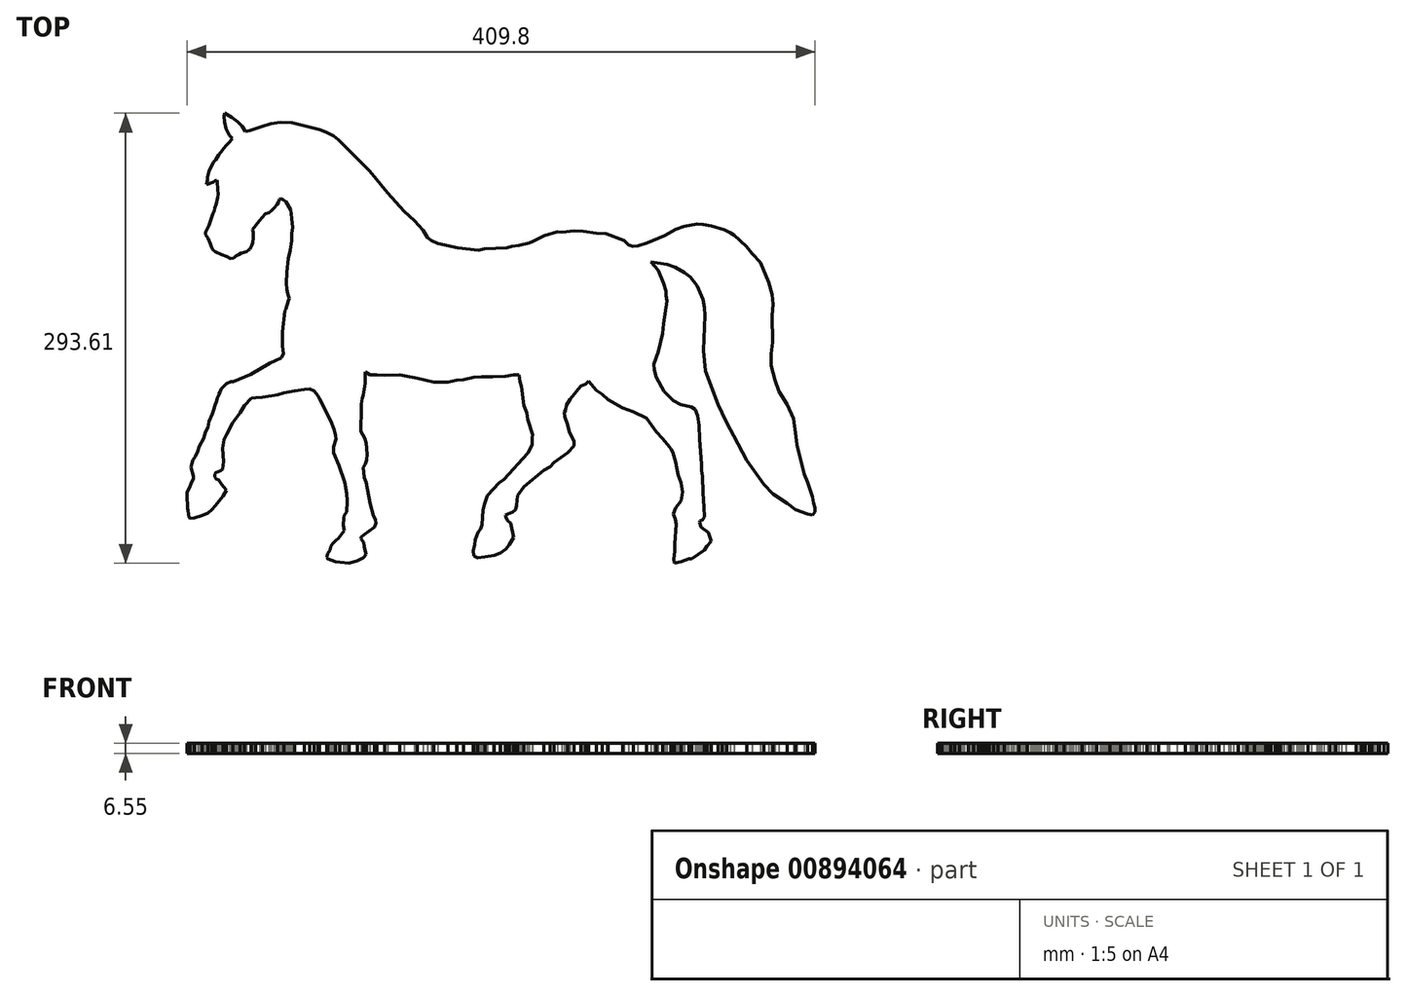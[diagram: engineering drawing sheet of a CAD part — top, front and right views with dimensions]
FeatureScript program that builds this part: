
annotation { "Feature Type Name" : "Feature", "Feature Type Description" : "" }
export const myFeature = defineFeature(function(context is Context, id is Id, definition is map)
    precondition{}
    {
        {
            var Q0;
            Q0=qCreatedBy(makeId("Top.planeOp"),FACE);
            var sketch = newSketch(context, id + "F0", { "sketchPlane" : qUnion([Q0])});
            skLineSegment(sketch, "E0", {"start": v(-21915.78, 16280.24) * mm, "end": v(-22000.3, 16149.3) * mm});
            skLineSegment(sketch, "E1", {"start": v(-22000.3, 16149.3) * mm, "end": v(-22091.45, 16008.1) * mm});
            skLineSegment(sketch, "E2", {"start": v(-22091.45, 16008.1) * mm, "end": v(-22247.54, 15864.17) * mm});
            skLineSegment(sketch, "E3", {"start": v(-22247.54, 15864.17) * mm, "end": v(-22423.74, 15701.7) * mm});
            skLineSegment(sketch, "E4", {"start": v(-22423.74, 15701.7) * mm, "end": v(-22570.85, 15517.79) * mm});
            skLineSegment(sketch, "E5", {"start": v(-22570.85, 15517.79) * mm, "end": v(-22722.85, 15327.75) * mm});
            skLineSegment(sketch, "E6", {"start": v(-22722.85, 15327.75) * mm, "end": v(-22881.74, 15129.12) * mm});
            skLineSegment(sketch, "E7", {"start": v(-22881.74, 15129.12) * mm, "end": v(-23029.7, 14944.14) * mm});
            skLineSegment(sketch, "E8", {"start": v(-23029.7, 14944.14) * mm, "end": v(-23266.76, 14559.18) * mm});
            skLineSegment(sketch, "E9", {"start": v(-23266.76, 14559.18) * mm, "end": v(-23478.07, 14331.08) * mm});
            skLineSegment(sketch, "E10", {"start": v(-23478.07, 14331.08) * mm, "end": v(-23552.03, 14153.67) * mm});
            skLineSegment(sketch, "E11", {"start": v(-23552.03, 14153.67) * mm, "end": v(-23710.77, 13873.46) * mm});
            skLineSegment(sketch, "E12", {"start": v(-23710.77, 13873.46) * mm, "end": v(-23812.2, 13596.78) * mm});
            skLineSegment(sketch, "E13", {"start": v(-23812.2, 13596.78) * mm, "end": v(-23838.03, 13426.67) * mm});
            skLineSegment(sketch, "E14", {"start": v(-23838.03, 13426.67) * mm, "end": v(-23918.33, 13133.1) * mm});
            skLineSegment(sketch, "E15", {"start": v(-23918.33, 13133.1) * mm, "end": v(-23935.24, 12928.22) * mm});
            skLineSegment(sketch, "E16", {"start": v(-23935.24, 12928.22) * mm, "end": v(-23983.84, 12738.14) * mm});
            skLineSegment(sketch, "E17", {"start": v(-23983.84, 12738.14) * mm, "end": v(-23996.52, 12539.6) * mm});
            skLineSegment(sketch, "E18", {"start": v(-23996.52, 12539.6) * mm, "end": v(-23707.02, 12632.53) * mm});
            skLineSegment(sketch, "E19", {"start": v(-23707.02, 12632.53) * mm, "end": v(-23478, 12706.05) * mm});
            skLineSegment(sketch, "E20", {"start": v(-23478, 12706.05) * mm, "end": v(-23297.08, 12833.18) * mm});
            skLineSegment(sketch, "E21", {"start": v(-23297.08, 12833.18) * mm, "end": v(-23193.54, 12877.53) * mm});
            skLineSegment(sketch, "E22", {"start": v(-23193.54, 12877.53) * mm, "end": v(-23157.61, 12742.36) * mm});
            skLineSegment(sketch, "E23", {"start": v(-23157.61, 12742.36) * mm, "end": v(-23121.56, 12443.79) * mm});
            skLineSegment(sketch, "E24", {"start": v(-23121.56, 12443.79) * mm, "end": v(-23082.96, 12124.17) * mm});
            skLineSegment(sketch, "E25", {"start": v(-23082.96, 12124.17) * mm, "end": v(-23079.3, 11739.43) * mm});
            skLineSegment(sketch, "E26", {"start": v(-23079.3, 11739.43) * mm, "end": v(-23100.44, 11473.3) * mm});
            skLineSegment(sketch, "E27", {"start": v(-23100.44, 11473.3) * mm, "end": v(-23163.98, 11187.46) * mm});
            skLineSegment(sketch, "E28", {"start": v(-23163.98, 11187.46) * mm, "end": v(-23215.72, 10954.66) * mm});
            skLineSegment(sketch, "E29", {"start": v(-23215.72, 10954.66) * mm, "end": v(-23326.6, 10630.9) * mm});
            skLineSegment(sketch, "E30", {"start": v(-23326.6, 10630.9) * mm, "end": v(-23392.11, 10362.67) * mm});
            skLineSegment(sketch, "E31", {"start": v(-23392.11, 10362.67) * mm, "end": v(-23489.31, 10140.9) * mm});
            skLineSegment(sketch, "E32", {"start": v(-23489.31, 10140.9) * mm, "end": v(-23561.34, 9888.44) * mm});
            skLineSegment(sketch, "E33", {"start": v(-23561.34, 9888.44) * mm, "end": v(-23677.56, 9675.12) * mm});
            skLineSegment(sketch, "E34", {"start": v(-23677.56, 9675.12) * mm, "end": v(-23740.95, 9470.25) * mm});
            skLineSegment(sketch, "E35", {"start": v(-23740.95, 9470.25) * mm, "end": v(-23823.7, 9202.85) * mm});
            skLineSegment(sketch, "E36", {"start": v(-23823.7, 9202.85) * mm, "end": v(-23910.14, 9025.74) * mm});
            skLineSegment(sketch, "E37", {"start": v(-23910.14, 9025.74) * mm, "end": v(-23980.17, 8882.26) * mm});
            skLineSegment(sketch, "E38", {"start": v(-23980.17, 8882.26) * mm, "end": v(-24052.25, 8734.58) * mm});
            skLineSegment(sketch, "E39", {"start": v(-24052.25, 8734.58) * mm, "end": v(-24102.07, 8632.52) * mm});
            skLineSegment(sketch, "E40", {"start": v(-24102.07, 8632.52) * mm, "end": v(-24096.15, 8435.6) * mm});
            skLineSegment(sketch, "E41", {"start": v(-24096.15, 8435.6) * mm, "end": v(-23893.3, 8139.91) * mm});
            skLineSegment(sketch, "E42", {"start": v(-23893.3, 8139.91) * mm, "end": v(-23700.9, 7699.92) * mm});
            skLineSegment(sketch, "E43", {"start": v(-23700.9, 7699.92) * mm, "end": v(-23616.23, 7435.42) * mm});
            skLineSegment(sketch, "E44", {"start": v(-23616.23, 7435.42) * mm, "end": v(-23493.55, 7196.45) * mm});
            skLineSegment(sketch, "E45", {"start": v(-23493.55, 7196.45) * mm, "end": v(-23297.04, 7052.83) * mm});
            skLineSegment(sketch, "E46", {"start": v(-23297.04, 7052.83) * mm, "end": v(-22781.4, 6798.75) * mm});
            skLineSegment(sketch, "E47", {"start": v(-22781.4, 6798.75) * mm, "end": v(-22344, 6646.68) * mm});
            skLineSegment(sketch, "E48", {"start": v(-22344, 6646.68) * mm, "end": v(-22051.24, 6487.55) * mm});
            skLineSegment(sketch, "E49", {"start": v(-22051.24, 6487.55) * mm, "end": v(-21795.56, 6525.57) * mm});
            skLineSegment(sketch, "E50", {"start": v(-21795.56, 6525.57) * mm, "end": v(-21624.4, 6692.42) * mm});
            skLineSegment(sketch, "E51", {"start": v(-21624.4, 6692.42) * mm, "end": v(-21394.07, 6808.59) * mm});
            skLineSegment(sketch, "E52", {"start": v(-21394.07, 6808.59) * mm, "end": v(-21210.23, 6941.65) * mm});
            skLineSegment(sketch, "E53", {"start": v(-21210.23, 6941.65) * mm, "end": v(-21009.48, 6996.56) * mm});
            skLineSegment(sketch, "E54", {"start": v(-21009.48, 6996.56) * mm, "end": v(-20760.56, 7064.65) * mm});
            skLineSegment(sketch, "E55", {"start": v(-20760.56, 7064.65) * mm, "end": v(-20556.49, 7193.23) * mm});
            skLineSegment(sketch, "E56", {"start": v(-20556.49, 7193.23) * mm, "end": v(-20473.06, 7245.8) * mm});
            skLineSegment(sketch, "E57", {"start": v(-20473.06, 7245.8) * mm, "end": v(-20310.55, 7574.46) * mm});
            skLineSegment(sketch, "E58", {"start": v(-20310.55, 7574.46) * mm, "end": v(-20236.6, 7804.68) * mm});
            skLineSegment(sketch, "E59", {"start": v(-20236.6, 7804.68) * mm, "end": v(-20213.35, 8161.62) * mm});
            skLineSegment(sketch, "E60", {"start": v(-20213.35, 8161.62) * mm, "end": v(-20217.6, 8443.51) * mm});
            skLineSegment(sketch, "E61", {"start": v(-20217.6, 8443.51) * mm, "end": v(-20221, 8669.65) * mm});
            skLineSegment(sketch, "E62", {"start": v(-20221, 8669.65) * mm, "end": v(-20270.42, 8836.36) * mm});
            skLineSegment(sketch, "E63", {"start": v(-20270.42, 8836.36) * mm, "end": v(-20135.04, 9014.46) * mm});
            skLineSegment(sketch, "E64", {"start": v(-20135.04, 9014.46) * mm, "end": v(-19942.51, 9267.73) * mm});
            skLineSegment(sketch, "E65", {"start": v(-19942.51, 9267.73) * mm, "end": v(-19700.94, 9585.52) * mm});
            skLineSegment(sketch, "E66", {"start": v(-19700.94, 9585.52) * mm, "end": v(-19473.4, 9807.2) * mm});
            skLineSegment(sketch, "E67", {"start": v(-19473.4, 9807.2) * mm, "end": v(-19225.81, 10150.22) * mm});
            skLineSegment(sketch, "E68", {"start": v(-19225.81, 10150.22) * mm, "end": v(-18953.22, 10238.92) * mm});
            skLineSegment(sketch, "E69", {"start": v(-18953.22, 10238.92) * mm, "end": v(-18743.24, 10361.65) * mm});
            skLineSegment(sketch, "E70", {"start": v(-18743.24, 10361.65) * mm, "end": v(-18519.25, 10566.52) * mm});
            skLineSegment(sketch, "E71", {"start": v(-18519.25, 10566.52) * mm, "end": v(-18250.48, 10913.46) * mm});
            skLineSegment(sketch, "E72", {"start": v(-18250.48, 10913.46) * mm, "end": v(-18142.47, 11098.26) * mm});
            skLineSegment(sketch, "E73", {"start": v(-18142.47, 11098.26) * mm, "end": v(-18100.21, 11237.66) * mm});
            skLineSegment(sketch, "E74", {"start": v(-18100.21, 11237.66) * mm, "end": v(-18049.5, 11326.37) * mm});
            skLineSegment(sketch, "E75", {"start": v(-18049.5, 11326.37) * mm, "end": v(-17929.05, 11368.6) * mm});
            skLineSegment(sketch, "E76", {"start": v(-17929.05, 11368.6) * mm, "end": v(-17768.45, 11301.02) * mm});
            skLineSegment(sketch, "E77", {"start": v(-17768.45, 11301.02) * mm, "end": v(-17565.6, 11132.06) * mm});
            skLineSegment(sketch, "E78", {"start": v(-17565.6, 11132.06) * mm, "end": v(-17424.02, 10893.4) * mm});
            skLineSegment(sketch, "E79", {"start": v(-17424.02, 10893.4) * mm, "end": v(-17297.06, 10679.38) * mm});
            skLineSegment(sketch, "E80", {"start": v(-17297.06, 10679.38) * mm, "end": v(-17164.28, 10455.56) * mm});
            skLineSegment(sketch, "E81", {"start": v(-17164.28, 10455.56) * mm, "end": v(-17096.15, 10159.32) * mm});
            skLineSegment(sketch, "E82", {"start": v(-17096.15, 10159.32) * mm, "end": v(-17070.8, 9916.43) * mm});
            skLineSegment(sketch, "E83", {"start": v(-17070.8, 9916.43) * mm, "end": v(-17052.77, 9743.8) * mm});
            skLineSegment(sketch, "E84", {"start": v(-17052.77, 9743.8) * mm, "end": v(-17032.08, 9422.22) * mm});
            skLineSegment(sketch, "E85", {"start": v(-17032.08, 9422.22) * mm, "end": v(-17007.66, 9042.48) * mm});
            skLineSegment(sketch, "E86", {"start": v(-17007.66, 9042.48) * mm, "end": v(-17035.08, 8751.12) * mm});
            skLineSegment(sketch, "E87", {"start": v(-17035.08, 8751.12) * mm, "end": v(-17057.97, 8507.85) * mm});
            skLineSegment(sketch, "E88", {"start": v(-17057.97, 8507.85) * mm, "end": v(-17074.62, 7945.34) * mm});
            skLineSegment(sketch, "E89", {"start": v(-17074.62, 7945.34) * mm, "end": v(-17126.43, 7579.78) * mm});
            skLineSegment(sketch, "E90", {"start": v(-17126.43, 7579.78) * mm, "end": v(-17185.47, 7163.26) * mm});
            skLineSegment(sketch, "E91", {"start": v(-17185.47, 7163.26) * mm, "end": v(-17272.81, 6780.14) * mm});
            skLineSegment(sketch, "E92", {"start": v(-17272.81, 6780.14) * mm, "end": v(-17340.94, 6481.3) * mm});
            skLineSegment(sketch, "E93", {"start": v(-17340.94, 6481.3) * mm, "end": v(-17425.28, 5834.24) * mm});
            skLineSegment(sketch, "E94", {"start": v(-17425.28, 5834.24) * mm, "end": v(-17483.88, 5384.66) * mm});
            skLineSegment(sketch, "E95", {"start": v(-17483.88, 5384.66) * mm, "end": v(-17495.33, 4863.98) * mm});
            skLineSegment(sketch, "E96", {"start": v(-17495.33, 4863.98) * mm, "end": v(-17504.17, 4462) * mm});
            skLineSegment(sketch, "E97", {"start": v(-17504.17, 4462) * mm, "end": v(-17470.8, 3976.05) * mm});
            skLineSegment(sketch, "E98", {"start": v(-17470.8, 3976.05) * mm, "end": v(-17388.5, 3583.07) * mm});
            skLineSegment(sketch, "E99", {"start": v(-17388.5, 3583.07) * mm, "end": v(-17257.23, 3246.2) * mm});
            skLineSegment(sketch, "E100", {"start": v(-17257.23, 3246.2) * mm, "end": v(-17363.9, 3048.18) * mm});
            skLineSegment(sketch, "E101", {"start": v(-17363.9, 3048.18) * mm, "end": v(-17421.81, 2844.08) * mm});
            skLineSegment(sketch, "E102", {"start": v(-17421.81, 2844.08) * mm, "end": v(-17486.24, 2617) * mm});
            skLineSegment(sketch, "E103", {"start": v(-17486.24, 2617) * mm, "end": v(-17559.1, 2360.2) * mm});
            skLineSegment(sketch, "E104", {"start": v(-17559.1, 2360.2) * mm, "end": v(-17632.11, 2240.9) * mm});
            skLineSegment(sketch, "E105", {"start": v(-17632.11, 2240.9) * mm, "end": v(-17693, 1693.79) * mm});
            skLineSegment(sketch, "E106", {"start": v(-17693, 1693.79) * mm, "end": v(-17746.7, 1211.32) * mm});
            skLineSegment(sketch, "E107", {"start": v(-17746.7, 1211.32) * mm, "end": v(-17782.24, 892.05) * mm});
            skLineSegment(sketch, "E108", {"start": v(-17782.24, 892.05) * mm, "end": v(-17825.3, 505.21) * mm});
            skLineSegment(sketch, "E109", {"start": v(-17825.3, 505.21) * mm, "end": v(-17824.2, 62.7) * mm});
            skLineSegment(sketch, "E110", {"start": v(-17824.2, 62.7) * mm, "end": v(-17822.4, -667.43) * mm});
            skLineSegment(sketch, "E111", {"start": v(-17822.4, -667.43) * mm, "end": v(-17726.52, -1255.3) * mm});
            skLineSegment(sketch, "E112", {"start": v(-17726.52, -1255.3) * mm, "end": v(-17912.72, -1607.53) * mm});
            skLineSegment(sketch, "E113", {"start": v(-17912.72, -1607.53) * mm, "end": v(-18400.37, -1851.24) * mm});
            skLineSegment(sketch, "E114", {"start": v(-18400.37, -1851.24) * mm, "end": v(-18872.79, -2030.97) * mm});
            skLineSegment(sketch, "E115", {"start": v(-18872.79, -2030.97) * mm, "end": v(-19333.99, -2305.95) * mm});
            skLineSegment(sketch, "E116", {"start": v(-19333.99, -2305.95) * mm, "end": v(-19749.18, -2553.5) * mm});
            skLineSegment(sketch, "E117", {"start": v(-19749.18, -2553.5) * mm, "end": v(-20392.98, -2937.34) * mm});
            skLineSegment(sketch, "E118", {"start": v(-20392.98, -2937.34) * mm, "end": v(-20969.35, -3175.43) * mm});
            skLineSegment(sketch, "E119", {"start": v(-20969.35, -3175.43) * mm, "end": v(-21492.25, -3391.42) * mm});
            skLineSegment(sketch, "E120", {"start": v(-21492.25, -3391.42) * mm, "end": v(-21848.77, -3538.7) * mm});
            skLineSegment(sketch, "E121", {"start": v(-21848.77, -3538.7) * mm, "end": v(-22040.13, -3541.57) * mm});
            skLineSegment(sketch, "E122", {"start": v(-22040.13, -3541.57) * mm, "end": v(-22378.44, -3712.16) * mm});
            skLineSegment(sketch, "E123", {"start": v(-22378.44, -3712.16) * mm, "end": v(-22619.22, -3928.45) * mm});
            skLineSegment(sketch, "E124", {"start": v(-22619.22, -3928.45) * mm, "end": v(-22814.99, -4161.1) * mm});
            skLineSegment(sketch, "E125", {"start": v(-22814.99, -4161.1) * mm, "end": v(-22903.37, -4374.34) * mm});
            skLineSegment(sketch, "E126", {"start": v(-22903.37, -4374.34) * mm, "end": v(-23025.29, -4581.5) * mm});
            skLineSegment(sketch, "E127", {"start": v(-23025.29, -4581.5) * mm, "end": v(-23034.43, -4678.97) * mm});
            skLineSegment(sketch, "E128", {"start": v(-23034.43, -4678.97) * mm, "end": v(-23156.34, -4910.5) * mm});
            skLineSegment(sketch, "E129", {"start": v(-23156.34, -4910.5) * mm, "end": v(-23195.97, -5096.32) * mm});
            skLineSegment(sketch, "E130", {"start": v(-23195.97, -5096.32) * mm, "end": v(-23336.51, -5518.13) * mm});
            skLineSegment(sketch, "E131", {"start": v(-23336.51, -5518.13) * mm, "end": v(-23403.57, -5822.76) * mm});
            skLineSegment(sketch, "E132", {"start": v(-23403.57, -5822.76) * mm, "end": v(-23547.15, -6183.25) * mm});
            skLineSegment(sketch, "E133", {"start": v(-23547.15, -6183.25) * mm, "end": v(-23680.71, -6518.58) * mm});
            skLineSegment(sketch, "E134", {"start": v(-23680.71, -6518.58) * mm, "end": v(-23800.04, -6818.17) * mm});
            skLineSegment(sketch, "E135", {"start": v(-23800.04, -6818.17) * mm, "end": v(-23907.1, -7279.6) * mm});
            skLineSegment(sketch, "E136", {"start": v(-23907.1, -7279.6) * mm, "end": v(-24099.12, -7632.98) * mm});
            skLineSegment(sketch, "E137", {"start": v(-24099.12, -7632.98) * mm, "end": v(-24153.98, -7840.13) * mm});
            skLineSegment(sketch, "E138", {"start": v(-24153.98, -7840.13) * mm, "end": v(-24180.17, -7939.01) * mm});
            skLineSegment(sketch, "E139", {"start": v(-24180.17, -7939.01) * mm, "end": v(-24244.61, -8182.34) * mm});
            skLineSegment(sketch, "E140", {"start": v(-24244.61, -8182.34) * mm, "end": v(-24391.71, -8443.3) * mm});
            skLineSegment(sketch, "E141", {"start": v(-24391.71, -8443.3) * mm, "end": v(-24612.18, -8834.42) * mm});
            skLineSegment(sketch, "E142", {"start": v(-24612.18, -8834.42) * mm, "end": v(-24718.2, -9224.56) * mm});
            skLineSegment(sketch, "E143", {"start": v(-24718.2, -9224.56) * mm, "end": v(-24944.2, -9670.84) * mm});
            skLineSegment(sketch, "E144", {"start": v(-24944.2, -9670.84) * mm, "end": v(-25111.84, -9929.78) * mm});
            skLineSegment(sketch, "E145", {"start": v(-25111.84, -9929.78) * mm, "end": v(-25224.6, -10197.86) * mm});
            skLineSegment(sketch, "E146", {"start": v(-25224.6, -10197.86) * mm, "end": v(-25300.8, -10523.81) * mm});
            skLineSegment(sketch, "E147", {"start": v(-25300.8, -10523.81) * mm, "end": v(-25090.87, -11238.22) * mm});
            skLineSegment(sketch, "E148", {"start": v(-25090.87, -11238.22) * mm, "end": v(-25096.97, -11439.28) * mm});
            skLineSegment(sketch, "E149", {"start": v(-25096.97, -11439.28) * mm, "end": v(-25289.28, -11864.54) * mm});
            skLineSegment(sketch, "E150", {"start": v(-25289.28, -11864.54) * mm, "end": v(-25411.2, -12211.82) * mm});
            skLineSegment(sketch, "E151", {"start": v(-25411.2, -12211.82) * mm, "end": v(-25591.01, -12553.01) * mm});
            skLineSegment(sketch, "E152", {"start": v(-25591.01, -12553.01) * mm, "end": v(-25612.35, -12757.11) * mm});
            skLineSegment(sketch, "E153", {"start": v(-25612.35, -12757.11) * mm, "end": v(-25603.22, -13163.9) * mm});
            skLineSegment(sketch, "E154", {"start": v(-25603.22, -13163.9) * mm, "end": v(-25548.36, -13495.96) * mm});
            skLineSegment(sketch, "E155", {"start": v(-25548.36, -13495.96) * mm, "end": v(-25557.5, -13858.47) * mm});
            skLineSegment(sketch, "E156", {"start": v(-25557.5, -13858.47) * mm, "end": v(-25517.91, -14073.04) * mm});
            skLineSegment(sketch, "E157", {"start": v(-25517.91, -14073.04) * mm, "end": v(-25460, -14609.2) * mm});
            skLineSegment(sketch, "E158", {"start": v(-25460, -14609.2) * mm, "end": v(-25347.23, -14688.4) * mm});
            skLineSegment(sketch, "E159", {"start": v(-25347.23, -14688.4) * mm, "end": v(-24993.69, -14657.93) * mm});
            skLineSegment(sketch, "E160", {"start": v(-24993.69, -14657.93) * mm, "end": v(-24359.74, -14456.88) * mm});
            skLineSegment(sketch, "E161", {"start": v(-24359.74, -14456.88) * mm, "end": v(-23905.61, -14246.68) * mm});
            skLineSegment(sketch, "E162", {"start": v(-23905.61, -14246.68) * mm, "end": v(-23591.68, -13987.74) * mm});
            skLineSegment(sketch, "E163", {"start": v(-23591.68, -13987.74) * mm, "end": v(-23299.1, -13673.97) * mm});
            skLineSegment(sketch, "E164", {"start": v(-23299.1, -13673.97) * mm, "end": v(-22956.74, -13228.65) * mm});
            skLineSegment(sketch, "E165", {"start": v(-22956.74, -13228.65) * mm, "end": v(-22680.7, -12869.58) * mm});
            skLineSegment(sketch, "E166", {"start": v(-22680.7, -12869.58) * mm, "end": v(-22477.78, -12533.12) * mm});
            skLineSegment(sketch, "E167", {"start": v(-22477.78, -12533.12) * mm, "end": v(-22386.03, -12381) * mm});
            skLineSegment(sketch, "E168", {"start": v(-22386.03, -12381) * mm, "end": v(-22630.64, -12139.87) * mm});
            skLineSegment(sketch, "E169", {"start": v(-22630.64, -12139.87) * mm, "end": v(-22770.84, -11908.35) * mm});
            skLineSegment(sketch, "E170", {"start": v(-22770.84, -11908.35) * mm, "end": v(-23039.4, -11563.13) * mm});
            skLineSegment(sketch, "E171", {"start": v(-23039.4, -11563.13) * mm, "end": v(-23234.47, -11502.2) * mm});
            skLineSegment(sketch, "E172", {"start": v(-23234.47, -11502.2) * mm, "end": v(-23332, -11319.42) * mm});
            skLineSegment(sketch, "E173", {"start": v(-23332, -11319.42) * mm, "end": v(-23347.12, -11107.4) * mm});
            skLineSegment(sketch, "E174", {"start": v(-23347.12, -11107.4) * mm, "end": v(-23261.78, -10973.37) * mm});
            skLineSegment(sketch, "E175", {"start": v(-23261.78, -10973.37) * mm, "end": v(-23094.15, -10897.21) * mm});
            skLineSegment(sketch, "E176", {"start": v(-23094.15, -10897.21) * mm, "end": v(-22865.9, -10793.5) * mm});
            skLineSegment(sketch, "E177", {"start": v(-22865.9, -10793.5) * mm, "end": v(-22694.89, -10680.92) * mm});
            skLineSegment(sketch, "E178", {"start": v(-22694.89, -10680.92) * mm, "end": v(-22673.55, -10495.1) * mm});
            skLineSegment(sketch, "E179", {"start": v(-22673.55, -10495.1) * mm, "end": v(-22621.66, -10043.12) * mm});
            skLineSegment(sketch, "E180", {"start": v(-22621.66, -10043.12) * mm, "end": v(-22663.85, -9567.5) * mm});
            skLineSegment(sketch, "E181", {"start": v(-22663.85, -9567.5) * mm, "end": v(-22695.89, -9206.28) * mm});
            skLineSegment(sketch, "E182", {"start": v(-22695.89, -9206.28) * mm, "end": v(-22715.67, -8983.22) * mm});
            skLineSegment(sketch, "E183", {"start": v(-22715.67, -8983.22) * mm, "end": v(-22572.07, -8289.2) * mm});
            skLineSegment(sketch, "E184", {"start": v(-22572.07, -8289.2) * mm, "end": v(-22380.06, -7859.67) * mm});
            skLineSegment(sketch, "E185", {"start": v(-22380.06, -7859.67) * mm, "end": v(-22090.2, -7307.05) * mm});
            skLineSegment(sketch, "E186", {"start": v(-22090.2, -7307.05) * mm, "end": v(-21860.43, -6869) * mm});
            skLineSegment(sketch, "E187", {"start": v(-21860.43, -6869) * mm, "end": v(-21474, -6343.3) * mm});
            skLineSegment(sketch, "E188", {"start": v(-21474, -6343.3) * mm, "end": v(-21275.88, -6073.79) * mm});
            skLineSegment(sketch, "E189", {"start": v(-21275.88, -6073.79) * mm, "end": v(-20909.62, -5501.3) * mm});
            skLineSegment(sketch, "E190", {"start": v(-20909.62, -5501.3) * mm, "end": v(-20687.13, -5257.6) * mm});
            skLineSegment(sketch, "E191", {"start": v(-20687.13, -5257.6) * mm, "end": v(-20351.58, -4890.05) * mm});
            skLineSegment(sketch, "E192", {"start": v(-20351.58, -4890.05) * mm, "end": v(-20022.18, -4857.29) * mm});
            skLineSegment(sketch, "E193", {"start": v(-20022.18, -4857.29) * mm, "end": v(-19469.09, -4838.97) * mm});
            skLineSegment(sketch, "E194", {"start": v(-19469.09, -4838.97) * mm, "end": v(-18758.94, -4704.93) * mm});
            skLineSegment(sketch, "E195", {"start": v(-18758.94, -4704.93) * mm, "end": v(-18215.77, -4602.4) * mm});
            skLineSegment(sketch, "E196", {"start": v(-18215.77, -4602.4) * mm, "end": v(-17718.5, -4466.97) * mm});
            skLineSegment(sketch, "E197", {"start": v(-17718.5, -4466.97) * mm, "end": v(-16833.92, -4288.88) * mm});
            skLineSegment(sketch, "E198", {"start": v(-16833.92, -4288.88) * mm, "end": v(-16050.63, -4170.07) * mm});
            skLineSegment(sketch, "E199", {"start": v(-16050.63, -4170.07) * mm, "end": v(-15597.52, -4139.48) * mm});
            skLineSegment(sketch, "E200", {"start": v(-15597.52, -4139.48) * mm, "end": v(-15231.78, -4300.93) * mm});
            skLineSegment(sketch, "E201", {"start": v(-15231.78, -4300.93) * mm, "end": v(-14923.95, -4696.95) * mm});
            skLineSegment(sketch, "E202", {"start": v(-14923.95, -4696.95) * mm, "end": v(-14814.23, -4949.8) * mm});
            skLineSegment(sketch, "E203", {"start": v(-14814.23, -4949.8) * mm, "end": v(-14420.75, -5723.13) * mm});
            skLineSegment(sketch, "E204", {"start": v(-14420.75, -5723.13) * mm, "end": v(-14148.3, -6258.62) * mm});
            skLineSegment(sketch, "E205", {"start": v(-14148.3, -6258.62) * mm, "end": v(-13902.4, -6741.93) * mm});
            skLineSegment(sketch, "E206", {"start": v(-13902.4, -6741.93) * mm, "end": v(-13631.1, -7436.77) * mm});
            skLineSegment(sketch, "E207", {"start": v(-13631.1, -7436.77) * mm, "end": v(-13481.75, -7908.95) * mm});
            skLineSegment(sketch, "E208", {"start": v(-13481.75, -7908.95) * mm, "end": v(-13454.13, -8224.44) * mm});
            skLineSegment(sketch, "E209", {"start": v(-13454.13, -8224.44) * mm, "end": v(-13554.7, -8556.48) * mm});
            skLineSegment(sketch, "E210", {"start": v(-13554.7, -8556.48) * mm, "end": v(-13653.82, -8883.71) * mm});
            skLineSegment(sketch, "E211", {"start": v(-13653.82, -8883.71) * mm, "end": v(-13649.1, -9362.04) * mm});
            skLineSegment(sketch, "E212", {"start": v(-13649.1, -9362.04) * mm, "end": v(-13435.75, -9858.59) * mm});
            skLineSegment(sketch, "E213", {"start": v(-13435.75, -9858.59) * mm, "end": v(-13207.45, -10389.93) * mm});
            skLineSegment(sketch, "E214", {"start": v(-13207.45, -10389.93) * mm, "end": v(-13005.85, -10999.46) * mm});
            skLineSegment(sketch, "E215", {"start": v(-13005.85, -10999.46) * mm, "end": v(-12758.24, -11748.1) * mm});
            skLineSegment(sketch, "E216", {"start": v(-12758.24, -11748.1) * mm, "end": v(-12587.1, -12687.54) * mm});
            skLineSegment(sketch, "E217", {"start": v(-12587.1, -12687.54) * mm, "end": v(-12556.61, -13275.48) * mm});
            skLineSegment(sketch, "E218", {"start": v(-12556.61, -13275.48) * mm, "end": v(-12589.9, -14185.58) * mm});
            skLineSegment(sketch, "E219", {"start": v(-12589.9, -14185.58) * mm, "end": v(-12772.77, -14407.96) * mm});
            skLineSegment(sketch, "E220", {"start": v(-12772.77, -14407.96) * mm, "end": v(-12839.82, -14663.85) * mm});
            skLineSegment(sketch, "E221", {"start": v(-12839.82, -14663.85) * mm, "end": v(-12876.2, -15241.64) * mm});
            skLineSegment(sketch, "E222", {"start": v(-12876.2, -15241.64) * mm, "end": v(-12784.77, -15701.63) * mm});
            skLineSegment(sketch, "E223", {"start": v(-12784.77, -15701.63) * mm, "end": v(-12973.73, -15945.34) * mm});
            skLineSegment(sketch, "E224", {"start": v(-12973.73, -15945.34) * mm, "end": v(-13272.19, -16330.25) * mm});
            skLineSegment(sketch, "E225", {"start": v(-13272.19, -16330.25) * mm, "end": v(-13467.85, -16477) * mm});
            skLineSegment(sketch, "E226", {"start": v(-13467.85, -16477) * mm, "end": v(-13729.97, -16757.26) * mm});
            skLineSegment(sketch, "E227", {"start": v(-13729.97, -16757.26) * mm, "end": v(-13885.4, -17007.06) * mm});
            skLineSegment(sketch, "E228", {"start": v(-13885.4, -17007.06) * mm, "end": v(-13949.41, -17266) * mm});
            skLineSegment(sketch, "E229", {"start": v(-13949.41, -17266) * mm, "end": v(-14114.6, -17575.44) * mm});
            skLineSegment(sketch, "E230", {"start": v(-14114.6, -17575.44) * mm, "end": v(-14196.88, -17886.16) * mm});
            skLineSegment(sketch, "E231", {"start": v(-14196.88, -17886.16) * mm, "end": v(-14142.02, -18014.1) * mm});
            skLineSegment(sketch, "E232", {"start": v(-14142.02, -18014.1) * mm, "end": v(-13867.72, -18105.5) * mm});
            skLineSegment(sketch, "E233", {"start": v(-13867.72, -18105.5) * mm, "end": v(-13512.03, -18224) * mm});
            skLineSegment(sketch, "E234", {"start": v(-13512.03, -18224) * mm, "end": v(-13124.05, -18288.28) * mm});
            skLineSegment(sketch, "E235", {"start": v(-13124.05, -18288.28) * mm, "end": v(-12694.3, -18315.7) * mm});
            skLineSegment(sketch, "E236", {"start": v(-12694.3, -18315.7) * mm, "end": v(-12397.24, -18334.65) * mm});
            skLineSegment(sketch, "E237", {"start": v(-12397.24, -18334.65) * mm, "end": v(-11702.7, -18136.37) * mm});
            skLineSegment(sketch, "E238", {"start": v(-11702.7, -18136.37) * mm, "end": v(-11233.34, -17917.03) * mm});
            skLineSegment(sketch, "E239", {"start": v(-11233.34, -17917.03) * mm, "end": v(-11009.84, -17651.84) * mm});
            skLineSegment(sketch, "E240", {"start": v(-11009.84, -17651.84) * mm, "end": v(-11067.75, -17365.49) * mm});
            skLineSegment(sketch, "E241", {"start": v(-11067.75, -17365.49) * mm, "end": v(-11174.42, -17012.11) * mm});
            skLineSegment(sketch, "E242", {"start": v(-11174.42, -17012.11) * mm, "end": v(-11198.74, -16645.2) * mm});
            skLineSegment(sketch, "E243", {"start": v(-11198.74, -16645.2) * mm, "end": v(-11338.94, -16480.69) * mm});
            skLineSegment(sketch, "E244", {"start": v(-11338.94, -16480.69) * mm, "end": v(-11429.2, -16374.77) * mm});
            skLineSegment(sketch, "E245", {"start": v(-11429.2, -16374.77) * mm, "end": v(-11399.9, -16194.34) * mm});
            skLineSegment(sketch, "E246", {"start": v(-11399.9, -16194.34) * mm, "end": v(-11207.88, -16054.2) * mm});
            skLineSegment(sketch, "E247", {"start": v(-11207.88, -16054.2) * mm, "end": v(-10947.08, -15863.87) * mm});
            skLineSegment(sketch, "E248", {"start": v(-10947.08, -15863.87) * mm, "end": v(-10526.32, -15556.8) * mm});
            skLineSegment(sketch, "E249", {"start": v(-10526.32, -15556.8) * mm, "end": v(-10310.28, -15399.14) * mm});
            skLineSegment(sketch, "E250", {"start": v(-10310.28, -15399.14) * mm, "end": v(-10222.44, -15104.77) * mm});
            skLineSegment(sketch, "E251", {"start": v(-10222.44, -15104.77) * mm, "end": v(-10262.06, -14775.77) * mm});
            skLineSegment(sketch, "E252", {"start": v(-10262.06, -14775.77) * mm, "end": v(-10387.02, -14507.7) * mm});
            skLineSegment(sketch, "E253", {"start": v(-10387.02, -14507.7) * mm, "end": v(-10542.55, -13985.32) * mm});
            skLineSegment(sketch, "E254", {"start": v(-10542.55, -13985.32) * mm, "end": v(-10690.41, -13488.65) * mm});
            skLineSegment(sketch, "E255", {"start": v(-10690.41, -13488.65) * mm, "end": v(-10786.47, -12938.88) * mm});
            skLineSegment(sketch, "E256", {"start": v(-10786.47, -12938.88) * mm, "end": v(-10863.46, -12498.22) * mm});
            skLineSegment(sketch, "E257", {"start": v(-10863.46, -12498.22) * mm, "end": v(-10988.61, -11781.88) * mm});
            skLineSegment(sketch, "E258", {"start": v(-10988.61, -11781.88) * mm, "end": v(-11140.02, -11374.57) * mm});
            skLineSegment(sketch, "E259", {"start": v(-11140.02, -11374.57) * mm, "end": v(-11249.7, -10525.38) * mm});
            skLineSegment(sketch, "E260", {"start": v(-11249.7, -10525.38) * mm, "end": v(-11082.07, -10281.67) * mm});
            skLineSegment(sketch, "E261", {"start": v(-11082.07, -10281.67) * mm, "end": v(-10957.1, -9955.71) * mm});
            skLineSegment(sketch, "E262", {"start": v(-10957.1, -9955.71) * mm, "end": v(-10914.26, -9445.55) * mm});
            skLineSegment(sketch, "E263", {"start": v(-10914.26, -9445.55) * mm, "end": v(-10950.83, -9019.07) * mm});
            skLineSegment(sketch, "E264", {"start": v(-10950.83, -9019.07) * mm, "end": v(-10992.68, -8531.1) * mm});
            skLineSegment(sketch, "E265", {"start": v(-10992.68, -8531.1) * mm, "end": v(-11136.78, -8167.7) * mm});
            skLineSegment(sketch, "E266", {"start": v(-11136.78, -8167.7) * mm, "end": v(-11295.27, -7872.2) * mm});
            skLineSegment(sketch, "E267", {"start": v(-11295.27, -7872.2) * mm, "end": v(-11448.65, -7586.24) * mm});
            skLineSegment(sketch, "E268", {"start": v(-11448.65, -7586.24) * mm, "end": v(-11448.06, -7352.77) * mm});
            skLineSegment(sketch, "E269", {"start": v(-11448.06, -7352.77) * mm, "end": v(-11446.86, -6877.5) * mm});
            skLineSegment(sketch, "E270", {"start": v(-11446.86, -6877.5) * mm, "end": v(-11393.02, -6391.84) * mm});
            skLineSegment(sketch, "E271", {"start": v(-11393.02, -6391.84) * mm, "end": v(-11396.07, -5913.57) * mm});
            skLineSegment(sketch, "E272", {"start": v(-11396.07, -5913.57) * mm, "end": v(-11399.6, -5360.23) * mm});
            skLineSegment(sketch, "E273", {"start": v(-11399.6, -5360.23) * mm, "end": v(-11335.1, -4891.23) * mm});
            skLineSegment(sketch, "E274", {"start": v(-11335.1, -4891.23) * mm, "end": v(-11252.81, -4662.76) * mm});
            skLineSegment(sketch, "E275", {"start": v(-11252.81, -4662.76) * mm, "end": v(-11066.7, -3679.84) * mm});
            skLineSegment(sketch, "E276", {"start": v(-11066.7, -3679.84) * mm, "end": v(-11075.85, -3338.65) * mm});
            skLineSegment(sketch, "E277", {"start": v(-11075.85, -3338.65) * mm, "end": v(-11091.92, -2739.1) * mm});
            skLineSegment(sketch, "E278", {"start": v(-11091.92, -2739.1) * mm, "end": v(-10673.44, -2974.46) * mm});
            skLineSegment(sketch, "E279", {"start": v(-10673.44, -2974.46) * mm, "end": v(-10140.07, -2980.55) * mm});
            skLineSegment(sketch, "E280", {"start": v(-10140.07, -2980.55) * mm, "end": v(-9469.55, -3023.2) * mm});
            skLineSegment(sketch, "E281", {"start": v(-9469.55, -3023.2) * mm, "end": v(-8960.56, -3017.1) * mm});
            skLineSegment(sketch, "E282", {"start": v(-8960.56, -3017.1) * mm, "end": v(-8258.4, -3008.7) * mm});
            skLineSegment(sketch, "E283", {"start": v(-8258.4, -3008.7) * mm, "end": v(-7871.16, -3075.13) * mm});
            skLineSegment(sketch, "E284", {"start": v(-7871.16, -3075.13) * mm, "end": v(-7593.02, -3122.84) * mm});
            skLineSegment(sketch, "E285", {"start": v(-7593.02, -3122.84) * mm, "end": v(-6823.33, -3254.87) * mm});
            skLineSegment(sketch, "E286", {"start": v(-6823.33, -3254.87) * mm, "end": v(-6074.28, -3441.38) * mm});
            skLineSegment(sketch, "E287", {"start": v(-6074.28, -3441.38) * mm, "end": v(-5820.38, -3504.6) * mm});
            skLineSegment(sketch, "E288", {"start": v(-5820.38, -3504.6) * mm, "end": v(-5498.95, -3584.63) * mm});
            skLineSegment(sketch, "E289", {"start": v(-5498.95, -3584.63) * mm, "end": v(-4920.02, -3591.33) * mm});
            skLineSegment(sketch, "E290", {"start": v(-4920.02, -3591.33) * mm, "end": v(-4313.73, -3598.34) * mm});
            skLineSegment(sketch, "E291", {"start": v(-4313.73, -3598.34) * mm, "end": v(-3611.27, -3447.91) * mm});
            skLineSegment(sketch, "E292", {"start": v(-3611.27, -3447.91) * mm, "end": v(-3065.71, -3374.8) * mm});
            skLineSegment(sketch, "E293", {"start": v(-3065.71, -3374.8) * mm, "end": v(-2229.32, -3188.76) * mm});
            skLineSegment(sketch, "E294", {"start": v(-2229.32, -3188.76) * mm, "end": v(-1580.13, -3161.34) * mm});
            skLineSegment(sketch, "E295", {"start": v(-1580.13, -3161.34) * mm, "end": v(-676.78, -3170.31) * mm});
            skLineSegment(sketch, "E296", {"start": v(-676.78, -3170.31) * mm, "end": v(336.43, -3127.68) * mm});
            skLineSegment(sketch, "E297", {"start": v(336.43, -3127.68) * mm, "end": v(1025.24, -3011.92) * mm});
            skLineSegment(sketch, "E298", {"start": v(1025.24, -3011.92) * mm, "end": v(1459.03, -2984.32) * mm});
            skLineSegment(sketch, "E299", {"start": v(1459.03, -2984.32) * mm, "end": v(1544.37, -3532.66) * mm});
            skLineSegment(sketch, "E300", {"start": v(1544.37, -3532.66) * mm, "end": v(1663.23, -3950) * mm});
            skLineSegment(sketch, "E301", {"start": v(1663.23, -3950) * mm, "end": v(1779.18, -4758.58) * mm});
            skLineSegment(sketch, "E302", {"start": v(1779.18, -4758.58) * mm, "end": v(1882.35, -5477.99) * mm});
            skLineSegment(sketch, "E303", {"start": v(1882.35, -5477.99) * mm, "end": v(2079.67, -6081.01) * mm});
            skLineSegment(sketch, "E304", {"start": v(2079.67, -6081.01) * mm, "end": v(2190.7, -6625.77) * mm});
            skLineSegment(sketch, "E305", {"start": v(2190.7, -6625.77) * mm, "end": v(2493.82, -7626.46) * mm});
            skLineSegment(sketch, "E306", {"start": v(2493.82, -7626.46) * mm, "end": v(2568.71, -7873.71) * mm});
            skLineSegment(sketch, "E307", {"start": v(2568.71, -7873.71) * mm, "end": v(2529.14, -8120.78) * mm});
            skLineSegment(sketch, "E308", {"start": v(2529.14, -8120.78) * mm, "end": v(2529.45, -8703.2) * mm});
            skLineSegment(sketch, "E309", {"start": v(2529.45, -8703.2) * mm, "end": v(2367.96, -9026.03) * mm});
            skLineSegment(sketch, "E310", {"start": v(2367.96, -9026.03) * mm, "end": v(2190.31, -9381.15) * mm});
            skLineSegment(sketch, "E311", {"start": v(2190.31, -9381.15) * mm, "end": v(1903.68, -9696.89) * mm});
            skLineSegment(sketch, "E312", {"start": v(1903.68, -9696.89) * mm, "end": v(1444.6, -10202.58) * mm});
            skLineSegment(sketch, "E313", {"start": v(1444.6, -10202.58) * mm, "end": v(1088.96, -10594.33) * mm});
            skLineSegment(sketch, "E314", {"start": v(1088.96, -10594.33) * mm, "end": v(797.45, -10915.45) * mm});
            skLineSegment(sketch, "E315", {"start": v(797.45, -10915.45) * mm, "end": v(541.28, -11197.62) * mm});
            skLineSegment(sketch, "E316", {"start": v(541.28, -11197.62) * mm, "end": v(226.02, -11544.9) * mm});
            skLineSegment(sketch, "E317", {"start": v(226.02, -11544.9) * mm, "end": v(-155.69, -11823.98) * mm});
            skLineSegment(sketch, "E318", {"start": v(-155.69, -11823.98) * mm, "end": v(-651.37, -12356.55) * mm});
            skLineSegment(sketch, "E319", {"start": v(-651.37, -12356.55) * mm, "end": v(-1097.17, -12835.54) * mm});
            skLineSegment(sketch, "E320", {"start": v(-1097.17, -12835.54) * mm, "end": v(-1206.49, -13133.34) * mm});
            skLineSegment(sketch, "E321", {"start": v(-1206.49, -13133.34) * mm, "end": v(-1353.47, -13533.75) * mm});
            skLineSegment(sketch, "E322", {"start": v(-1353.47, -13533.75) * mm, "end": v(-1479.48, -14043.89) * mm});
            skLineSegment(sketch, "E323", {"start": v(-1479.48, -14043.89) * mm, "end": v(-1499.67, -14427.24) * mm});
            skLineSegment(sketch, "E324", {"start": v(-1499.67, -14427.24) * mm, "end": v(-1524.8, -14904.57) * mm});
            skLineSegment(sketch, "E325", {"start": v(-1524.8, -14904.57) * mm, "end": v(-1541.5, -15221.73) * mm});
            skLineSegment(sketch, "E326", {"start": v(-1541.5, -15221.73) * mm, "end": v(-1681.35, -15567.2) * mm});
            skLineSegment(sketch, "E327", {"start": v(-1681.35, -15567.2) * mm, "end": v(-1857.97, -15809.3) * mm});
            skLineSegment(sketch, "E328", {"start": v(-1857.97, -15809.3) * mm, "end": v(-1955.23, -16058.11) * mm});
            skLineSegment(sketch, "E329", {"start": v(-1955.23, -16058.11) * mm, "end": v(-2101.94, -16433.43) * mm});
            skLineSegment(sketch, "E330", {"start": v(-2101.94, -16433.43) * mm, "end": v(-2147.04, -16826.62) * mm});
            skLineSegment(sketch, "E331", {"start": v(-2147.04, -16826.62) * mm, "end": v(-2258.06, -17310.85) * mm});
            skLineSegment(sketch, "E332", {"start": v(-2258.06, -17310.85) * mm, "end": v(-2242.92, -17759.77) * mm});
            skLineSegment(sketch, "E333", {"start": v(-2242.92, -17759.77) * mm, "end": v(-1914.9, -17901) * mm});
            skLineSegment(sketch, "E334", {"start": v(-1914.9, -17901) * mm, "end": v(-1314.35, -17840.48) * mm});
            skLineSegment(sketch, "E335", {"start": v(-1314.35, -17840.48) * mm, "end": v(-547.28, -17704.29) * mm});
            skLineSegment(sketch, "E336", {"start": v(-547.28, -17704.29) * mm, "end": v(-37.58, -17512.62) * mm});
            skLineSegment(sketch, "E337", {"start": v(-37.58, -17512.62) * mm, "end": v(381.29, -17215.02) * mm});
            skLineSegment(sketch, "E338", {"start": v(381.29, -17215.02) * mm, "end": v(689.13, -16841.76) * mm});
            skLineSegment(sketch, "E339", {"start": v(689.13, -16841.76) * mm, "end": v(916.22, -16443.28) * mm});
            skLineSegment(sketch, "E340", {"start": v(916.22, -16443.28) * mm, "end": v(1028.7, -16245.92) * mm});
            skLineSegment(sketch, "E341", {"start": v(1028.7, -16245.92) * mm, "end": v(951.55, -15878.34) * mm});
            skLineSegment(sketch, "E342", {"start": v(951.55, -15878.34) * mm, "end": v(872.1, -15499.77) * mm});
            skLineSegment(sketch, "E343", {"start": v(872.1, -15499.77) * mm, "end": v(791.15, -15114.1) * mm});
            skLineSegment(sketch, "E344", {"start": v(791.15, -15114.1) * mm, "end": v(528.09, -14841.64) * mm});
            skLineSegment(sketch, "E345", {"start": v(528.09, -14841.64) * mm, "end": v(376.7, -14599.53) * mm});
            skLineSegment(sketch, "E346", {"start": v(376.7, -14599.53) * mm, "end": v(371.65, -14412.9) * mm});
            skLineSegment(sketch, "E347", {"start": v(371.65, -14412.9) * mm, "end": v(669.4, -14301.93) * mm});
            skLineSegment(sketch, "E348", {"start": v(669.4, -14301.93) * mm, "end": v(932.9, -14203.72) * mm});
            skLineSegment(sketch, "E349", {"start": v(932.9, -14203.72) * mm, "end": v(1184.14, -13979.1) * mm});
            skLineSegment(sketch, "E350", {"start": v(1184.14, -13979.1) * mm, "end": v(1269.93, -13646.2) * mm});
            skLineSegment(sketch, "E351", {"start": v(1269.93, -13646.2) * mm, "end": v(1316.4, -13043.75) * mm});
            skLineSegment(sketch, "E352", {"start": v(1316.4, -13043.75) * mm, "end": v(1333.77, -12818.48) * mm});
            skLineSegment(sketch, "E353", {"start": v(1333.77, -12818.48) * mm, "end": v(1624.23, -12433.42) * mm});
            skLineSegment(sketch, "E354", {"start": v(1624.23, -12433.42) * mm, "end": v(1845.5, -12140.1) * mm});
            skLineSegment(sketch, "E355", {"start": v(1845.5, -12140.1) * mm, "end": v(2128.89, -11903.8) * mm});
            skLineSegment(sketch, "E356", {"start": v(2128.89, -11903.8) * mm, "end": v(2525.21, -11573.33) * mm});
            skLineSegment(sketch, "E357", {"start": v(2525.21, -11573.33) * mm, "end": v(3083.88, -11107.5) * mm});
            skLineSegment(sketch, "E358", {"start": v(3083.88, -11107.5) * mm, "end": v(3479.32, -10777.76) * mm});
            skLineSegment(sketch, "E359", {"start": v(3479.32, -10777.76) * mm, "end": v(4004.1, -10489.12) * mm});
            skLineSegment(sketch, "E360", {"start": v(4004.1, -10489.12) * mm, "end": v(4301.86, -10141.08) * mm});
            skLineSegment(sketch, "E361", {"start": v(4301.86, -10141.08) * mm, "end": v(4893.7, -9725.64) * mm});
            skLineSegment(sketch, "E362", {"start": v(4893.7, -9725.64) * mm, "end": v(5432.63, -9347.34) * mm});
            skLineSegment(sketch, "E363", {"start": v(5432.63, -9347.34) * mm, "end": v(5817.22, -8948.86) * mm});
            skLineSegment(sketch, "E364", {"start": v(5817.22, -8948.86) * mm, "end": v(5965.39, -8795.33) * mm});
            skLineSegment(sketch, "E365", {"start": v(5965.39, -8795.33) * mm, "end": v(5945.08, -8437.43) * mm});
            skLineSegment(sketch, "E366", {"start": v(5945.08, -8437.43) * mm, "end": v(5753.31, -8044) * mm});
            skLineSegment(sketch, "E367", {"start": v(5753.31, -8044) * mm, "end": v(5541.73, -7609.9) * mm});
            skLineSegment(sketch, "E368", {"start": v(5541.73, -7609.9) * mm, "end": v(5419.87, -7098.25) * mm});
            skLineSegment(sketch, "E369", {"start": v(5419.87, -7098.25) * mm, "end": v(5192.77, -6412.26) * mm});
            skLineSegment(sketch, "E370", {"start": v(5192.77, -6412.26) * mm, "end": v(5167.54, -6039) * mm});
            skLineSegment(sketch, "E371", {"start": v(5167.54, -6039) * mm, "end": v(5258.38, -5837.24) * mm});
            skLineSegment(sketch, "E372", {"start": v(5258.38, -5837.24) * mm, "end": v(5324.68, -5490.95) * mm});
            skLineSegment(sketch, "E373", {"start": v(5324.68, -5490.95) * mm, "end": v(5622.42, -4971.41) * mm});
            skLineSegment(sketch, "E374", {"start": v(5622.42, -4971.41) * mm, "end": v(6021.1, -4497.27) * mm});
            skLineSegment(sketch, "E375", {"start": v(6021.1, -4497.27) * mm, "end": v(6275.08, -4195.22) * mm});
            skLineSegment(sketch, "E376", {"start": v(6275.08, -4195.22) * mm, "end": v(6509.3, -3916.66) * mm});
            skLineSegment(sketch, "E377", {"start": v(6509.3, -3916.66) * mm, "end": v(6904.25, -3755.8) * mm});
            skLineSegment(sketch, "E378", {"start": v(6904.25, -3755.8) * mm, "end": v(7151.97, -3507.52) * mm});
            skLineSegment(sketch, "E379", {"start": v(7151.97, -3507.52) * mm, "end": v(7389.16, -3805.12) * mm});
            skLineSegment(sketch, "E380", {"start": v(7389.16, -3805.12) * mm, "end": v(7756.92, -4266.55) * mm});
            skLineSegment(sketch, "E381", {"start": v(7756.92, -4266.55) * mm, "end": v(8247.08, -4597.04) * mm});
            skLineSegment(sketch, "E382", {"start": v(8247.08, -4597.04) * mm, "end": v(8716.4, -5010.65) * mm});
            skLineSegment(sketch, "E383", {"start": v(8716.4, -5010.65) * mm, "end": v(9251.34, -5318.34) * mm});
            skLineSegment(sketch, "E384", {"start": v(9251.34, -5318.34) * mm, "end": v(9914.25, -5699.64) * mm});
            skLineSegment(sketch, "E385", {"start": v(9914.25, -5699.64) * mm, "end": v(10771.6, -6020.27) * mm});
            skLineSegment(sketch, "E386", {"start": v(10771.6, -6020.27) * mm, "end": v(11601.08, -6399.5) * mm});
            skLineSegment(sketch, "E387", {"start": v(11601.08, -6399.5) * mm, "end": v(11877.26, -6525.77) * mm});
            skLineSegment(sketch, "E388", {"start": v(11877.26, -6525.77) * mm, "end": v(12267.22, -7095.58) * mm});
            skLineSegment(sketch, "E389", {"start": v(12267.22, -7095.58) * mm, "end": v(12642.5, -7643.93) * mm});
            skLineSegment(sketch, "E390", {"start": v(12642.5, -7643.93) * mm, "end": v(13170.97, -8196.56) * mm});
            skLineSegment(sketch, "E391", {"start": v(13170.97, -8196.56) * mm, "end": v(13742.33, -8875.32) * mm});
            skLineSegment(sketch, "E392", {"start": v(13742.33, -8875.32) * mm, "end": v(13859.13, -9014.07) * mm});
            skLineSegment(sketch, "E393", {"start": v(13859.13, -9014.07) * mm, "end": v(14009.8, -9319.2) * mm});
            skLineSegment(sketch, "E394", {"start": v(14009.8, -9319.2) * mm, "end": v(14161.2, -9838.73) * mm});
            skLineSegment(sketch, "E395", {"start": v(14161.2, -9838.73) * mm, "end": v(14251.68, -10149.25) * mm});
            skLineSegment(sketch, "E396", {"start": v(14251.68, -10149.25) * mm, "end": v(14308.07, -10593.12) * mm});
            skLineSegment(sketch, "E397", {"start": v(14308.07, -10593.12) * mm, "end": v(14449.38, -11153) * mm});
            skLineSegment(sketch, "E398", {"start": v(14449.38, -11153) * mm, "end": v(14681.52, -11823.87) * mm});
            skLineSegment(sketch, "E399", {"start": v(14681.52, -11823.87) * mm, "end": v(14788.2, -12573.44) * mm});
            skLineSegment(sketch, "E400", {"start": v(14788.2, -12573.44) * mm, "end": v(14672.13, -13284.65) * mm});
            skLineSegment(sketch, "E401", {"start": v(14672.13, -13284.65) * mm, "end": v(14480.36, -13536.85) * mm});
            skLineSegment(sketch, "E402", {"start": v(14480.36, -13536.85) * mm, "end": v(14258.64, -13828.45) * mm});
            skLineSegment(sketch, "E403", {"start": v(14258.64, -13828.45) * mm, "end": v(14147.3, -14101.79) * mm});
            skLineSegment(sketch, "E404", {"start": v(14147.3, -14101.79) * mm, "end": v(14051.18, -14337.7) * mm});
            skLineSegment(sketch, "E405", {"start": v(14051.18, -14337.7) * mm, "end": v(14192.66, -14740.37) * mm});
            skLineSegment(sketch, "E406", {"start": v(14192.66, -14740.37) * mm, "end": v(14278.45, -15174.16) * mm});
            skLineSegment(sketch, "E407", {"start": v(14278.45, -15174.16) * mm, "end": v(14248.17, -15623.08) * mm});
            skLineSegment(sketch, "E408", {"start": v(14248.17, -15623.08) * mm, "end": v(14217.17, -16082.72) * mm});
            skLineSegment(sketch, "E409", {"start": v(14217.17, -16082.72) * mm, "end": v(14206.09, -16247.02) * mm});
            skLineSegment(sketch, "E410", {"start": v(14206.09, -16247.02) * mm, "end": v(14170.07, -16781.02) * mm});
            skLineSegment(sketch, "E411", {"start": v(14170.07, -16781.02) * mm, "end": v(14182.68, -17390.5) * mm});
            skLineSegment(sketch, "E412", {"start": v(14182.68, -17390.5) * mm, "end": v(14102.26, -17977.17) * mm});
            skLineSegment(sketch, "E413", {"start": v(14102.26, -17977.17) * mm, "end": v(14132.54, -18350.43) * mm});
            skLineSegment(sketch, "E414", {"start": v(14132.54, -18350.43) * mm, "end": v(14677.57, -18229.37) * mm});
            skLineSegment(sketch, "E415", {"start": v(14677.57, -18229.37) * mm, "end": v(15303.34, -18002.39) * mm});
            skLineSegment(sketch, "E416", {"start": v(15303.34, -18002.39) * mm, "end": v(15565.76, -17992.3) * mm});
            skLineSegment(sketch, "E417", {"start": v(15565.76, -17992.3) * mm, "end": v(16206.67, -17543.38) * mm});
            skLineSegment(sketch, "E418", {"start": v(16206.67, -17543.38) * mm, "end": v(16571.31, -17287.97) * mm});
            skLineSegment(sketch, "E419", {"start": v(16571.31, -17287.97) * mm, "end": v(16783.76, -16968.25) * mm});
            skLineSegment(sketch, "E420", {"start": v(16783.76, -16968.25) * mm, "end": v(17066.36, -16675.7) * mm});
            skLineSegment(sketch, "E421", {"start": v(17066.36, -16675.7) * mm, "end": v(17158.52, -16580.29) * mm});
            skLineSegment(sketch, "E422", {"start": v(17158.52, -16580.29) * mm, "end": v(17000.76, -16120.85) * mm});
            skLineSegment(sketch, "E423", {"start": v(17000.76, -16120.85) * mm, "end": v(16909.1, -15853.94) * mm});
            skLineSegment(sketch, "E424", {"start": v(16909.1, -15853.94) * mm, "end": v(16687.87, -15697.14) * mm});
            skLineSegment(sketch, "E425", {"start": v(16687.87, -15697.14) * mm, "end": v(16515.43, -15574.93) * mm});
            skLineSegment(sketch, "E426", {"start": v(16515.43, -15574.93) * mm, "end": v(16312.2, -15430.89) * mm});
            skLineSegment(sketch, "E427", {"start": v(16312.2, -15430.89) * mm, "end": v(16178.27, -15028.69) * mm});
            skLineSegment(sketch, "E428", {"start": v(16178.27, -15028.69) * mm, "end": v(16228.74, -14912.68) * mm});
            skLineSegment(sketch, "E429", {"start": v(16228.74, -14912.68) * mm, "end": v(16440.7, -14811.8) * mm});
            skLineSegment(sketch, "E430", {"start": v(16440.7, -14811.8) * mm, "end": v(16592.1, -14594.9) * mm});
            skLineSegment(sketch, "E431", {"start": v(16592.1, -14594.9) * mm, "end": v(16582, -14307.39) * mm});
            skLineSegment(sketch, "E432", {"start": v(16582, -14307.39) * mm, "end": v(16564.5, -13808.64) * mm});
            skLineSegment(sketch, "E433", {"start": v(16564.5, -13808.64) * mm, "end": v(16461.44, -12604.55) * mm});
            skLineSegment(sketch, "E434", {"start": v(16461.44, -12604.55) * mm, "end": v(16431.27, -11295.72) * mm});
            skLineSegment(sketch, "E435", {"start": v(16431.27, -11295.72) * mm, "end": v(16355.57, -10761.05) * mm});
            skLineSegment(sketch, "E436", {"start": v(16355.57, -10761.05) * mm, "end": v(16350.53, -10302.04) * mm});
            skLineSegment(sketch, "E437", {"start": v(16350.53, -10302.04) * mm, "end": v(16269.89, -9310.31) * mm});
            skLineSegment(sketch, "E438", {"start": v(16269.89, -9310.31) * mm, "end": v(16236.38, -8898.2) * mm});
            skLineSegment(sketch, "E439", {"start": v(16236.38, -8898.2) * mm, "end": v(16181.2, -8219.68) * mm});
            skLineSegment(sketch, "E440", {"start": v(16181.2, -8219.68) * mm, "end": v(16153.73, -7112.73) * mm});
            skLineSegment(sketch, "E441", {"start": v(16153.73, -7112.73) * mm, "end": v(16047.76, -6330.9) * mm});
            skLineSegment(sketch, "E442", {"start": v(16047.76, -6330.9) * mm, "end": v(15825.7, -5816.4) * mm});
            skLineSegment(sketch, "E443", {"start": v(15825.7, -5816.4) * mm, "end": v(15502.73, -5629.78) * mm});
            skLineSegment(sketch, "E444", {"start": v(15502.73, -5629.78) * mm, "end": v(15063.68, -5518.8) * mm});
            skLineSegment(sketch, "E445", {"start": v(15063.68, -5518.8) * mm, "end": v(14627.8, -5408.64) * mm});
            skLineSegment(sketch, "E446", {"start": v(14627.8, -5408.64) * mm, "end": v(14048.27, -5087.8) * mm});
            skLineSegment(sketch, "E447", {"start": v(14048.27, -5087.8) * mm, "end": v(13583.98, -4643.93) * mm});
            skLineSegment(sketch, "E448", {"start": v(13583.98, -4643.93) * mm, "end": v(13276.08, -4349.56) * mm});
            skLineSegment(sketch, "E449", {"start": v(13276.08, -4349.56) * mm, "end": v(12962, -3754.92) * mm});
            skLineSegment(sketch, "E450", {"start": v(12962, -3754.92) * mm, "end": v(12660.04, -3183.27) * mm});
            skLineSegment(sketch, "E451", {"start": v(12660.04, -3183.27) * mm, "end": v(12507.54, -2606.97) * mm});
            skLineSegment(sketch, "E452", {"start": v(12507.54, -2606.97) * mm, "end": v(12467.17, -2127.78) * mm});
            skLineSegment(sketch, "E453", {"start": v(12467.17, -2127.78) * mm, "end": v(12648.85, -1603.2) * mm});
            skLineSegment(sketch, "E454", {"start": v(12648.85, -1603.2) * mm, "end": v(12812.1, -1131.82) * mm});
            skLineSegment(sketch, "E455", {"start": v(12812.1, -1131.82) * mm, "end": v(13057.98, -142) * mm});
            skLineSegment(sketch, "E456", {"start": v(13057.98, -142) * mm, "end": v(13185.4, 370.92) * mm});
            skLineSegment(sketch, "E457", {"start": v(13185.4, 370.92) * mm, "end": v(13249.75, 1174.5) * mm});
            skLineSegment(sketch, "E458", {"start": v(13249.75, 1174.5) * mm, "end": v(13381.16, 2116.24) * mm});
            skLineSegment(sketch, "E459", {"start": v(13381.16, 2116.24) * mm, "end": v(13447.6, 2592.38) * mm});
            skLineSegment(sketch, "E460", {"start": v(13447.6, 2592.38) * mm, "end": v(13511, 3046.76) * mm});
            skLineSegment(sketch, "E461", {"start": v(13511, 3046.76) * mm, "end": v(13441.72, 3468.05) * mm});
            skLineSegment(sketch, "E462", {"start": v(13441.72, 3468.05) * mm, "end": v(13436.4, 3838.31) * mm});
            skLineSegment(sketch, "E463", {"start": v(13436.4, 3838.31) * mm, "end": v(13264.81, 4468.82) * mm});
            skLineSegment(sketch, "E464", {"start": v(13264.81, 4468.82) * mm, "end": v(12992.3, 5099.33) * mm});
            skLineSegment(sketch, "E465", {"start": v(12992.3, 5099.33) * mm, "end": v(12810.3, 5520.4) * mm});
            skLineSegment(sketch, "E466", {"start": v(12810.3, 5520.4) * mm, "end": v(12218.78, 6202.24) * mm});
            skLineSegment(sketch, "E467", {"start": v(12218.78, 6202.24) * mm, "end": v(12879.88, 6116.5) * mm});
            skLineSegment(sketch, "E468", {"start": v(12879.88, 6116.5) * mm, "end": v(13547.41, 6029.9) * mm});
            skLineSegment(sketch, "E469", {"start": v(13547.41, 6029.9) * mm, "end": v(14212.17, 5778.54) * mm});
            skLineSegment(sketch, "E470", {"start": v(14212.17, 5778.54) * mm, "end": v(14959.06, 5359.89) * mm});
            skLineSegment(sketch, "E471", {"start": v(14959.06, 5359.89) * mm, "end": v(15438.48, 4966.45) * mm});
            skLineSegment(sketch, "E472", {"start": v(15438.48, 4966.45) * mm, "end": v(16002.23, 4268.34) * mm});
            skLineSegment(sketch, "E473", {"start": v(16002.23, 4268.34) * mm, "end": v(16446.32, 3148.56) * mm});
            skLineSegment(sketch, "E474", {"start": v(16446.32, 3148.56) * mm, "end": v(16592.81, 2494.95) * mm});
            skLineSegment(sketch, "E475", {"start": v(16592.81, 2494.95) * mm, "end": v(16618.05, 1829.13) * mm});
            skLineSegment(sketch, "E476", {"start": v(16618.05, 1829.13) * mm, "end": v(16582.72, 991.82) * mm});
            skLineSegment(sketch, "E477", {"start": v(16582.72, 991.82) * mm, "end": v(16543.4, 59.67) * mm});
            skLineSegment(sketch, "E478", {"start": v(16543.4, 59.67) * mm, "end": v(16498.96, -993.51) * mm});
            skLineSegment(sketch, "E479", {"start": v(16498.96, -993.51) * mm, "end": v(16613.17, -2150.85) * mm});
            skLineSegment(sketch, "E480", {"start": v(16613.17, -2150.85) * mm, "end": v(16666.7, -2693.25) * mm});
            skLineSegment(sketch, "E481", {"start": v(16666.7, -2693.25) * mm, "end": v(17320.21, -4418.39) * mm});
            skLineSegment(sketch, "E482", {"start": v(17320.21, -4418.39) * mm, "end": v(17700.29, -5421.7) * mm});
            skLineSegment(sketch, "E483", {"start": v(17700.29, -5421.7) * mm, "end": v(18032.51, -6071.31) * mm});
            skLineSegment(sketch, "E484", {"start": v(18032.51, -6071.31) * mm, "end": v(18395.86, -6913.67) * mm});
            skLineSegment(sketch, "E485", {"start": v(18395.86, -6913.67) * mm, "end": v(18966.6, -7966.2) * mm});
            skLineSegment(sketch, "E486", {"start": v(18966.6, -7966.2) * mm, "end": v(19460.57, -8877.17) * mm});
            skLineSegment(sketch, "E487", {"start": v(19460.57, -8877.17) * mm, "end": v(20051.59, -9967.11) * mm});
            skLineSegment(sketch, "E488", {"start": v(20051.59, -9967.11) * mm, "end": v(20501.24, -10601.53) * mm});
            skLineSegment(sketch, "E489", {"start": v(20501.24, -10601.53) * mm, "end": v(21443.82, -11931.39) * mm});
            skLineSegment(sketch, "E490", {"start": v(21443.82, -11931.39) * mm, "end": v(22188.37, -12723.11) * mm});
            skLineSegment(sketch, "E491", {"start": v(22188.37, -12723.11) * mm, "end": v(23350.35, -13480.7) * mm});
            skLineSegment(sketch, "E492", {"start": v(23350.35, -13480.7) * mm, "end": v(23992.4, -13986.87) * mm});
            skLineSegment(sketch, "E493", {"start": v(23992.4, -13986.87) * mm, "end": v(25001.71, -14355.09) * mm});
            skLineSegment(sketch, "E494", {"start": v(25001.71, -14355.09) * mm, "end": v(25405.44, -14405.53) * mm});
            skLineSegment(sketch, "E495", {"start": v(25405.44, -14405.53) * mm, "end": v(25592.16, -14173.5) * mm});
            skLineSegment(sketch, "E496", {"start": v(25592.16, -14173.5) * mm, "end": v(25612.35, -13810.33) * mm});
            skLineSegment(sketch, "E497", {"start": v(25612.35, -13810.33) * mm, "end": v(25486.18, -13432.03) * mm});
            skLineSegment(sketch, "E498", {"start": v(25486.18, -13432.03) * mm, "end": v(25405.44, -12942.75) * mm});
            skLineSegment(sketch, "E499", {"start": v(25405.44, -12942.75) * mm, "end": v(25178.32, -12260.42) * mm});
            skLineSegment(sketch, "E500", {"start": v(25178.32, -12260.42) * mm, "end": v(25011.57, -11759.46) * mm});
            skLineSegment(sketch, "E501", {"start": v(25011.57, -11759.46) * mm, "end": v(24729.17, -11085.15) * mm});
            skLineSegment(sketch, "E502", {"start": v(24729.17, -11085.15) * mm, "end": v(24502.13, -10189.83) * mm});
            skLineSegment(sketch, "E503", {"start": v(24502.13, -10189.83) * mm, "end": v(24297.6, -9383.3) * mm});
            skLineSegment(sketch, "E504", {"start": v(24297.6, -9383.3) * mm, "end": v(24122.87, -8694.23) * mm});
            skLineSegment(sketch, "E505", {"start": v(24122.87, -8694.23) * mm, "end": v(24032.65, -8044.52) * mm});
            skLineSegment(sketch, "E506", {"start": v(24032.65, -8044.52) * mm, "end": v(23925.43, -7090.27) * mm});
            skLineSegment(sketch, "E507", {"start": v(23925.43, -7090.27) * mm, "end": v(23866.64, -6567.08) * mm});
            skLineSegment(sketch, "E508", {"start": v(23866.64, -6567.08) * mm, "end": v(23594.53, -5990.22) * mm});
            skLineSegment(sketch, "E509", {"start": v(23594.53, -5990.22) * mm, "end": v(23317.14, -5402.17) * mm});
            skLineSegment(sketch, "E510", {"start": v(23317.14, -5402.17) * mm, "end": v(22939.32, -4801.62) * mm});
            skLineSegment(sketch, "E511", {"start": v(22939.32, -4801.62) * mm, "end": v(22645.88, -4335.2) * mm});
            skLineSegment(sketch, "E512", {"start": v(22645.88, -4335.2) * mm, "end": v(22335.07, -3442.74) * mm});
            skLineSegment(sketch, "E513", {"start": v(22335.07, -3442.74) * mm, "end": v(22025.14, -2223.87) * mm});
            skLineSegment(sketch, "E514", {"start": v(22025.14, -2223.87) * mm, "end": v(22017.95, -1282) * mm});
            skLineSegment(sketch, "E515", {"start": v(22017.95, -1282) * mm, "end": v(22140.24, -332.95) * mm});
            skLineSegment(sketch, "E516", {"start": v(22140.24, -332.95) * mm, "end": v(22111.6, 865.58) * mm});
            skLineSegment(sketch, "E517", {"start": v(22111.6, 865.58) * mm, "end": v(22088.37, 1837.54) * mm});
            skLineSegment(sketch, "E518", {"start": v(22088.37, 1837.54) * mm, "end": v(22190.72, 2763.7) * mm});
            skLineSegment(sketch, "E519", {"start": v(22190.72, 2763.7) * mm, "end": v(22082.64, 3565.15) * mm});
            skLineSegment(sketch, "E520", {"start": v(22082.64, 3565.15) * mm, "end": v(21816.48, 4557.34) * mm});
            skLineSegment(sketch, "E521", {"start": v(21816.48, 4557.34) * mm, "end": v(21420.85, 5506.4) * mm});
            skLineSegment(sketch, "E522", {"start": v(21420.85, 5506.4) * mm, "end": v(21149.69, 6156.87) * mm});
            skLineSegment(sketch, "E523", {"start": v(21149.69, 6156.87) * mm, "end": v(20454.86, 6888.6) * mm});
            skLineSegment(sketch, "E524", {"start": v(20454.86, 6888.6) * mm, "end": v(20002.4, 7480.36) * mm});
            skLineSegment(sketch, "E525", {"start": v(20002.4, 7480.36) * mm, "end": v(19000.42, 8382.21) * mm});
            skLineSegment(sketch, "E526", {"start": v(19000.42, 8382.21) * mm, "end": v(18673.11, 8608.33) * mm});
            skLineSegment(sketch, "E527", {"start": v(18673.11, 8608.33) * mm, "end": v(18201.4, 8815.2) * mm});
            skLineSegment(sketch, "E528", {"start": v(18201.4, 8815.2) * mm, "end": v(17135.28, 9162.23) * mm});
            skLineSegment(sketch, "E529", {"start": v(17135.28, 9162.23) * mm, "end": v(16471.04, 9282.5) * mm});
            skLineSegment(sketch, "E530", {"start": v(16471.04, 9282.5) * mm, "end": v(15999.34, 9311.37) * mm});
            skLineSegment(sketch, "E531", {"start": v(15999.34, 9311.37) * mm, "end": v(14906.7, 9118.93) * mm});
            skLineSegment(sketch, "E532", {"start": v(14906.7, 9118.93) * mm, "end": v(14240.72, 8863.84) * mm});
            skLineSegment(sketch, "E533", {"start": v(14240.72, 8863.84) * mm, "end": v(13345.44, 8363.5) * mm});
            skLineSegment(sketch, "E534", {"start": v(13345.44, 8363.5) * mm, "end": v(11895.16, 7752.12) * mm});
            skLineSegment(sketch, "E535", {"start": v(11895.16, 7752.12) * mm, "end": v(11127.97, 7525.18) * mm});
            skLineSegment(sketch, "E536", {"start": v(11127.97, 7525.18) * mm, "end": v(10733.28, 7491.5) * mm});
            skLineSegment(sketch, "E537", {"start": v(10733.28, 7491.5) * mm, "end": v(10401.16, 7621.4) * mm});
            skLineSegment(sketch, "E538", {"start": v(10401.16, 7621.4) * mm, "end": v(10025.72, 7977.4) * mm});
            skLineSegment(sketch, "E539", {"start": v(10025.72, 7977.4) * mm, "end": v(9534.75, 8155.41) * mm});
            skLineSegment(sketch, "E540", {"start": v(9534.75, 8155.41) * mm, "end": v(8570.18, 8505.13) * mm});
            skLineSegment(sketch, "E541", {"start": v(8570.18, 8505.13) * mm, "end": v(7755.48, 8560.58) * mm});
            skLineSegment(sketch, "E542", {"start": v(7755.48, 8560.58) * mm, "end": v(6686.92, 8714.53) * mm});
            skLineSegment(sketch, "E543", {"start": v(6686.92, 8714.53) * mm, "end": v(5977.14, 8748.26) * mm});
            skLineSegment(sketch, "E544", {"start": v(5977.14, 8748.26) * mm, "end": v(5312.9, 8680.9) * mm});
            skLineSegment(sketch, "E545", {"start": v(5312.9, 8680.9) * mm, "end": v(4936.51, 8642.74) * mm});
            skLineSegment(sketch, "E546", {"start": v(4936.51, 8642.74) * mm, "end": v(4610.15, 8690.53) * mm});
            skLineSegment(sketch, "E547", {"start": v(4610.15, 8690.53) * mm, "end": v(4090.3, 8522.14) * mm});
            skLineSegment(sketch, "E548", {"start": v(4090.3, 8522.14) * mm, "end": v(3523.9, 8338.67) * mm});
            skLineSegment(sketch, "E549", {"start": v(3523.9, 8338.67) * mm, "end": v(2575.51, 7892.16) * mm});
            skLineSegment(sketch, "E550", {"start": v(2575.51, 7892.16) * mm, "end": v(2298.56, 7761.76) * mm});
            skLineSegment(sketch, "E551", {"start": v(2298.56, 7761.76) * mm, "end": v(1473.26, 7555.39) * mm});
            skLineSegment(sketch, "E552", {"start": v(1473.26, 7555.39) * mm, "end": v(876.4, 7492.85) * mm});
            skLineSegment(sketch, "E553", {"start": v(876.4, 7492.85) * mm, "end": v(474.95, 7371.83) * mm});
            skLineSegment(sketch, "E554", {"start": v(474.95, 7371.83) * mm, "end": v(-59.33, 7347.77) * mm});
            skLineSegment(sketch, "E555", {"start": v(-59.33, 7347.77) * mm, "end": v(-972.88, 7306.64) * mm});
            skLineSegment(sketch, "E556", {"start": v(-972.88, 7306.64) * mm, "end": v(-1370.67, 7288.73) * mm});
            skLineSegment(sketch, "E557", {"start": v(-1370.67, 7288.73) * mm, "end": v(-1818.47, 7173.77) * mm});
            skLineSegment(sketch, "E558", {"start": v(-1818.47, 7173.77) * mm, "end": v(-2319.06, 7231.5) * mm});
            skLineSegment(sketch, "E559", {"start": v(-2319.06, 7231.5) * mm, "end": v(-2833.35, 7290.81) * mm});
            skLineSegment(sketch, "E560", {"start": v(-2833.35, 7290.81) * mm, "end": v(-3556.26, 7374.18) * mm});
            skLineSegment(sketch, "E561", {"start": v(-3556.26, 7374.18) * mm, "end": v(-4217.14, 7520.35) * mm});
            skLineSegment(sketch, "E562", {"start": v(-4217.14, 7520.35) * mm, "end": v(-5165.73, 7730.14) * mm});
            skLineSegment(sketch, "E563", {"start": v(-5165.73, 7730.14) * mm, "end": v(-5691.65, 7969.2) * mm});
            skLineSegment(sketch, "E564", {"start": v(-5691.65, 7969.2) * mm, "end": v(-5999.7, 8214.57) * mm});
            skLineSegment(sketch, "E565", {"start": v(-5999.7, 8214.57) * mm, "end": v(-6365.51, 8811.12) * mm});
            skLineSegment(sketch, "E566", {"start": v(-6365.51, 8811.12) * mm, "end": v(-7084.16, 9587.68) * mm});
            skLineSegment(sketch, "E567", {"start": v(-7084.16, 9587.68) * mm, "end": v(-7888, 10357.43) * mm});
            skLineSegment(sketch, "E568", {"start": v(-7888, 10357.43) * mm, "end": v(-9270.54, 11846.29) * mm});
            skLineSegment(sketch, "E569", {"start": v(-9270.54, 11846.29) * mm, "end": v(-10138.43, 12927.19) * mm});
            skLineSegment(sketch, "E570", {"start": v(-10138.43, 12927.19) * mm, "end": v(-10703.09, 13630.44) * mm});
            skLineSegment(sketch, "E571", {"start": v(-10703.09, 13630.44) * mm, "end": v(-11197.36, 14101.06) * mm});
            skLineSegment(sketch, "E572", {"start": v(-11197.36, 14101.06) * mm, "end": v(-12855.64, 15767.6) * mm});
            skLineSegment(sketch, "E573", {"start": v(-12855.64, 15767.6) * mm, "end": v(-13266.37, 16193.15) * mm});
            skLineSegment(sketch, "E574", {"start": v(-13266.37, 16193.15) * mm, "end": v(-13641.81, 16491.43) * mm});
            skLineSegment(sketch, "E575", {"start": v(-13641.81, 16491.43) * mm, "end": v(-14310.87, 16828.2) * mm});
            skLineSegment(sketch, "E576", {"start": v(-14310.87, 16828.2) * mm, "end": v(-14825.9, 17015.82) * mm});
            skLineSegment(sketch, "E577", {"start": v(-14825.9, 17015.82) * mm, "end": v(-17013.8, 17550.37) * mm});
            skLineSegment(sketch, "E578", {"start": v(-17013.8, 17550.37) * mm, "end": v(-17966.84, 17598.48) * mm});
            skLineSegment(sketch, "E579", {"start": v(-17966.84, 17598.48) * mm, "end": v(-18763.44, 17478.02) * mm});
            skLineSegment(sketch, "E580", {"start": v(-18763.44, 17478.02) * mm, "end": v(-19543.2, 17251.9) * mm});
            skLineSegment(sketch, "E581", {"start": v(-19543.2, 17251.9) * mm, "end": v(-20462.55, 16924.76) * mm});
            skLineSegment(sketch, "E582", {"start": v(-20462.55, 16924.76) * mm, "end": v(-20850.08, 16852.32) * mm});
            skLineSegment(sketch, "E583", {"start": v(-20850.08, 16852.32) * mm, "end": v(-21101.08, 17287.2) * mm});
            skLineSegment(sketch, "E584", {"start": v(-21101.08, 17287.2) * mm, "end": v(-21490.96, 17652.84) * mm});
            skLineSegment(sketch, "E585", {"start": v(-21490.96, 17652.84) * mm, "end": v(-21957.85, 18008.85) * mm});
            skLineSegment(sketch, "E586", {"start": v(-21957.85, 18008.85) * mm, "end": v(-22549.9, 18350.43) * mm});
            skLineSegment(sketch, "E587", {"start": v(-22549.9, 18350.43) * mm, "end": v(-22593.21, 18066.58) * mm});
            skLineSegment(sketch, "E588", {"start": v(-22593.21, 18066.58) * mm, "end": v(-22554.7, 17652.84) * mm});
            skLineSegment(sketch, "E589", {"start": v(-22554.7, 17652.84) * mm, "end": v(-22444, 17099.58) * mm});
            skLineSegment(sketch, "E590", {"start": v(-22444, 17099.58) * mm, "end": v(-22140.76, 16546.32) * mm});
            skLineSegment(sketch, "E591", {"start": v(-22140.76, 16546.32) * mm, "end": v(-21915.78, 16280.24) * mm});
            skSolve(sketch);
        }
        {
            var Q0;
            Q0=makeQuery(id+"F0.imprint","IMPRINT",FACE,{"disambiguationData":[TD([[makeQuery(id+"F0.imprint","IMPRINT",EDGE,{"derivedFrom":sQuery(id+"F0.wireOp",EDGE,"E0")}),1.0]])]});
            extrude(context, id + "F1", {"entities" : qUnion([Q0]), "depth" : 25.4 * mm, "offsetDistance" : 25.4 * mm});
        }
        {
            var Q0;
            Q0=makeQuery(id+"F1.opExtrude","SWEPT_BODY",BODY,{"disambiguationData":[OSD([sQuery(id+"F0.wireOp",EDGE,"E0"),sQuery(id+"F0.wireOp",EDGE,"E1"),sQuery(id+"F0.wireOp",EDGE,"E2"),sQuery(id+"F0.wireOp",EDGE,"E3"),sQuery(id+"F0.wireOp",EDGE,"E4"),sQuery(id+"F0.wireOp",EDGE,"E5"),sQuery(id+"F0.wireOp",EDGE,"E6"),sQuery(id+"F0.wireOp",EDGE,"E7"),sQuery(id+"F0.wireOp",EDGE,"E8"),sQuery(id+"F0.wireOp",EDGE,"E9"),sQuery(id+"F0.wireOp",EDGE,"E10"),sQuery(id+"F0.wireOp",EDGE,"E11"),sQuery(id+"F0.wireOp",EDGE,"E12"),sQuery(id+"F0.wireOp",EDGE,"E13"),sQuery(id+"F0.wireOp",EDGE,"E14"),sQuery(id+"F0.wireOp",EDGE,"E15"),sQuery(id+"F0.wireOp",EDGE,"E16"),sQuery(id+"F0.wireOp",EDGE,"E17"),sQuery(id+"F0.wireOp",EDGE,"E18"),sQuery(id+"F0.wireOp",EDGE,"E19"),sQuery(id+"F0.wireOp",EDGE,"E20"),sQuery(id+"F0.wireOp",EDGE,"E21"),sQuery(id+"F0.wireOp",EDGE,"E22"),sQuery(id+"F0.wireOp",EDGE,"E23"),sQuery(id+"F0.wireOp",EDGE,"E24"),sQuery(id+"F0.wireOp",EDGE,"E25"),sQuery(id+"F0.wireOp",EDGE,"E26"),sQuery(id+"F0.wireOp",EDGE,"E27"),sQuery(id+"F0.wireOp",EDGE,"E28"),sQuery(id+"F0.wireOp",EDGE,"E29"),sQuery(id+"F0.wireOp",EDGE,"E30"),sQuery(id+"F0.wireOp",EDGE,"E31"),sQuery(id+"F0.wireOp",EDGE,"E32"),sQuery(id+"F0.wireOp",EDGE,"E33"),sQuery(id+"F0.wireOp",EDGE,"E34"),sQuery(id+"F0.wireOp",EDGE,"E35"),sQuery(id+"F0.wireOp",EDGE,"E36"),sQuery(id+"F0.wireOp",EDGE,"E37"),sQuery(id+"F0.wireOp",EDGE,"E38"),sQuery(id+"F0.wireOp",EDGE,"E39"),sQuery(id+"F0.wireOp",EDGE,"E40"),sQuery(id+"F0.wireOp",EDGE,"E41"),sQuery(id+"F0.wireOp",EDGE,"E42"),sQuery(id+"F0.wireOp",EDGE,"E43"),sQuery(id+"F0.wireOp",EDGE,"E44"),sQuery(id+"F0.wireOp",EDGE,"E45"),sQuery(id+"F0.wireOp",EDGE,"E46"),sQuery(id+"F0.wireOp",EDGE,"E47"),sQuery(id+"F0.wireOp",EDGE,"E48"),sQuery(id+"F0.wireOp",EDGE,"E49"),sQuery(id+"F0.wireOp",EDGE,"E50"),sQuery(id+"F0.wireOp",EDGE,"E51"),sQuery(id+"F0.wireOp",EDGE,"E52"),sQuery(id+"F0.wireOp",EDGE,"E53"),sQuery(id+"F0.wireOp",EDGE,"E54"),sQuery(id+"F0.wireOp",EDGE,"E55"),sQuery(id+"F0.wireOp",EDGE,"E56"),sQuery(id+"F0.wireOp",EDGE,"E57"),sQuery(id+"F0.wireOp",EDGE,"E58"),sQuery(id+"F0.wireOp",EDGE,"E59"),sQuery(id+"F0.wireOp",EDGE,"E60"),sQuery(id+"F0.wireOp",EDGE,"E61"),sQuery(id+"F0.wireOp",EDGE,"E62"),sQuery(id+"F0.wireOp",EDGE,"E63"),sQuery(id+"F0.wireOp",EDGE,"E64"),sQuery(id+"F0.wireOp",EDGE,"E65"),sQuery(id+"F0.wireOp",EDGE,"E66"),sQuery(id+"F0.wireOp",EDGE,"E67"),sQuery(id+"F0.wireOp",EDGE,"E68"),sQuery(id+"F0.wireOp",EDGE,"E69"),sQuery(id+"F0.wireOp",EDGE,"E70"),sQuery(id+"F0.wireOp",EDGE,"E71"),sQuery(id+"F0.wireOp",EDGE,"E72"),sQuery(id+"F0.wireOp",EDGE,"E73"),sQuery(id+"F0.wireOp",EDGE,"E74"),sQuery(id+"F0.wireOp",EDGE,"E75"),sQuery(id+"F0.wireOp",EDGE,"E76"),sQuery(id+"F0.wireOp",EDGE,"E77"),sQuery(id+"F0.wireOp",EDGE,"E78"),sQuery(id+"F0.wireOp",EDGE,"E79"),sQuery(id+"F0.wireOp",EDGE,"E80"),sQuery(id+"F0.wireOp",EDGE,"E81"),sQuery(id+"F0.wireOp",EDGE,"E82"),sQuery(id+"F0.wireOp",EDGE,"E83"),sQuery(id+"F0.wireOp",EDGE,"E84"),sQuery(id+"F0.wireOp",EDGE,"E85"),sQuery(id+"F0.wireOp",EDGE,"E86"),sQuery(id+"F0.wireOp",EDGE,"E87"),sQuery(id+"F0.wireOp",EDGE,"E88"),sQuery(id+"F0.wireOp",EDGE,"E89"),sQuery(id+"F0.wireOp",EDGE,"E90"),sQuery(id+"F0.wireOp",EDGE,"E91"),sQuery(id+"F0.wireOp",EDGE,"E92"),sQuery(id+"F0.wireOp",EDGE,"E93"),sQuery(id+"F0.wireOp",EDGE,"E94"),sQuery(id+"F0.wireOp",EDGE,"E95"),sQuery(id+"F0.wireOp",EDGE,"E96"),sQuery(id+"F0.wireOp",EDGE,"E97"),sQuery(id+"F0.wireOp",EDGE,"E98"),sQuery(id+"F0.wireOp",EDGE,"E99"),sQuery(id+"F0.wireOp",EDGE,"E100"),sQuery(id+"F0.wireOp",EDGE,"E101"),sQuery(id+"F0.wireOp",EDGE,"E102"),sQuery(id+"F0.wireOp",EDGE,"E103"),sQuery(id+"F0.wireOp",EDGE,"E104"),sQuery(id+"F0.wireOp",EDGE,"E105"),sQuery(id+"F0.wireOp",EDGE,"E106"),sQuery(id+"F0.wireOp",EDGE,"E107"),sQuery(id+"F0.wireOp",EDGE,"E108"),sQuery(id+"F0.wireOp",EDGE,"E109"),sQuery(id+"F0.wireOp",EDGE,"E110"),sQuery(id+"F0.wireOp",EDGE,"E111"),sQuery(id+"F0.wireOp",EDGE,"E112"),sQuery(id+"F0.wireOp",EDGE,"E113"),sQuery(id+"F0.wireOp",EDGE,"E114"),sQuery(id+"F0.wireOp",EDGE,"E115"),sQuery(id+"F0.wireOp",EDGE,"E116"),sQuery(id+"F0.wireOp",EDGE,"E117"),sQuery(id+"F0.wireOp",EDGE,"E118"),sQuery(id+"F0.wireOp",EDGE,"E119"),sQuery(id+"F0.wireOp",EDGE,"E120"),sQuery(id+"F0.wireOp",EDGE,"E121"),sQuery(id+"F0.wireOp",EDGE,"E122"),sQuery(id+"F0.wireOp",EDGE,"E123"),sQuery(id+"F0.wireOp",EDGE,"E124"),sQuery(id+"F0.wireOp",EDGE,"E125"),sQuery(id+"F0.wireOp",EDGE,"E126"),sQuery(id+"F0.wireOp",EDGE,"E127"),sQuery(id+"F0.wireOp",EDGE,"E128"),sQuery(id+"F0.wireOp",EDGE,"E129"),sQuery(id+"F0.wireOp",EDGE,"E130"),sQuery(id+"F0.wireOp",EDGE,"E131"),sQuery(id+"F0.wireOp",EDGE,"E132"),sQuery(id+"F0.wireOp",EDGE,"E133"),sQuery(id+"F0.wireOp",EDGE,"E134"),sQuery(id+"F0.wireOp",EDGE,"E135"),sQuery(id+"F0.wireOp",EDGE,"E136"),sQuery(id+"F0.wireOp",EDGE,"E137"),sQuery(id+"F0.wireOp",EDGE,"E138"),sQuery(id+"F0.wireOp",EDGE,"E139"),sQuery(id+"F0.wireOp",EDGE,"E140"),sQuery(id+"F0.wireOp",EDGE,"E141"),sQuery(id+"F0.wireOp",EDGE,"E142"),sQuery(id+"F0.wireOp",EDGE,"E143"),sQuery(id+"F0.wireOp",EDGE,"E144"),sQuery(id+"F0.wireOp",EDGE,"E145"),sQuery(id+"F0.wireOp",EDGE,"E146"),sQuery(id+"F0.wireOp",EDGE,"E147"),sQuery(id+"F0.wireOp",EDGE,"E148"),sQuery(id+"F0.wireOp",EDGE,"E149"),sQuery(id+"F0.wireOp",EDGE,"E150"),sQuery(id+"F0.wireOp",EDGE,"E151"),sQuery(id+"F0.wireOp",EDGE,"E152"),sQuery(id+"F0.wireOp",EDGE,"E153"),sQuery(id+"F0.wireOp",EDGE,"E154"),sQuery(id+"F0.wireOp",EDGE,"E155"),sQuery(id+"F0.wireOp",EDGE,"E156"),sQuery(id+"F0.wireOp",EDGE,"E157"),sQuery(id+"F0.wireOp",EDGE,"E158"),sQuery(id+"F0.wireOp",EDGE,"E159"),sQuery(id+"F0.wireOp",EDGE,"E160"),sQuery(id+"F0.wireOp",EDGE,"E161"),sQuery(id+"F0.wireOp",EDGE,"E162"),sQuery(id+"F0.wireOp",EDGE,"E163"),sQuery(id+"F0.wireOp",EDGE,"E164"),sQuery(id+"F0.wireOp",EDGE,"E165"),sQuery(id+"F0.wireOp",EDGE,"E166"),sQuery(id+"F0.wireOp",EDGE,"E167"),sQuery(id+"F0.wireOp",EDGE,"E168"),sQuery(id+"F0.wireOp",EDGE,"E169"),sQuery(id+"F0.wireOp",EDGE,"E170"),sQuery(id+"F0.wireOp",EDGE,"E171"),sQuery(id+"F0.wireOp",EDGE,"E172"),sQuery(id+"F0.wireOp",EDGE,"E173"),sQuery(id+"F0.wireOp",EDGE,"E174"),sQuery(id+"F0.wireOp",EDGE,"E175"),sQuery(id+"F0.wireOp",EDGE,"E176"),sQuery(id+"F0.wireOp",EDGE,"E177"),sQuery(id+"F0.wireOp",EDGE,"E178"),sQuery(id+"F0.wireOp",EDGE,"E179"),sQuery(id+"F0.wireOp",EDGE,"E180"),sQuery(id+"F0.wireOp",EDGE,"E181"),sQuery(id+"F0.wireOp",EDGE,"E182"),sQuery(id+"F0.wireOp",EDGE,"E183"),sQuery(id+"F0.wireOp",EDGE,"E184"),sQuery(id+"F0.wireOp",EDGE,"E185"),sQuery(id+"F0.wireOp",EDGE,"E186"),sQuery(id+"F0.wireOp",EDGE,"E187"),sQuery(id+"F0.wireOp",EDGE,"E188"),sQuery(id+"F0.wireOp",EDGE,"E189"),sQuery(id+"F0.wireOp",EDGE,"E190"),sQuery(id+"F0.wireOp",EDGE,"E191"),sQuery(id+"F0.wireOp",EDGE,"E192"),sQuery(id+"F0.wireOp",EDGE,"E193"),sQuery(id+"F0.wireOp",EDGE,"E194"),sQuery(id+"F0.wireOp",EDGE,"E195"),sQuery(id+"F0.wireOp",EDGE,"E196"),sQuery(id+"F0.wireOp",EDGE,"E197"),sQuery(id+"F0.wireOp",EDGE,"E198"),sQuery(id+"F0.wireOp",EDGE,"E199"),sQuery(id+"F0.wireOp",EDGE,"E200"),sQuery(id+"F0.wireOp",EDGE,"E201"),sQuery(id+"F0.wireOp",EDGE,"E202"),sQuery(id+"F0.wireOp",EDGE,"E203"),sQuery(id+"F0.wireOp",EDGE,"E204"),sQuery(id+"F0.wireOp",EDGE,"E205"),sQuery(id+"F0.wireOp",EDGE,"E206"),sQuery(id+"F0.wireOp",EDGE,"E207"),sQuery(id+"F0.wireOp",EDGE,"E208"),sQuery(id+"F0.wireOp",EDGE,"E209"),sQuery(id+"F0.wireOp",EDGE,"E210"),sQuery(id+"F0.wireOp",EDGE,"E211"),sQuery(id+"F0.wireOp",EDGE,"E212"),sQuery(id+"F0.wireOp",EDGE,"E213"),sQuery(id+"F0.wireOp",EDGE,"E214"),sQuery(id+"F0.wireOp",EDGE,"E215"),sQuery(id+"F0.wireOp",EDGE,"E216"),sQuery(id+"F0.wireOp",EDGE,"E217"),sQuery(id+"F0.wireOp",EDGE,"E218"),sQuery(id+"F0.wireOp",EDGE,"E219"),sQuery(id+"F0.wireOp",EDGE,"E220"),sQuery(id+"F0.wireOp",EDGE,"E221"),sQuery(id+"F0.wireOp",EDGE,"E222"),sQuery(id+"F0.wireOp",EDGE,"E223"),sQuery(id+"F0.wireOp",EDGE,"E224"),sQuery(id+"F0.wireOp",EDGE,"E225"),sQuery(id+"F0.wireOp",EDGE,"E226"),sQuery(id+"F0.wireOp",EDGE,"E227"),sQuery(id+"F0.wireOp",EDGE,"E228"),sQuery(id+"F0.wireOp",EDGE,"E229"),sQuery(id+"F0.wireOp",EDGE,"E230"),sQuery(id+"F0.wireOp",EDGE,"E231"),sQuery(id+"F0.wireOp",EDGE,"E232"),sQuery(id+"F0.wireOp",EDGE,"E233"),sQuery(id+"F0.wireOp",EDGE,"E234"),sQuery(id+"F0.wireOp",EDGE,"E235"),sQuery(id+"F0.wireOp",EDGE,"E236"),sQuery(id+"F0.wireOp",EDGE,"E237"),sQuery(id+"F0.wireOp",EDGE,"E238"),sQuery(id+"F0.wireOp",EDGE,"E239"),sQuery(id+"F0.wireOp",EDGE,"E240"),sQuery(id+"F0.wireOp",EDGE,"E241"),sQuery(id+"F0.wireOp",EDGE,"E242"),sQuery(id+"F0.wireOp",EDGE,"E243"),sQuery(id+"F0.wireOp",EDGE,"E244"),sQuery(id+"F0.wireOp",EDGE,"E245"),sQuery(id+"F0.wireOp",EDGE,"E246"),sQuery(id+"F0.wireOp",EDGE,"E247"),sQuery(id+"F0.wireOp",EDGE,"E248"),sQuery(id+"F0.wireOp",EDGE,"E249"),sQuery(id+"F0.wireOp",EDGE,"E250"),sQuery(id+"F0.wireOp",EDGE,"E251"),sQuery(id+"F0.wireOp",EDGE,"E252"),sQuery(id+"F0.wireOp",EDGE,"E253"),sQuery(id+"F0.wireOp",EDGE,"E254"),sQuery(id+"F0.wireOp",EDGE,"E255"),sQuery(id+"F0.wireOp",EDGE,"E256"),sQuery(id+"F0.wireOp",EDGE,"E257"),sQuery(id+"F0.wireOp",EDGE,"E258"),sQuery(id+"F0.wireOp",EDGE,"E259"),sQuery(id+"F0.wireOp",EDGE,"E260"),sQuery(id+"F0.wireOp",EDGE,"E261"),sQuery(id+"F0.wireOp",EDGE,"E262"),sQuery(id+"F0.wireOp",EDGE,"E263"),sQuery(id+"F0.wireOp",EDGE,"E264"),sQuery(id+"F0.wireOp",EDGE,"E265"),sQuery(id+"F0.wireOp",EDGE,"E266"),sQuery(id+"F0.wireOp",EDGE,"E267"),sQuery(id+"F0.wireOp",EDGE,"E268"),sQuery(id+"F0.wireOp",EDGE,"E269"),sQuery(id+"F0.wireOp",EDGE,"E270"),sQuery(id+"F0.wireOp",EDGE,"E271"),sQuery(id+"F0.wireOp",EDGE,"E272"),sQuery(id+"F0.wireOp",EDGE,"E273"),sQuery(id+"F0.wireOp",EDGE,"E274"),sQuery(id+"F0.wireOp",EDGE,"E275"),sQuery(id+"F0.wireOp",EDGE,"E276"),sQuery(id+"F0.wireOp",EDGE,"E277"),sQuery(id+"F0.wireOp",EDGE,"E278"),sQuery(id+"F0.wireOp",EDGE,"E279"),sQuery(id+"F0.wireOp",EDGE,"E280"),sQuery(id+"F0.wireOp",EDGE,"E281"),sQuery(id+"F0.wireOp",EDGE,"E282"),sQuery(id+"F0.wireOp",EDGE,"E283"),sQuery(id+"F0.wireOp",EDGE,"E284"),sQuery(id+"F0.wireOp",EDGE,"E285"),sQuery(id+"F0.wireOp",EDGE,"E286"),sQuery(id+"F0.wireOp",EDGE,"E287"),sQuery(id+"F0.wireOp",EDGE,"E288"),sQuery(id+"F0.wireOp",EDGE,"E289"),sQuery(id+"F0.wireOp",EDGE,"E290"),sQuery(id+"F0.wireOp",EDGE,"E291"),sQuery(id+"F0.wireOp",EDGE,"E292"),sQuery(id+"F0.wireOp",EDGE,"E293"),sQuery(id+"F0.wireOp",EDGE,"E294"),sQuery(id+"F0.wireOp",EDGE,"E295"),sQuery(id+"F0.wireOp",EDGE,"E296"),sQuery(id+"F0.wireOp",EDGE,"E297"),sQuery(id+"F0.wireOp",EDGE,"E298"),sQuery(id+"F0.wireOp",EDGE,"E299"),sQuery(id+"F0.wireOp",EDGE,"E300"),sQuery(id+"F0.wireOp",EDGE,"E301"),sQuery(id+"F0.wireOp",EDGE,"E302"),sQuery(id+"F0.wireOp",EDGE,"E303"),sQuery(id+"F0.wireOp",EDGE,"E304"),sQuery(id+"F0.wireOp",EDGE,"E305"),sQuery(id+"F0.wireOp",EDGE,"E306"),sQuery(id+"F0.wireOp",EDGE,"E307"),sQuery(id+"F0.wireOp",EDGE,"E308"),sQuery(id+"F0.wireOp",EDGE,"E309"),sQuery(id+"F0.wireOp",EDGE,"E310"),sQuery(id+"F0.wireOp",EDGE,"E311"),sQuery(id+"F0.wireOp",EDGE,"E312"),sQuery(id+"F0.wireOp",EDGE,"E313"),sQuery(id+"F0.wireOp",EDGE,"E314"),sQuery(id+"F0.wireOp",EDGE,"E315"),sQuery(id+"F0.wireOp",EDGE,"E316"),sQuery(id+"F0.wireOp",EDGE,"E317"),sQuery(id+"F0.wireOp",EDGE,"E318"),sQuery(id+"F0.wireOp",EDGE,"E319"),sQuery(id+"F0.wireOp",EDGE,"E320"),sQuery(id+"F0.wireOp",EDGE,"E321"),sQuery(id+"F0.wireOp",EDGE,"E322"),sQuery(id+"F0.wireOp",EDGE,"E323"),sQuery(id+"F0.wireOp",EDGE,"E324"),sQuery(id+"F0.wireOp",EDGE,"E325"),sQuery(id+"F0.wireOp",EDGE,"E326"),sQuery(id+"F0.wireOp",EDGE,"E327"),sQuery(id+"F0.wireOp",EDGE,"E328"),sQuery(id+"F0.wireOp",EDGE,"E329"),sQuery(id+"F0.wireOp",EDGE,"E330"),sQuery(id+"F0.wireOp",EDGE,"E331"),sQuery(id+"F0.wireOp",EDGE,"E332"),sQuery(id+"F0.wireOp",EDGE,"E333"),sQuery(id+"F0.wireOp",EDGE,"E334"),sQuery(id+"F0.wireOp",EDGE,"E335"),sQuery(id+"F0.wireOp",EDGE,"E336"),sQuery(id+"F0.wireOp",EDGE,"E337"),sQuery(id+"F0.wireOp",EDGE,"E338"),sQuery(id+"F0.wireOp",EDGE,"E339"),sQuery(id+"F0.wireOp",EDGE,"E340"),sQuery(id+"F0.wireOp",EDGE,"E341"),sQuery(id+"F0.wireOp",EDGE,"E342"),sQuery(id+"F0.wireOp",EDGE,"E343"),sQuery(id+"F0.wireOp",EDGE,"E344"),sQuery(id+"F0.wireOp",EDGE,"E345"),sQuery(id+"F0.wireOp",EDGE,"E346"),sQuery(id+"F0.wireOp",EDGE,"E347"),sQuery(id+"F0.wireOp",EDGE,"E348"),sQuery(id+"F0.wireOp",EDGE,"E349"),sQuery(id+"F0.wireOp",EDGE,"E350"),sQuery(id+"F0.wireOp",EDGE,"E351"),sQuery(id+"F0.wireOp",EDGE,"E352"),sQuery(id+"F0.wireOp",EDGE,"E353"),sQuery(id+"F0.wireOp",EDGE,"E354"),sQuery(id+"F0.wireOp",EDGE,"E355"),sQuery(id+"F0.wireOp",EDGE,"E356"),sQuery(id+"F0.wireOp",EDGE,"E357"),sQuery(id+"F0.wireOp",EDGE,"E358"),sQuery(id+"F0.wireOp",EDGE,"E359"),sQuery(id+"F0.wireOp",EDGE,"E360"),sQuery(id+"F0.wireOp",EDGE,"E361"),sQuery(id+"F0.wireOp",EDGE,"E362"),sQuery(id+"F0.wireOp",EDGE,"E363"),sQuery(id+"F0.wireOp",EDGE,"E364"),sQuery(id+"F0.wireOp",EDGE,"E365"),sQuery(id+"F0.wireOp",EDGE,"E366"),sQuery(id+"F0.wireOp",EDGE,"E367"),sQuery(id+"F0.wireOp",EDGE,"E368"),sQuery(id+"F0.wireOp",EDGE,"E369"),sQuery(id+"F0.wireOp",EDGE,"E370"),sQuery(id+"F0.wireOp",EDGE,"E371"),sQuery(id+"F0.wireOp",EDGE,"E372"),sQuery(id+"F0.wireOp",EDGE,"E373"),sQuery(id+"F0.wireOp",EDGE,"E374"),sQuery(id+"F0.wireOp",EDGE,"E375"),sQuery(id+"F0.wireOp",EDGE,"E376"),sQuery(id+"F0.wireOp",EDGE,"E377"),sQuery(id+"F0.wireOp",EDGE,"E378"),sQuery(id+"F0.wireOp",EDGE,"E379"),sQuery(id+"F0.wireOp",EDGE,"E380"),sQuery(id+"F0.wireOp",EDGE,"E381"),sQuery(id+"F0.wireOp",EDGE,"E382"),sQuery(id+"F0.wireOp",EDGE,"E383"),sQuery(id+"F0.wireOp",EDGE,"E384"),sQuery(id+"F0.wireOp",EDGE,"E385"),sQuery(id+"F0.wireOp",EDGE,"E386"),sQuery(id+"F0.wireOp",EDGE,"E387"),sQuery(id+"F0.wireOp",EDGE,"E388"),sQuery(id+"F0.wireOp",EDGE,"E389"),sQuery(id+"F0.wireOp",EDGE,"E390"),sQuery(id+"F0.wireOp",EDGE,"E391"),sQuery(id+"F0.wireOp",EDGE,"E392"),sQuery(id+"F0.wireOp",EDGE,"E393"),sQuery(id+"F0.wireOp",EDGE,"E394"),sQuery(id+"F0.wireOp",EDGE,"E395"),sQuery(id+"F0.wireOp",EDGE,"E396"),sQuery(id+"F0.wireOp",EDGE,"E397"),sQuery(id+"F0.wireOp",EDGE,"E398"),sQuery(id+"F0.wireOp",EDGE,"E399"),sQuery(id+"F0.wireOp",EDGE,"E400"),sQuery(id+"F0.wireOp",EDGE,"E401"),sQuery(id+"F0.wireOp",EDGE,"E402"),sQuery(id+"F0.wireOp",EDGE,"E403"),sQuery(id+"F0.wireOp",EDGE,"E404"),sQuery(id+"F0.wireOp",EDGE,"E405"),sQuery(id+"F0.wireOp",EDGE,"E406"),sQuery(id+"F0.wireOp",EDGE,"E407"),sQuery(id+"F0.wireOp",EDGE,"E408"),sQuery(id+"F0.wireOp",EDGE,"E409"),sQuery(id+"F0.wireOp",EDGE,"E410"),sQuery(id+"F0.wireOp",EDGE,"E411"),sQuery(id+"F0.wireOp",EDGE,"E412"),sQuery(id+"F0.wireOp",EDGE,"E413"),sQuery(id+"F0.wireOp",EDGE,"E414"),sQuery(id+"F0.wireOp",EDGE,"E415"),sQuery(id+"F0.wireOp",EDGE,"E416"),sQuery(id+"F0.wireOp",EDGE,"E417"),sQuery(id+"F0.wireOp",EDGE,"E418"),sQuery(id+"F0.wireOp",EDGE,"E419"),sQuery(id+"F0.wireOp",EDGE,"E420"),sQuery(id+"F0.wireOp",EDGE,"E421"),sQuery(id+"F0.wireOp",EDGE,"E422"),sQuery(id+"F0.wireOp",EDGE,"E423"),sQuery(id+"F0.wireOp",EDGE,"E424"),sQuery(id+"F0.wireOp",EDGE,"E425"),sQuery(id+"F0.wireOp",EDGE,"E426"),sQuery(id+"F0.wireOp",EDGE,"E427"),sQuery(id+"F0.wireOp",EDGE,"E428"),sQuery(id+"F0.wireOp",EDGE,"E429"),sQuery(id+"F0.wireOp",EDGE,"E430"),sQuery(id+"F0.wireOp",EDGE,"E431"),sQuery(id+"F0.wireOp",EDGE,"E432"),sQuery(id+"F0.wireOp",EDGE,"E433"),sQuery(id+"F0.wireOp",EDGE,"E434"),sQuery(id+"F0.wireOp",EDGE,"E435"),sQuery(id+"F0.wireOp",EDGE,"E436"),sQuery(id+"F0.wireOp",EDGE,"E437"),sQuery(id+"F0.wireOp",EDGE,"E438"),sQuery(id+"F0.wireOp",EDGE,"E439"),sQuery(id+"F0.wireOp",EDGE,"E440"),sQuery(id+"F0.wireOp",EDGE,"E441"),sQuery(id+"F0.wireOp",EDGE,"E442"),sQuery(id+"F0.wireOp",EDGE,"E443"),sQuery(id+"F0.wireOp",EDGE,"E444"),sQuery(id+"F0.wireOp",EDGE,"E445"),sQuery(id+"F0.wireOp",EDGE,"E446"),sQuery(id+"F0.wireOp",EDGE,"E447"),sQuery(id+"F0.wireOp",EDGE,"E448"),sQuery(id+"F0.wireOp",EDGE,"E449"),sQuery(id+"F0.wireOp",EDGE,"E450"),sQuery(id+"F0.wireOp",EDGE,"E451"),sQuery(id+"F0.wireOp",EDGE,"E452"),sQuery(id+"F0.wireOp",EDGE,"E453"),sQuery(id+"F0.wireOp",EDGE,"E454"),sQuery(id+"F0.wireOp",EDGE,"E455"),sQuery(id+"F0.wireOp",EDGE,"E456"),sQuery(id+"F0.wireOp",EDGE,"E457"),sQuery(id+"F0.wireOp",EDGE,"E458"),sQuery(id+"F0.wireOp",EDGE,"E459"),sQuery(id+"F0.wireOp",EDGE,"E460"),sQuery(id+"F0.wireOp",EDGE,"E461"),sQuery(id+"F0.wireOp",EDGE,"E462"),sQuery(id+"F0.wireOp",EDGE,"E463"),sQuery(id+"F0.wireOp",EDGE,"E464"),sQuery(id+"F0.wireOp",EDGE,"E465"),sQuery(id+"F0.wireOp",EDGE,"E466"),sQuery(id+"F0.wireOp",EDGE,"E467"),sQuery(id+"F0.wireOp",EDGE,"E468"),sQuery(id+"F0.wireOp",EDGE,"E469"),sQuery(id+"F0.wireOp",EDGE,"E470"),sQuery(id+"F0.wireOp",EDGE,"E471"),sQuery(id+"F0.wireOp",EDGE,"E472"),sQuery(id+"F0.wireOp",EDGE,"E473"),sQuery(id+"F0.wireOp",EDGE,"E474"),sQuery(id+"F0.wireOp",EDGE,"E475"),sQuery(id+"F0.wireOp",EDGE,"E476"),sQuery(id+"F0.wireOp",EDGE,"E477"),sQuery(id+"F0.wireOp",EDGE,"E478"),sQuery(id+"F0.wireOp",EDGE,"E479"),sQuery(id+"F0.wireOp",EDGE,"E480"),sQuery(id+"F0.wireOp",EDGE,"E481"),sQuery(id+"F0.wireOp",EDGE,"E482"),sQuery(id+"F0.wireOp",EDGE,"E483"),sQuery(id+"F0.wireOp",EDGE,"E484"),sQuery(id+"F0.wireOp",EDGE,"E485"),sQuery(id+"F0.wireOp",EDGE,"E486"),sQuery(id+"F0.wireOp",EDGE,"E487"),sQuery(id+"F0.wireOp",EDGE,"E488"),sQuery(id+"F0.wireOp",EDGE,"E489"),sQuery(id+"F0.wireOp",EDGE,"E490"),sQuery(id+"F0.wireOp",EDGE,"E491"),sQuery(id+"F0.wireOp",EDGE,"E492"),sQuery(id+"F0.wireOp",EDGE,"E493"),sQuery(id+"F0.wireOp",EDGE,"E494"),sQuery(id+"F0.wireOp",EDGE,"E495"),sQuery(id+"F0.wireOp",EDGE,"E496"),sQuery(id+"F0.wireOp",EDGE,"E497"),sQuery(id+"F0.wireOp",EDGE,"E498"),sQuery(id+"F0.wireOp",EDGE,"E499"),sQuery(id+"F0.wireOp",EDGE,"E500"),sQuery(id+"F0.wireOp",EDGE,"E501"),sQuery(id+"F0.wireOp",EDGE,"E502"),sQuery(id+"F0.wireOp",EDGE,"E503"),sQuery(id+"F0.wireOp",EDGE,"E504"),sQuery(id+"F0.wireOp",EDGE,"E505"),sQuery(id+"F0.wireOp",EDGE,"E506"),sQuery(id+"F0.wireOp",EDGE,"E507"),sQuery(id+"F0.wireOp",EDGE,"E508"),sQuery(id+"F0.wireOp",EDGE,"E509"),sQuery(id+"F0.wireOp",EDGE,"E510"),sQuery(id+"F0.wireOp",EDGE,"E511"),sQuery(id+"F0.wireOp",EDGE,"E512"),sQuery(id+"F0.wireOp",EDGE,"E513"),sQuery(id+"F0.wireOp",EDGE,"E514"),sQuery(id+"F0.wireOp",EDGE,"E515"),sQuery(id+"F0.wireOp",EDGE,"E516"),sQuery(id+"F0.wireOp",EDGE,"E517"),sQuery(id+"F0.wireOp",EDGE,"E518"),sQuery(id+"F0.wireOp",EDGE,"E519"),sQuery(id+"F0.wireOp",EDGE,"E520"),sQuery(id+"F0.wireOp",EDGE,"E521"),sQuery(id+"F0.wireOp",EDGE,"E522"),sQuery(id+"F0.wireOp",EDGE,"E523"),sQuery(id+"F0.wireOp",EDGE,"E524"),sQuery(id+"F0.wireOp",EDGE,"E525"),sQuery(id+"F0.wireOp",EDGE,"E526"),sQuery(id+"F0.wireOp",EDGE,"E527"),sQuery(id+"F0.wireOp",EDGE,"E528"),sQuery(id+"F0.wireOp",EDGE,"E529"),sQuery(id+"F0.wireOp",EDGE,"E530"),sQuery(id+"F0.wireOp",EDGE,"E531"),sQuery(id+"F0.wireOp",EDGE,"E532"),sQuery(id+"F0.wireOp",EDGE,"E533"),sQuery(id+"F0.wireOp",EDGE,"E534"),sQuery(id+"F0.wireOp",EDGE,"E535"),sQuery(id+"F0.wireOp",EDGE,"E536"),sQuery(id+"F0.wireOp",EDGE,"E537"),sQuery(id+"F0.wireOp",EDGE,"E538"),sQuery(id+"F0.wireOp",EDGE,"E539"),sQuery(id+"F0.wireOp",EDGE,"E540"),sQuery(id+"F0.wireOp",EDGE,"E541"),sQuery(id+"F0.wireOp",EDGE,"E542"),sQuery(id+"F0.wireOp",EDGE,"E543"),sQuery(id+"F0.wireOp",EDGE,"E544"),sQuery(id+"F0.wireOp",EDGE,"E545"),sQuery(id+"F0.wireOp",EDGE,"E546"),sQuery(id+"F0.wireOp",EDGE,"E547"),sQuery(id+"F0.wireOp",EDGE,"E548"),sQuery(id+"F0.wireOp",EDGE,"E549"),sQuery(id+"F0.wireOp",EDGE,"E550"),sQuery(id+"F0.wireOp",EDGE,"E551"),sQuery(id+"F0.wireOp",EDGE,"E552"),sQuery(id+"F0.wireOp",EDGE,"E553"),sQuery(id+"F0.wireOp",EDGE,"E554"),sQuery(id+"F0.wireOp",EDGE,"E555"),sQuery(id+"F0.wireOp",EDGE,"E556"),sQuery(id+"F0.wireOp",EDGE,"E557"),sQuery(id+"F0.wireOp",EDGE,"E558"),sQuery(id+"F0.wireOp",EDGE,"E559"),sQuery(id+"F0.wireOp",EDGE,"E560"),sQuery(id+"F0.wireOp",EDGE,"E561"),sQuery(id+"F0.wireOp",EDGE,"E562"),sQuery(id+"F0.wireOp",EDGE,"E563"),sQuery(id+"F0.wireOp",EDGE,"E564"),sQuery(id+"F0.wireOp",EDGE,"E565"),sQuery(id+"F0.wireOp",EDGE,"E566"),sQuery(id+"F0.wireOp",EDGE,"E567"),sQuery(id+"F0.wireOp",EDGE,"E568"),sQuery(id+"F0.wireOp",EDGE,"E569"),sQuery(id+"F0.wireOp",EDGE,"E570"),sQuery(id+"F0.wireOp",EDGE,"E571"),sQuery(id+"F0.wireOp",EDGE,"E572"),sQuery(id+"F0.wireOp",EDGE,"E573"),sQuery(id+"F0.wireOp",EDGE,"E574"),sQuery(id+"F0.wireOp",EDGE,"E575"),sQuery(id+"F0.wireOp",EDGE,"E576"),sQuery(id+"F0.wireOp",EDGE,"E577"),sQuery(id+"F0.wireOp",EDGE,"E578"),sQuery(id+"F0.wireOp",EDGE,"E579"),sQuery(id+"F0.wireOp",EDGE,"E580"),sQuery(id+"F0.wireOp",EDGE,"E581"),sQuery(id+"F0.wireOp",EDGE,"E582"),sQuery(id+"F0.wireOp",EDGE,"E583"),sQuery(id+"F0.wireOp",EDGE,"E584"),sQuery(id+"F0.wireOp",EDGE,"E585"),sQuery(id+"F0.wireOp",EDGE,"E586"),sQuery(id+"F0.wireOp",EDGE,"E587"),sQuery(id+"F0.wireOp",EDGE,"E588"),sQuery(id+"F0.wireOp",EDGE,"E589"),sQuery(id+"F0.wireOp",EDGE,"E590"),sQuery(id+"F0.wireOp",EDGE,"E591")])]});
            var Q1;
            Q1=sQuery(id+"F0.wireOp",VERTEX,"E296.end");
            transform(context, id + "F2", {"entities" : qUnion([Q0]), "transformType" : TransformType.SCALE_UNIFORMLY, "scale" : 0, "scalePoint" : qUnion([Q1]), "makeCopy" : false});
        }
        {
            var Q0;
            Q0=makeQuery(id+"F1.opExtrude","SWEPT_BODY",BODY,{"disambiguationData":[OSD([sQuery(id+"F0.wireOp",EDGE,"E0"),sQuery(id+"F0.wireOp",EDGE,"E1"),sQuery(id+"F0.wireOp",EDGE,"E2"),sQuery(id+"F0.wireOp",EDGE,"E3"),sQuery(id+"F0.wireOp",EDGE,"E4"),sQuery(id+"F0.wireOp",EDGE,"E5"),sQuery(id+"F0.wireOp",EDGE,"E6"),sQuery(id+"F0.wireOp",EDGE,"E7"),sQuery(id+"F0.wireOp",EDGE,"E8"),sQuery(id+"F0.wireOp",EDGE,"E9"),sQuery(id+"F0.wireOp",EDGE,"E10"),sQuery(id+"F0.wireOp",EDGE,"E11"),sQuery(id+"F0.wireOp",EDGE,"E12"),sQuery(id+"F0.wireOp",EDGE,"E13"),sQuery(id+"F0.wireOp",EDGE,"E14"),sQuery(id+"F0.wireOp",EDGE,"E15"),sQuery(id+"F0.wireOp",EDGE,"E16"),sQuery(id+"F0.wireOp",EDGE,"E17"),sQuery(id+"F0.wireOp",EDGE,"E18"),sQuery(id+"F0.wireOp",EDGE,"E19"),sQuery(id+"F0.wireOp",EDGE,"E20"),sQuery(id+"F0.wireOp",EDGE,"E21"),sQuery(id+"F0.wireOp",EDGE,"E22"),sQuery(id+"F0.wireOp",EDGE,"E23"),sQuery(id+"F0.wireOp",EDGE,"E24"),sQuery(id+"F0.wireOp",EDGE,"E25"),sQuery(id+"F0.wireOp",EDGE,"E26"),sQuery(id+"F0.wireOp",EDGE,"E27"),sQuery(id+"F0.wireOp",EDGE,"E28"),sQuery(id+"F0.wireOp",EDGE,"E29"),sQuery(id+"F0.wireOp",EDGE,"E30"),sQuery(id+"F0.wireOp",EDGE,"E31"),sQuery(id+"F0.wireOp",EDGE,"E32"),sQuery(id+"F0.wireOp",EDGE,"E33"),sQuery(id+"F0.wireOp",EDGE,"E34"),sQuery(id+"F0.wireOp",EDGE,"E35"),sQuery(id+"F0.wireOp",EDGE,"E36"),sQuery(id+"F0.wireOp",EDGE,"E37"),sQuery(id+"F0.wireOp",EDGE,"E38"),sQuery(id+"F0.wireOp",EDGE,"E39"),sQuery(id+"F0.wireOp",EDGE,"E40"),sQuery(id+"F0.wireOp",EDGE,"E41"),sQuery(id+"F0.wireOp",EDGE,"E42"),sQuery(id+"F0.wireOp",EDGE,"E43"),sQuery(id+"F0.wireOp",EDGE,"E44"),sQuery(id+"F0.wireOp",EDGE,"E45"),sQuery(id+"F0.wireOp",EDGE,"E46"),sQuery(id+"F0.wireOp",EDGE,"E47"),sQuery(id+"F0.wireOp",EDGE,"E48"),sQuery(id+"F0.wireOp",EDGE,"E49"),sQuery(id+"F0.wireOp",EDGE,"E50"),sQuery(id+"F0.wireOp",EDGE,"E51"),sQuery(id+"F0.wireOp",EDGE,"E52"),sQuery(id+"F0.wireOp",EDGE,"E53"),sQuery(id+"F0.wireOp",EDGE,"E54"),sQuery(id+"F0.wireOp",EDGE,"E55"),sQuery(id+"F0.wireOp",EDGE,"E56"),sQuery(id+"F0.wireOp",EDGE,"E57"),sQuery(id+"F0.wireOp",EDGE,"E58"),sQuery(id+"F0.wireOp",EDGE,"E59"),sQuery(id+"F0.wireOp",EDGE,"E60"),sQuery(id+"F0.wireOp",EDGE,"E61"),sQuery(id+"F0.wireOp",EDGE,"E62"),sQuery(id+"F0.wireOp",EDGE,"E63"),sQuery(id+"F0.wireOp",EDGE,"E64"),sQuery(id+"F0.wireOp",EDGE,"E65"),sQuery(id+"F0.wireOp",EDGE,"E66"),sQuery(id+"F0.wireOp",EDGE,"E67"),sQuery(id+"F0.wireOp",EDGE,"E68"),sQuery(id+"F0.wireOp",EDGE,"E69"),sQuery(id+"F0.wireOp",EDGE,"E70"),sQuery(id+"F0.wireOp",EDGE,"E71"),sQuery(id+"F0.wireOp",EDGE,"E72"),sQuery(id+"F0.wireOp",EDGE,"E73"),sQuery(id+"F0.wireOp",EDGE,"E74"),sQuery(id+"F0.wireOp",EDGE,"E75"),sQuery(id+"F0.wireOp",EDGE,"E76"),sQuery(id+"F0.wireOp",EDGE,"E77"),sQuery(id+"F0.wireOp",EDGE,"E78"),sQuery(id+"F0.wireOp",EDGE,"E79"),sQuery(id+"F0.wireOp",EDGE,"E80"),sQuery(id+"F0.wireOp",EDGE,"E81"),sQuery(id+"F0.wireOp",EDGE,"E82"),sQuery(id+"F0.wireOp",EDGE,"E83"),sQuery(id+"F0.wireOp",EDGE,"E84"),sQuery(id+"F0.wireOp",EDGE,"E85"),sQuery(id+"F0.wireOp",EDGE,"E86"),sQuery(id+"F0.wireOp",EDGE,"E87"),sQuery(id+"F0.wireOp",EDGE,"E88"),sQuery(id+"F0.wireOp",EDGE,"E89"),sQuery(id+"F0.wireOp",EDGE,"E90"),sQuery(id+"F0.wireOp",EDGE,"E91"),sQuery(id+"F0.wireOp",EDGE,"E92"),sQuery(id+"F0.wireOp",EDGE,"E93"),sQuery(id+"F0.wireOp",EDGE,"E94"),sQuery(id+"F0.wireOp",EDGE,"E95"),sQuery(id+"F0.wireOp",EDGE,"E96"),sQuery(id+"F0.wireOp",EDGE,"E97"),sQuery(id+"F0.wireOp",EDGE,"E98"),sQuery(id+"F0.wireOp",EDGE,"E99"),sQuery(id+"F0.wireOp",EDGE,"E100"),sQuery(id+"F0.wireOp",EDGE,"E101"),sQuery(id+"F0.wireOp",EDGE,"E102"),sQuery(id+"F0.wireOp",EDGE,"E103"),sQuery(id+"F0.wireOp",EDGE,"E104"),sQuery(id+"F0.wireOp",EDGE,"E105"),sQuery(id+"F0.wireOp",EDGE,"E106"),sQuery(id+"F0.wireOp",EDGE,"E107"),sQuery(id+"F0.wireOp",EDGE,"E108"),sQuery(id+"F0.wireOp",EDGE,"E109"),sQuery(id+"F0.wireOp",EDGE,"E110"),sQuery(id+"F0.wireOp",EDGE,"E111"),sQuery(id+"F0.wireOp",EDGE,"E112"),sQuery(id+"F0.wireOp",EDGE,"E113"),sQuery(id+"F0.wireOp",EDGE,"E114"),sQuery(id+"F0.wireOp",EDGE,"E115"),sQuery(id+"F0.wireOp",EDGE,"E116"),sQuery(id+"F0.wireOp",EDGE,"E117"),sQuery(id+"F0.wireOp",EDGE,"E118"),sQuery(id+"F0.wireOp",EDGE,"E119"),sQuery(id+"F0.wireOp",EDGE,"E120"),sQuery(id+"F0.wireOp",EDGE,"E121"),sQuery(id+"F0.wireOp",EDGE,"E122"),sQuery(id+"F0.wireOp",EDGE,"E123"),sQuery(id+"F0.wireOp",EDGE,"E124"),sQuery(id+"F0.wireOp",EDGE,"E125"),sQuery(id+"F0.wireOp",EDGE,"E126"),sQuery(id+"F0.wireOp",EDGE,"E127"),sQuery(id+"F0.wireOp",EDGE,"E128"),sQuery(id+"F0.wireOp",EDGE,"E129"),sQuery(id+"F0.wireOp",EDGE,"E130"),sQuery(id+"F0.wireOp",EDGE,"E131"),sQuery(id+"F0.wireOp",EDGE,"E132"),sQuery(id+"F0.wireOp",EDGE,"E133"),sQuery(id+"F0.wireOp",EDGE,"E134"),sQuery(id+"F0.wireOp",EDGE,"E135"),sQuery(id+"F0.wireOp",EDGE,"E136"),sQuery(id+"F0.wireOp",EDGE,"E137"),sQuery(id+"F0.wireOp",EDGE,"E138"),sQuery(id+"F0.wireOp",EDGE,"E139"),sQuery(id+"F0.wireOp",EDGE,"E140"),sQuery(id+"F0.wireOp",EDGE,"E141"),sQuery(id+"F0.wireOp",EDGE,"E142"),sQuery(id+"F0.wireOp",EDGE,"E143"),sQuery(id+"F0.wireOp",EDGE,"E144"),sQuery(id+"F0.wireOp",EDGE,"E145"),sQuery(id+"F0.wireOp",EDGE,"E146"),sQuery(id+"F0.wireOp",EDGE,"E147"),sQuery(id+"F0.wireOp",EDGE,"E148"),sQuery(id+"F0.wireOp",EDGE,"E149"),sQuery(id+"F0.wireOp",EDGE,"E150"),sQuery(id+"F0.wireOp",EDGE,"E151"),sQuery(id+"F0.wireOp",EDGE,"E152"),sQuery(id+"F0.wireOp",EDGE,"E153"),sQuery(id+"F0.wireOp",EDGE,"E154"),sQuery(id+"F0.wireOp",EDGE,"E155"),sQuery(id+"F0.wireOp",EDGE,"E156"),sQuery(id+"F0.wireOp",EDGE,"E157"),sQuery(id+"F0.wireOp",EDGE,"E158"),sQuery(id+"F0.wireOp",EDGE,"E159"),sQuery(id+"F0.wireOp",EDGE,"E160"),sQuery(id+"F0.wireOp",EDGE,"E161"),sQuery(id+"F0.wireOp",EDGE,"E162"),sQuery(id+"F0.wireOp",EDGE,"E163"),sQuery(id+"F0.wireOp",EDGE,"E164"),sQuery(id+"F0.wireOp",EDGE,"E165"),sQuery(id+"F0.wireOp",EDGE,"E166"),sQuery(id+"F0.wireOp",EDGE,"E167"),sQuery(id+"F0.wireOp",EDGE,"E168"),sQuery(id+"F0.wireOp",EDGE,"E169"),sQuery(id+"F0.wireOp",EDGE,"E170"),sQuery(id+"F0.wireOp",EDGE,"E171"),sQuery(id+"F0.wireOp",EDGE,"E172"),sQuery(id+"F0.wireOp",EDGE,"E173"),sQuery(id+"F0.wireOp",EDGE,"E174"),sQuery(id+"F0.wireOp",EDGE,"E175"),sQuery(id+"F0.wireOp",EDGE,"E176"),sQuery(id+"F0.wireOp",EDGE,"E177"),sQuery(id+"F0.wireOp",EDGE,"E178"),sQuery(id+"F0.wireOp",EDGE,"E179"),sQuery(id+"F0.wireOp",EDGE,"E180"),sQuery(id+"F0.wireOp",EDGE,"E181"),sQuery(id+"F0.wireOp",EDGE,"E182"),sQuery(id+"F0.wireOp",EDGE,"E183"),sQuery(id+"F0.wireOp",EDGE,"E184"),sQuery(id+"F0.wireOp",EDGE,"E185"),sQuery(id+"F0.wireOp",EDGE,"E186"),sQuery(id+"F0.wireOp",EDGE,"E187"),sQuery(id+"F0.wireOp",EDGE,"E188"),sQuery(id+"F0.wireOp",EDGE,"E189"),sQuery(id+"F0.wireOp",EDGE,"E190"),sQuery(id+"F0.wireOp",EDGE,"E191"),sQuery(id+"F0.wireOp",EDGE,"E192"),sQuery(id+"F0.wireOp",EDGE,"E193"),sQuery(id+"F0.wireOp",EDGE,"E194"),sQuery(id+"F0.wireOp",EDGE,"E195"),sQuery(id+"F0.wireOp",EDGE,"E196"),sQuery(id+"F0.wireOp",EDGE,"E197"),sQuery(id+"F0.wireOp",EDGE,"E198"),sQuery(id+"F0.wireOp",EDGE,"E199"),sQuery(id+"F0.wireOp",EDGE,"E200"),sQuery(id+"F0.wireOp",EDGE,"E201"),sQuery(id+"F0.wireOp",EDGE,"E202"),sQuery(id+"F0.wireOp",EDGE,"E203"),sQuery(id+"F0.wireOp",EDGE,"E204"),sQuery(id+"F0.wireOp",EDGE,"E205"),sQuery(id+"F0.wireOp",EDGE,"E206"),sQuery(id+"F0.wireOp",EDGE,"E207"),sQuery(id+"F0.wireOp",EDGE,"E208"),sQuery(id+"F0.wireOp",EDGE,"E209"),sQuery(id+"F0.wireOp",EDGE,"E210"),sQuery(id+"F0.wireOp",EDGE,"E211"),sQuery(id+"F0.wireOp",EDGE,"E212"),sQuery(id+"F0.wireOp",EDGE,"E213"),sQuery(id+"F0.wireOp",EDGE,"E214"),sQuery(id+"F0.wireOp",EDGE,"E215"),sQuery(id+"F0.wireOp",EDGE,"E216"),sQuery(id+"F0.wireOp",EDGE,"E217"),sQuery(id+"F0.wireOp",EDGE,"E218"),sQuery(id+"F0.wireOp",EDGE,"E219"),sQuery(id+"F0.wireOp",EDGE,"E220"),sQuery(id+"F0.wireOp",EDGE,"E221"),sQuery(id+"F0.wireOp",EDGE,"E222"),sQuery(id+"F0.wireOp",EDGE,"E223"),sQuery(id+"F0.wireOp",EDGE,"E224"),sQuery(id+"F0.wireOp",EDGE,"E225"),sQuery(id+"F0.wireOp",EDGE,"E226"),sQuery(id+"F0.wireOp",EDGE,"E227"),sQuery(id+"F0.wireOp",EDGE,"E228"),sQuery(id+"F0.wireOp",EDGE,"E229"),sQuery(id+"F0.wireOp",EDGE,"E230"),sQuery(id+"F0.wireOp",EDGE,"E231"),sQuery(id+"F0.wireOp",EDGE,"E232"),sQuery(id+"F0.wireOp",EDGE,"E233"),sQuery(id+"F0.wireOp",EDGE,"E234"),sQuery(id+"F0.wireOp",EDGE,"E235"),sQuery(id+"F0.wireOp",EDGE,"E236"),sQuery(id+"F0.wireOp",EDGE,"E237"),sQuery(id+"F0.wireOp",EDGE,"E238"),sQuery(id+"F0.wireOp",EDGE,"E239"),sQuery(id+"F0.wireOp",EDGE,"E240"),sQuery(id+"F0.wireOp",EDGE,"E241"),sQuery(id+"F0.wireOp",EDGE,"E242"),sQuery(id+"F0.wireOp",EDGE,"E243"),sQuery(id+"F0.wireOp",EDGE,"E244"),sQuery(id+"F0.wireOp",EDGE,"E245"),sQuery(id+"F0.wireOp",EDGE,"E246"),sQuery(id+"F0.wireOp",EDGE,"E247"),sQuery(id+"F0.wireOp",EDGE,"E248"),sQuery(id+"F0.wireOp",EDGE,"E249"),sQuery(id+"F0.wireOp",EDGE,"E250"),sQuery(id+"F0.wireOp",EDGE,"E251"),sQuery(id+"F0.wireOp",EDGE,"E252"),sQuery(id+"F0.wireOp",EDGE,"E253"),sQuery(id+"F0.wireOp",EDGE,"E254"),sQuery(id+"F0.wireOp",EDGE,"E255"),sQuery(id+"F0.wireOp",EDGE,"E256"),sQuery(id+"F0.wireOp",EDGE,"E257"),sQuery(id+"F0.wireOp",EDGE,"E258"),sQuery(id+"F0.wireOp",EDGE,"E259"),sQuery(id+"F0.wireOp",EDGE,"E260"),sQuery(id+"F0.wireOp",EDGE,"E261"),sQuery(id+"F0.wireOp",EDGE,"E262"),sQuery(id+"F0.wireOp",EDGE,"E263"),sQuery(id+"F0.wireOp",EDGE,"E264"),sQuery(id+"F0.wireOp",EDGE,"E265"),sQuery(id+"F0.wireOp",EDGE,"E266"),sQuery(id+"F0.wireOp",EDGE,"E267"),sQuery(id+"F0.wireOp",EDGE,"E268"),sQuery(id+"F0.wireOp",EDGE,"E269"),sQuery(id+"F0.wireOp",EDGE,"E270"),sQuery(id+"F0.wireOp",EDGE,"E271"),sQuery(id+"F0.wireOp",EDGE,"E272"),sQuery(id+"F0.wireOp",EDGE,"E273"),sQuery(id+"F0.wireOp",EDGE,"E274"),sQuery(id+"F0.wireOp",EDGE,"E275"),sQuery(id+"F0.wireOp",EDGE,"E276"),sQuery(id+"F0.wireOp",EDGE,"E277"),sQuery(id+"F0.wireOp",EDGE,"E278"),sQuery(id+"F0.wireOp",EDGE,"E279"),sQuery(id+"F0.wireOp",EDGE,"E280"),sQuery(id+"F0.wireOp",EDGE,"E281"),sQuery(id+"F0.wireOp",EDGE,"E282"),sQuery(id+"F0.wireOp",EDGE,"E283"),sQuery(id+"F0.wireOp",EDGE,"E284"),sQuery(id+"F0.wireOp",EDGE,"E285"),sQuery(id+"F0.wireOp",EDGE,"E286"),sQuery(id+"F0.wireOp",EDGE,"E287"),sQuery(id+"F0.wireOp",EDGE,"E288"),sQuery(id+"F0.wireOp",EDGE,"E289"),sQuery(id+"F0.wireOp",EDGE,"E290"),sQuery(id+"F0.wireOp",EDGE,"E291"),sQuery(id+"F0.wireOp",EDGE,"E292"),sQuery(id+"F0.wireOp",EDGE,"E293"),sQuery(id+"F0.wireOp",EDGE,"E294"),sQuery(id+"F0.wireOp",EDGE,"E295"),sQuery(id+"F0.wireOp",EDGE,"E296"),sQuery(id+"F0.wireOp",EDGE,"E297"),sQuery(id+"F0.wireOp",EDGE,"E298"),sQuery(id+"F0.wireOp",EDGE,"E299"),sQuery(id+"F0.wireOp",EDGE,"E300"),sQuery(id+"F0.wireOp",EDGE,"E301"),sQuery(id+"F0.wireOp",EDGE,"E302"),sQuery(id+"F0.wireOp",EDGE,"E303"),sQuery(id+"F0.wireOp",EDGE,"E304"),sQuery(id+"F0.wireOp",EDGE,"E305"),sQuery(id+"F0.wireOp",EDGE,"E306"),sQuery(id+"F0.wireOp",EDGE,"E307"),sQuery(id+"F0.wireOp",EDGE,"E308"),sQuery(id+"F0.wireOp",EDGE,"E309"),sQuery(id+"F0.wireOp",EDGE,"E310"),sQuery(id+"F0.wireOp",EDGE,"E311"),sQuery(id+"F0.wireOp",EDGE,"E312"),sQuery(id+"F0.wireOp",EDGE,"E313"),sQuery(id+"F0.wireOp",EDGE,"E314"),sQuery(id+"F0.wireOp",EDGE,"E315"),sQuery(id+"F0.wireOp",EDGE,"E316"),sQuery(id+"F0.wireOp",EDGE,"E317"),sQuery(id+"F0.wireOp",EDGE,"E318"),sQuery(id+"F0.wireOp",EDGE,"E319"),sQuery(id+"F0.wireOp",EDGE,"E320"),sQuery(id+"F0.wireOp",EDGE,"E321"),sQuery(id+"F0.wireOp",EDGE,"E322"),sQuery(id+"F0.wireOp",EDGE,"E323"),sQuery(id+"F0.wireOp",EDGE,"E324"),sQuery(id+"F0.wireOp",EDGE,"E325"),sQuery(id+"F0.wireOp",EDGE,"E326"),sQuery(id+"F0.wireOp",EDGE,"E327"),sQuery(id+"F0.wireOp",EDGE,"E328"),sQuery(id+"F0.wireOp",EDGE,"E329"),sQuery(id+"F0.wireOp",EDGE,"E330"),sQuery(id+"F0.wireOp",EDGE,"E331"),sQuery(id+"F0.wireOp",EDGE,"E332"),sQuery(id+"F0.wireOp",EDGE,"E333"),sQuery(id+"F0.wireOp",EDGE,"E334"),sQuery(id+"F0.wireOp",EDGE,"E335"),sQuery(id+"F0.wireOp",EDGE,"E336"),sQuery(id+"F0.wireOp",EDGE,"E337"),sQuery(id+"F0.wireOp",EDGE,"E338"),sQuery(id+"F0.wireOp",EDGE,"E339"),sQuery(id+"F0.wireOp",EDGE,"E340"),sQuery(id+"F0.wireOp",EDGE,"E341"),sQuery(id+"F0.wireOp",EDGE,"E342"),sQuery(id+"F0.wireOp",EDGE,"E343"),sQuery(id+"F0.wireOp",EDGE,"E344"),sQuery(id+"F0.wireOp",EDGE,"E345"),sQuery(id+"F0.wireOp",EDGE,"E346"),sQuery(id+"F0.wireOp",EDGE,"E347"),sQuery(id+"F0.wireOp",EDGE,"E348"),sQuery(id+"F0.wireOp",EDGE,"E349"),sQuery(id+"F0.wireOp",EDGE,"E350"),sQuery(id+"F0.wireOp",EDGE,"E351"),sQuery(id+"F0.wireOp",EDGE,"E352"),sQuery(id+"F0.wireOp",EDGE,"E353"),sQuery(id+"F0.wireOp",EDGE,"E354"),sQuery(id+"F0.wireOp",EDGE,"E355"),sQuery(id+"F0.wireOp",EDGE,"E356"),sQuery(id+"F0.wireOp",EDGE,"E357"),sQuery(id+"F0.wireOp",EDGE,"E358"),sQuery(id+"F0.wireOp",EDGE,"E359"),sQuery(id+"F0.wireOp",EDGE,"E360"),sQuery(id+"F0.wireOp",EDGE,"E361"),sQuery(id+"F0.wireOp",EDGE,"E362"),sQuery(id+"F0.wireOp",EDGE,"E363"),sQuery(id+"F0.wireOp",EDGE,"E364"),sQuery(id+"F0.wireOp",EDGE,"E365"),sQuery(id+"F0.wireOp",EDGE,"E366"),sQuery(id+"F0.wireOp",EDGE,"E367"),sQuery(id+"F0.wireOp",EDGE,"E368"),sQuery(id+"F0.wireOp",EDGE,"E369"),sQuery(id+"F0.wireOp",EDGE,"E370"),sQuery(id+"F0.wireOp",EDGE,"E371"),sQuery(id+"F0.wireOp",EDGE,"E372"),sQuery(id+"F0.wireOp",EDGE,"E373"),sQuery(id+"F0.wireOp",EDGE,"E374"),sQuery(id+"F0.wireOp",EDGE,"E375"),sQuery(id+"F0.wireOp",EDGE,"E376"),sQuery(id+"F0.wireOp",EDGE,"E377"),sQuery(id+"F0.wireOp",EDGE,"E378"),sQuery(id+"F0.wireOp",EDGE,"E379"),sQuery(id+"F0.wireOp",EDGE,"E380"),sQuery(id+"F0.wireOp",EDGE,"E381"),sQuery(id+"F0.wireOp",EDGE,"E382"),sQuery(id+"F0.wireOp",EDGE,"E383"),sQuery(id+"F0.wireOp",EDGE,"E384"),sQuery(id+"F0.wireOp",EDGE,"E385"),sQuery(id+"F0.wireOp",EDGE,"E386"),sQuery(id+"F0.wireOp",EDGE,"E387"),sQuery(id+"F0.wireOp",EDGE,"E388"),sQuery(id+"F0.wireOp",EDGE,"E389"),sQuery(id+"F0.wireOp",EDGE,"E390"),sQuery(id+"F0.wireOp",EDGE,"E391"),sQuery(id+"F0.wireOp",EDGE,"E392"),sQuery(id+"F0.wireOp",EDGE,"E393"),sQuery(id+"F0.wireOp",EDGE,"E394"),sQuery(id+"F0.wireOp",EDGE,"E395"),sQuery(id+"F0.wireOp",EDGE,"E396"),sQuery(id+"F0.wireOp",EDGE,"E397"),sQuery(id+"F0.wireOp",EDGE,"E398"),sQuery(id+"F0.wireOp",EDGE,"E399"),sQuery(id+"F0.wireOp",EDGE,"E400"),sQuery(id+"F0.wireOp",EDGE,"E401"),sQuery(id+"F0.wireOp",EDGE,"E402"),sQuery(id+"F0.wireOp",EDGE,"E403"),sQuery(id+"F0.wireOp",EDGE,"E404"),sQuery(id+"F0.wireOp",EDGE,"E405"),sQuery(id+"F0.wireOp",EDGE,"E406"),sQuery(id+"F0.wireOp",EDGE,"E407"),sQuery(id+"F0.wireOp",EDGE,"E408"),sQuery(id+"F0.wireOp",EDGE,"E409"),sQuery(id+"F0.wireOp",EDGE,"E410"),sQuery(id+"F0.wireOp",EDGE,"E411"),sQuery(id+"F0.wireOp",EDGE,"E412"),sQuery(id+"F0.wireOp",EDGE,"E413"),sQuery(id+"F0.wireOp",EDGE,"E414"),sQuery(id+"F0.wireOp",EDGE,"E415"),sQuery(id+"F0.wireOp",EDGE,"E416"),sQuery(id+"F0.wireOp",EDGE,"E417"),sQuery(id+"F0.wireOp",EDGE,"E418"),sQuery(id+"F0.wireOp",EDGE,"E419"),sQuery(id+"F0.wireOp",EDGE,"E420"),sQuery(id+"F0.wireOp",EDGE,"E421"),sQuery(id+"F0.wireOp",EDGE,"E422"),sQuery(id+"F0.wireOp",EDGE,"E423"),sQuery(id+"F0.wireOp",EDGE,"E424"),sQuery(id+"F0.wireOp",EDGE,"E425"),sQuery(id+"F0.wireOp",EDGE,"E426"),sQuery(id+"F0.wireOp",EDGE,"E427"),sQuery(id+"F0.wireOp",EDGE,"E428"),sQuery(id+"F0.wireOp",EDGE,"E429"),sQuery(id+"F0.wireOp",EDGE,"E430"),sQuery(id+"F0.wireOp",EDGE,"E431"),sQuery(id+"F0.wireOp",EDGE,"E432"),sQuery(id+"F0.wireOp",EDGE,"E433"),sQuery(id+"F0.wireOp",EDGE,"E434"),sQuery(id+"F0.wireOp",EDGE,"E435"),sQuery(id+"F0.wireOp",EDGE,"E436"),sQuery(id+"F0.wireOp",EDGE,"E437"),sQuery(id+"F0.wireOp",EDGE,"E438"),sQuery(id+"F0.wireOp",EDGE,"E439"),sQuery(id+"F0.wireOp",EDGE,"E440"),sQuery(id+"F0.wireOp",EDGE,"E441"),sQuery(id+"F0.wireOp",EDGE,"E442"),sQuery(id+"F0.wireOp",EDGE,"E443"),sQuery(id+"F0.wireOp",EDGE,"E444"),sQuery(id+"F0.wireOp",EDGE,"E445"),sQuery(id+"F0.wireOp",EDGE,"E446"),sQuery(id+"F0.wireOp",EDGE,"E447"),sQuery(id+"F0.wireOp",EDGE,"E448"),sQuery(id+"F0.wireOp",EDGE,"E449"),sQuery(id+"F0.wireOp",EDGE,"E450"),sQuery(id+"F0.wireOp",EDGE,"E451"),sQuery(id+"F0.wireOp",EDGE,"E452"),sQuery(id+"F0.wireOp",EDGE,"E453"),sQuery(id+"F0.wireOp",EDGE,"E454"),sQuery(id+"F0.wireOp",EDGE,"E455"),sQuery(id+"F0.wireOp",EDGE,"E456"),sQuery(id+"F0.wireOp",EDGE,"E457"),sQuery(id+"F0.wireOp",EDGE,"E458"),sQuery(id+"F0.wireOp",EDGE,"E459"),sQuery(id+"F0.wireOp",EDGE,"E460"),sQuery(id+"F0.wireOp",EDGE,"E461"),sQuery(id+"F0.wireOp",EDGE,"E462"),sQuery(id+"F0.wireOp",EDGE,"E463"),sQuery(id+"F0.wireOp",EDGE,"E464"),sQuery(id+"F0.wireOp",EDGE,"E465"),sQuery(id+"F0.wireOp",EDGE,"E466"),sQuery(id+"F0.wireOp",EDGE,"E467"),sQuery(id+"F0.wireOp",EDGE,"E468"),sQuery(id+"F0.wireOp",EDGE,"E469"),sQuery(id+"F0.wireOp",EDGE,"E470"),sQuery(id+"F0.wireOp",EDGE,"E471"),sQuery(id+"F0.wireOp",EDGE,"E472"),sQuery(id+"F0.wireOp",EDGE,"E473"),sQuery(id+"F0.wireOp",EDGE,"E474"),sQuery(id+"F0.wireOp",EDGE,"E475"),sQuery(id+"F0.wireOp",EDGE,"E476"),sQuery(id+"F0.wireOp",EDGE,"E477"),sQuery(id+"F0.wireOp",EDGE,"E478"),sQuery(id+"F0.wireOp",EDGE,"E479"),sQuery(id+"F0.wireOp",EDGE,"E480"),sQuery(id+"F0.wireOp",EDGE,"E481"),sQuery(id+"F0.wireOp",EDGE,"E482"),sQuery(id+"F0.wireOp",EDGE,"E483"),sQuery(id+"F0.wireOp",EDGE,"E484"),sQuery(id+"F0.wireOp",EDGE,"E485"),sQuery(id+"F0.wireOp",EDGE,"E486"),sQuery(id+"F0.wireOp",EDGE,"E487"),sQuery(id+"F0.wireOp",EDGE,"E488"),sQuery(id+"F0.wireOp",EDGE,"E489"),sQuery(id+"F0.wireOp",EDGE,"E490"),sQuery(id+"F0.wireOp",EDGE,"E491"),sQuery(id+"F0.wireOp",EDGE,"E492"),sQuery(id+"F0.wireOp",EDGE,"E493"),sQuery(id+"F0.wireOp",EDGE,"E494"),sQuery(id+"F0.wireOp",EDGE,"E495"),sQuery(id+"F0.wireOp",EDGE,"E496"),sQuery(id+"F0.wireOp",EDGE,"E497"),sQuery(id+"F0.wireOp",EDGE,"E498"),sQuery(id+"F0.wireOp",EDGE,"E499"),sQuery(id+"F0.wireOp",EDGE,"E500"),sQuery(id+"F0.wireOp",EDGE,"E501"),sQuery(id+"F0.wireOp",EDGE,"E502"),sQuery(id+"F0.wireOp",EDGE,"E503"),sQuery(id+"F0.wireOp",EDGE,"E504"),sQuery(id+"F0.wireOp",EDGE,"E505"),sQuery(id+"F0.wireOp",EDGE,"E506"),sQuery(id+"F0.wireOp",EDGE,"E507"),sQuery(id+"F0.wireOp",EDGE,"E508"),sQuery(id+"F0.wireOp",EDGE,"E509"),sQuery(id+"F0.wireOp",EDGE,"E510"),sQuery(id+"F0.wireOp",EDGE,"E511"),sQuery(id+"F0.wireOp",EDGE,"E512"),sQuery(id+"F0.wireOp",EDGE,"E513"),sQuery(id+"F0.wireOp",EDGE,"E514"),sQuery(id+"F0.wireOp",EDGE,"E515"),sQuery(id+"F0.wireOp",EDGE,"E516"),sQuery(id+"F0.wireOp",EDGE,"E517"),sQuery(id+"F0.wireOp",EDGE,"E518"),sQuery(id+"F0.wireOp",EDGE,"E519"),sQuery(id+"F0.wireOp",EDGE,"E520"),sQuery(id+"F0.wireOp",EDGE,"E521"),sQuery(id+"F0.wireOp",EDGE,"E522"),sQuery(id+"F0.wireOp",EDGE,"E523"),sQuery(id+"F0.wireOp",EDGE,"E524"),sQuery(id+"F0.wireOp",EDGE,"E525"),sQuery(id+"F0.wireOp",EDGE,"E526"),sQuery(id+"F0.wireOp",EDGE,"E527"),sQuery(id+"F0.wireOp",EDGE,"E528"),sQuery(id+"F0.wireOp",EDGE,"E529"),sQuery(id+"F0.wireOp",EDGE,"E530"),sQuery(id+"F0.wireOp",EDGE,"E531"),sQuery(id+"F0.wireOp",EDGE,"E532"),sQuery(id+"F0.wireOp",EDGE,"E533"),sQuery(id+"F0.wireOp",EDGE,"E534"),sQuery(id+"F0.wireOp",EDGE,"E535"),sQuery(id+"F0.wireOp",EDGE,"E536"),sQuery(id+"F0.wireOp",EDGE,"E537"),sQuery(id+"F0.wireOp",EDGE,"E538"),sQuery(id+"F0.wireOp",EDGE,"E539"),sQuery(id+"F0.wireOp",EDGE,"E540"),sQuery(id+"F0.wireOp",EDGE,"E541"),sQuery(id+"F0.wireOp",EDGE,"E542"),sQuery(id+"F0.wireOp",EDGE,"E543"),sQuery(id+"F0.wireOp",EDGE,"E544"),sQuery(id+"F0.wireOp",EDGE,"E545"),sQuery(id+"F0.wireOp",EDGE,"E546"),sQuery(id+"F0.wireOp",EDGE,"E547"),sQuery(id+"F0.wireOp",EDGE,"E548"),sQuery(id+"F0.wireOp",EDGE,"E549"),sQuery(id+"F0.wireOp",EDGE,"E550"),sQuery(id+"F0.wireOp",EDGE,"E551"),sQuery(id+"F0.wireOp",EDGE,"E552"),sQuery(id+"F0.wireOp",EDGE,"E553"),sQuery(id+"F0.wireOp",EDGE,"E554"),sQuery(id+"F0.wireOp",EDGE,"E555"),sQuery(id+"F0.wireOp",EDGE,"E556"),sQuery(id+"F0.wireOp",EDGE,"E557"),sQuery(id+"F0.wireOp",EDGE,"E558"),sQuery(id+"F0.wireOp",EDGE,"E559"),sQuery(id+"F0.wireOp",EDGE,"E560"),sQuery(id+"F0.wireOp",EDGE,"E561"),sQuery(id+"F0.wireOp",EDGE,"E562"),sQuery(id+"F0.wireOp",EDGE,"E563"),sQuery(id+"F0.wireOp",EDGE,"E564"),sQuery(id+"F0.wireOp",EDGE,"E565"),sQuery(id+"F0.wireOp",EDGE,"E566"),sQuery(id+"F0.wireOp",EDGE,"E567"),sQuery(id+"F0.wireOp",EDGE,"E568"),sQuery(id+"F0.wireOp",EDGE,"E569"),sQuery(id+"F0.wireOp",EDGE,"E570"),sQuery(id+"F0.wireOp",EDGE,"E571"),sQuery(id+"F0.wireOp",EDGE,"E572"),sQuery(id+"F0.wireOp",EDGE,"E573"),sQuery(id+"F0.wireOp",EDGE,"E574"),sQuery(id+"F0.wireOp",EDGE,"E575"),sQuery(id+"F0.wireOp",EDGE,"E576"),sQuery(id+"F0.wireOp",EDGE,"E577"),sQuery(id+"F0.wireOp",EDGE,"E578"),sQuery(id+"F0.wireOp",EDGE,"E579"),sQuery(id+"F0.wireOp",EDGE,"E580"),sQuery(id+"F0.wireOp",EDGE,"E581"),sQuery(id+"F0.wireOp",EDGE,"E582"),sQuery(id+"F0.wireOp",EDGE,"E583"),sQuery(id+"F0.wireOp",EDGE,"E584"),sQuery(id+"F0.wireOp",EDGE,"E585"),sQuery(id+"F0.wireOp",EDGE,"E586"),sQuery(id+"F0.wireOp",EDGE,"E587"),sQuery(id+"F0.wireOp",EDGE,"E588"),sQuery(id+"F0.wireOp",EDGE,"E589"),sQuery(id+"F0.wireOp",EDGE,"E590"),sQuery(id+"F0.wireOp",EDGE,"E591")])]});
            var Q1;
            Q1=makeQuery(id+"F1.opExtrude","SWEPT_BODY",BODY,{"disambiguationData":[OSD([sQuery(id+"F0.wireOp",EDGE,"E0"),sQuery(id+"F0.wireOp",EDGE,"E1"),sQuery(id+"F0.wireOp",EDGE,"E2"),sQuery(id+"F0.wireOp",EDGE,"E3"),sQuery(id+"F0.wireOp",EDGE,"E4"),sQuery(id+"F0.wireOp",EDGE,"E5"),sQuery(id+"F0.wireOp",EDGE,"E6"),sQuery(id+"F0.wireOp",EDGE,"E7"),sQuery(id+"F0.wireOp",EDGE,"E8"),sQuery(id+"F0.wireOp",EDGE,"E9"),sQuery(id+"F0.wireOp",EDGE,"E10"),sQuery(id+"F0.wireOp",EDGE,"E11"),sQuery(id+"F0.wireOp",EDGE,"E12"),sQuery(id+"F0.wireOp",EDGE,"E13"),sQuery(id+"F0.wireOp",EDGE,"E14"),sQuery(id+"F0.wireOp",EDGE,"E15"),sQuery(id+"F0.wireOp",EDGE,"E16"),sQuery(id+"F0.wireOp",EDGE,"E17"),sQuery(id+"F0.wireOp",EDGE,"E18"),sQuery(id+"F0.wireOp",EDGE,"E19"),sQuery(id+"F0.wireOp",EDGE,"E20"),sQuery(id+"F0.wireOp",EDGE,"E21"),sQuery(id+"F0.wireOp",EDGE,"E22"),sQuery(id+"F0.wireOp",EDGE,"E23"),sQuery(id+"F0.wireOp",EDGE,"E24"),sQuery(id+"F0.wireOp",EDGE,"E25"),sQuery(id+"F0.wireOp",EDGE,"E26"),sQuery(id+"F0.wireOp",EDGE,"E27"),sQuery(id+"F0.wireOp",EDGE,"E28"),sQuery(id+"F0.wireOp",EDGE,"E29"),sQuery(id+"F0.wireOp",EDGE,"E30"),sQuery(id+"F0.wireOp",EDGE,"E31"),sQuery(id+"F0.wireOp",EDGE,"E32"),sQuery(id+"F0.wireOp",EDGE,"E33"),sQuery(id+"F0.wireOp",EDGE,"E34"),sQuery(id+"F0.wireOp",EDGE,"E35"),sQuery(id+"F0.wireOp",EDGE,"E36"),sQuery(id+"F0.wireOp",EDGE,"E37"),sQuery(id+"F0.wireOp",EDGE,"E38"),sQuery(id+"F0.wireOp",EDGE,"E39"),sQuery(id+"F0.wireOp",EDGE,"E40"),sQuery(id+"F0.wireOp",EDGE,"E41"),sQuery(id+"F0.wireOp",EDGE,"E42"),sQuery(id+"F0.wireOp",EDGE,"E43"),sQuery(id+"F0.wireOp",EDGE,"E44"),sQuery(id+"F0.wireOp",EDGE,"E45"),sQuery(id+"F0.wireOp",EDGE,"E46"),sQuery(id+"F0.wireOp",EDGE,"E47"),sQuery(id+"F0.wireOp",EDGE,"E48"),sQuery(id+"F0.wireOp",EDGE,"E49"),sQuery(id+"F0.wireOp",EDGE,"E50"),sQuery(id+"F0.wireOp",EDGE,"E51"),sQuery(id+"F0.wireOp",EDGE,"E52"),sQuery(id+"F0.wireOp",EDGE,"E53"),sQuery(id+"F0.wireOp",EDGE,"E54"),sQuery(id+"F0.wireOp",EDGE,"E55"),sQuery(id+"F0.wireOp",EDGE,"E56"),sQuery(id+"F0.wireOp",EDGE,"E57"),sQuery(id+"F0.wireOp",EDGE,"E58"),sQuery(id+"F0.wireOp",EDGE,"E59"),sQuery(id+"F0.wireOp",EDGE,"E60"),sQuery(id+"F0.wireOp",EDGE,"E61"),sQuery(id+"F0.wireOp",EDGE,"E62"),sQuery(id+"F0.wireOp",EDGE,"E63"),sQuery(id+"F0.wireOp",EDGE,"E64"),sQuery(id+"F0.wireOp",EDGE,"E65"),sQuery(id+"F0.wireOp",EDGE,"E66"),sQuery(id+"F0.wireOp",EDGE,"E67"),sQuery(id+"F0.wireOp",EDGE,"E68"),sQuery(id+"F0.wireOp",EDGE,"E69"),sQuery(id+"F0.wireOp",EDGE,"E70"),sQuery(id+"F0.wireOp",EDGE,"E71"),sQuery(id+"F0.wireOp",EDGE,"E72"),sQuery(id+"F0.wireOp",EDGE,"E73"),sQuery(id+"F0.wireOp",EDGE,"E74"),sQuery(id+"F0.wireOp",EDGE,"E75"),sQuery(id+"F0.wireOp",EDGE,"E76"),sQuery(id+"F0.wireOp",EDGE,"E77"),sQuery(id+"F0.wireOp",EDGE,"E78"),sQuery(id+"F0.wireOp",EDGE,"E79"),sQuery(id+"F0.wireOp",EDGE,"E80"),sQuery(id+"F0.wireOp",EDGE,"E81"),sQuery(id+"F0.wireOp",EDGE,"E82"),sQuery(id+"F0.wireOp",EDGE,"E83"),sQuery(id+"F0.wireOp",EDGE,"E84"),sQuery(id+"F0.wireOp",EDGE,"E85"),sQuery(id+"F0.wireOp",EDGE,"E86"),sQuery(id+"F0.wireOp",EDGE,"E87"),sQuery(id+"F0.wireOp",EDGE,"E88"),sQuery(id+"F0.wireOp",EDGE,"E89"),sQuery(id+"F0.wireOp",EDGE,"E90"),sQuery(id+"F0.wireOp",EDGE,"E91"),sQuery(id+"F0.wireOp",EDGE,"E92"),sQuery(id+"F0.wireOp",EDGE,"E93"),sQuery(id+"F0.wireOp",EDGE,"E94"),sQuery(id+"F0.wireOp",EDGE,"E95"),sQuery(id+"F0.wireOp",EDGE,"E96"),sQuery(id+"F0.wireOp",EDGE,"E97"),sQuery(id+"F0.wireOp",EDGE,"E98"),sQuery(id+"F0.wireOp",EDGE,"E99"),sQuery(id+"F0.wireOp",EDGE,"E100"),sQuery(id+"F0.wireOp",EDGE,"E101"),sQuery(id+"F0.wireOp",EDGE,"E102"),sQuery(id+"F0.wireOp",EDGE,"E103"),sQuery(id+"F0.wireOp",EDGE,"E104"),sQuery(id+"F0.wireOp",EDGE,"E105"),sQuery(id+"F0.wireOp",EDGE,"E106"),sQuery(id+"F0.wireOp",EDGE,"E107"),sQuery(id+"F0.wireOp",EDGE,"E108"),sQuery(id+"F0.wireOp",EDGE,"E109"),sQuery(id+"F0.wireOp",EDGE,"E110"),sQuery(id+"F0.wireOp",EDGE,"E111"),sQuery(id+"F0.wireOp",EDGE,"E112"),sQuery(id+"F0.wireOp",EDGE,"E113"),sQuery(id+"F0.wireOp",EDGE,"E114"),sQuery(id+"F0.wireOp",EDGE,"E115"),sQuery(id+"F0.wireOp",EDGE,"E116"),sQuery(id+"F0.wireOp",EDGE,"E117"),sQuery(id+"F0.wireOp",EDGE,"E118"),sQuery(id+"F0.wireOp",EDGE,"E119"),sQuery(id+"F0.wireOp",EDGE,"E120"),sQuery(id+"F0.wireOp",EDGE,"E121"),sQuery(id+"F0.wireOp",EDGE,"E122"),sQuery(id+"F0.wireOp",EDGE,"E123"),sQuery(id+"F0.wireOp",EDGE,"E124"),sQuery(id+"F0.wireOp",EDGE,"E125"),sQuery(id+"F0.wireOp",EDGE,"E126"),sQuery(id+"F0.wireOp",EDGE,"E127"),sQuery(id+"F0.wireOp",EDGE,"E128"),sQuery(id+"F0.wireOp",EDGE,"E129"),sQuery(id+"F0.wireOp",EDGE,"E130"),sQuery(id+"F0.wireOp",EDGE,"E131"),sQuery(id+"F0.wireOp",EDGE,"E132"),sQuery(id+"F0.wireOp",EDGE,"E133"),sQuery(id+"F0.wireOp",EDGE,"E134"),sQuery(id+"F0.wireOp",EDGE,"E135"),sQuery(id+"F0.wireOp",EDGE,"E136"),sQuery(id+"F0.wireOp",EDGE,"E137"),sQuery(id+"F0.wireOp",EDGE,"E138"),sQuery(id+"F0.wireOp",EDGE,"E139"),sQuery(id+"F0.wireOp",EDGE,"E140"),sQuery(id+"F0.wireOp",EDGE,"E141"),sQuery(id+"F0.wireOp",EDGE,"E142"),sQuery(id+"F0.wireOp",EDGE,"E143"),sQuery(id+"F0.wireOp",EDGE,"E144"),sQuery(id+"F0.wireOp",EDGE,"E145"),sQuery(id+"F0.wireOp",EDGE,"E146"),sQuery(id+"F0.wireOp",EDGE,"E147"),sQuery(id+"F0.wireOp",EDGE,"E148"),sQuery(id+"F0.wireOp",EDGE,"E149"),sQuery(id+"F0.wireOp",EDGE,"E150"),sQuery(id+"F0.wireOp",EDGE,"E151"),sQuery(id+"F0.wireOp",EDGE,"E152"),sQuery(id+"F0.wireOp",EDGE,"E153"),sQuery(id+"F0.wireOp",EDGE,"E154"),sQuery(id+"F0.wireOp",EDGE,"E155"),sQuery(id+"F0.wireOp",EDGE,"E156"),sQuery(id+"F0.wireOp",EDGE,"E157"),sQuery(id+"F0.wireOp",EDGE,"E158"),sQuery(id+"F0.wireOp",EDGE,"E159"),sQuery(id+"F0.wireOp",EDGE,"E160"),sQuery(id+"F0.wireOp",EDGE,"E161"),sQuery(id+"F0.wireOp",EDGE,"E162"),sQuery(id+"F0.wireOp",EDGE,"E163"),sQuery(id+"F0.wireOp",EDGE,"E164"),sQuery(id+"F0.wireOp",EDGE,"E165"),sQuery(id+"F0.wireOp",EDGE,"E166"),sQuery(id+"F0.wireOp",EDGE,"E167"),sQuery(id+"F0.wireOp",EDGE,"E168"),sQuery(id+"F0.wireOp",EDGE,"E169"),sQuery(id+"F0.wireOp",EDGE,"E170"),sQuery(id+"F0.wireOp",EDGE,"E171"),sQuery(id+"F0.wireOp",EDGE,"E172"),sQuery(id+"F0.wireOp",EDGE,"E173"),sQuery(id+"F0.wireOp",EDGE,"E174"),sQuery(id+"F0.wireOp",EDGE,"E175"),sQuery(id+"F0.wireOp",EDGE,"E176"),sQuery(id+"F0.wireOp",EDGE,"E177"),sQuery(id+"F0.wireOp",EDGE,"E178"),sQuery(id+"F0.wireOp",EDGE,"E179"),sQuery(id+"F0.wireOp",EDGE,"E180"),sQuery(id+"F0.wireOp",EDGE,"E181"),sQuery(id+"F0.wireOp",EDGE,"E182"),sQuery(id+"F0.wireOp",EDGE,"E183"),sQuery(id+"F0.wireOp",EDGE,"E184"),sQuery(id+"F0.wireOp",EDGE,"E185"),sQuery(id+"F0.wireOp",EDGE,"E186"),sQuery(id+"F0.wireOp",EDGE,"E187"),sQuery(id+"F0.wireOp",EDGE,"E188"),sQuery(id+"F0.wireOp",EDGE,"E189"),sQuery(id+"F0.wireOp",EDGE,"E190"),sQuery(id+"F0.wireOp",EDGE,"E191"),sQuery(id+"F0.wireOp",EDGE,"E192"),sQuery(id+"F0.wireOp",EDGE,"E193"),sQuery(id+"F0.wireOp",EDGE,"E194"),sQuery(id+"F0.wireOp",EDGE,"E195"),sQuery(id+"F0.wireOp",EDGE,"E196"),sQuery(id+"F0.wireOp",EDGE,"E197"),sQuery(id+"F0.wireOp",EDGE,"E198"),sQuery(id+"F0.wireOp",EDGE,"E199"),sQuery(id+"F0.wireOp",EDGE,"E200"),sQuery(id+"F0.wireOp",EDGE,"E201"),sQuery(id+"F0.wireOp",EDGE,"E202"),sQuery(id+"F0.wireOp",EDGE,"E203"),sQuery(id+"F0.wireOp",EDGE,"E204"),sQuery(id+"F0.wireOp",EDGE,"E205"),sQuery(id+"F0.wireOp",EDGE,"E206"),sQuery(id+"F0.wireOp",EDGE,"E207"),sQuery(id+"F0.wireOp",EDGE,"E208"),sQuery(id+"F0.wireOp",EDGE,"E209"),sQuery(id+"F0.wireOp",EDGE,"E210"),sQuery(id+"F0.wireOp",EDGE,"E211"),sQuery(id+"F0.wireOp",EDGE,"E212"),sQuery(id+"F0.wireOp",EDGE,"E213"),sQuery(id+"F0.wireOp",EDGE,"E214"),sQuery(id+"F0.wireOp",EDGE,"E215"),sQuery(id+"F0.wireOp",EDGE,"E216"),sQuery(id+"F0.wireOp",EDGE,"E217"),sQuery(id+"F0.wireOp",EDGE,"E218"),sQuery(id+"F0.wireOp",EDGE,"E219"),sQuery(id+"F0.wireOp",EDGE,"E220"),sQuery(id+"F0.wireOp",EDGE,"E221"),sQuery(id+"F0.wireOp",EDGE,"E222"),sQuery(id+"F0.wireOp",EDGE,"E223"),sQuery(id+"F0.wireOp",EDGE,"E224"),sQuery(id+"F0.wireOp",EDGE,"E225"),sQuery(id+"F0.wireOp",EDGE,"E226"),sQuery(id+"F0.wireOp",EDGE,"E227"),sQuery(id+"F0.wireOp",EDGE,"E228"),sQuery(id+"F0.wireOp",EDGE,"E229"),sQuery(id+"F0.wireOp",EDGE,"E230"),sQuery(id+"F0.wireOp",EDGE,"E231"),sQuery(id+"F0.wireOp",EDGE,"E232"),sQuery(id+"F0.wireOp",EDGE,"E233"),sQuery(id+"F0.wireOp",EDGE,"E234"),sQuery(id+"F0.wireOp",EDGE,"E235"),sQuery(id+"F0.wireOp",EDGE,"E236"),sQuery(id+"F0.wireOp",EDGE,"E237"),sQuery(id+"F0.wireOp",EDGE,"E238"),sQuery(id+"F0.wireOp",EDGE,"E239"),sQuery(id+"F0.wireOp",EDGE,"E240"),sQuery(id+"F0.wireOp",EDGE,"E241"),sQuery(id+"F0.wireOp",EDGE,"E242"),sQuery(id+"F0.wireOp",EDGE,"E243"),sQuery(id+"F0.wireOp",EDGE,"E244"),sQuery(id+"F0.wireOp",EDGE,"E245"),sQuery(id+"F0.wireOp",EDGE,"E246"),sQuery(id+"F0.wireOp",EDGE,"E247"),sQuery(id+"F0.wireOp",EDGE,"E248"),sQuery(id+"F0.wireOp",EDGE,"E249"),sQuery(id+"F0.wireOp",EDGE,"E250"),sQuery(id+"F0.wireOp",EDGE,"E251"),sQuery(id+"F0.wireOp",EDGE,"E252"),sQuery(id+"F0.wireOp",EDGE,"E253"),sQuery(id+"F0.wireOp",EDGE,"E254"),sQuery(id+"F0.wireOp",EDGE,"E255"),sQuery(id+"F0.wireOp",EDGE,"E256"),sQuery(id+"F0.wireOp",EDGE,"E257"),sQuery(id+"F0.wireOp",EDGE,"E258"),sQuery(id+"F0.wireOp",EDGE,"E259"),sQuery(id+"F0.wireOp",EDGE,"E260"),sQuery(id+"F0.wireOp",EDGE,"E261"),sQuery(id+"F0.wireOp",EDGE,"E262"),sQuery(id+"F0.wireOp",EDGE,"E263"),sQuery(id+"F0.wireOp",EDGE,"E264"),sQuery(id+"F0.wireOp",EDGE,"E265"),sQuery(id+"F0.wireOp",EDGE,"E266"),sQuery(id+"F0.wireOp",EDGE,"E267"),sQuery(id+"F0.wireOp",EDGE,"E268"),sQuery(id+"F0.wireOp",EDGE,"E269"),sQuery(id+"F0.wireOp",EDGE,"E270"),sQuery(id+"F0.wireOp",EDGE,"E271"),sQuery(id+"F0.wireOp",EDGE,"E272"),sQuery(id+"F0.wireOp",EDGE,"E273"),sQuery(id+"F0.wireOp",EDGE,"E274"),sQuery(id+"F0.wireOp",EDGE,"E275"),sQuery(id+"F0.wireOp",EDGE,"E276"),sQuery(id+"F0.wireOp",EDGE,"E277"),sQuery(id+"F0.wireOp",EDGE,"E278"),sQuery(id+"F0.wireOp",EDGE,"E279"),sQuery(id+"F0.wireOp",EDGE,"E280"),sQuery(id+"F0.wireOp",EDGE,"E281"),sQuery(id+"F0.wireOp",EDGE,"E282"),sQuery(id+"F0.wireOp",EDGE,"E283"),sQuery(id+"F0.wireOp",EDGE,"E284"),sQuery(id+"F0.wireOp",EDGE,"E285"),sQuery(id+"F0.wireOp",EDGE,"E286"),sQuery(id+"F0.wireOp",EDGE,"E287"),sQuery(id+"F0.wireOp",EDGE,"E288"),sQuery(id+"F0.wireOp",EDGE,"E289"),sQuery(id+"F0.wireOp",EDGE,"E290"),sQuery(id+"F0.wireOp",EDGE,"E291"),sQuery(id+"F0.wireOp",EDGE,"E292"),sQuery(id+"F0.wireOp",EDGE,"E293"),sQuery(id+"F0.wireOp",EDGE,"E294"),sQuery(id+"F0.wireOp",EDGE,"E295"),sQuery(id+"F0.wireOp",EDGE,"E296"),sQuery(id+"F0.wireOp",EDGE,"E297"),sQuery(id+"F0.wireOp",EDGE,"E298"),sQuery(id+"F0.wireOp",EDGE,"E299"),sQuery(id+"F0.wireOp",EDGE,"E300"),sQuery(id+"F0.wireOp",EDGE,"E301"),sQuery(id+"F0.wireOp",EDGE,"E302"),sQuery(id+"F0.wireOp",EDGE,"E303"),sQuery(id+"F0.wireOp",EDGE,"E304"),sQuery(id+"F0.wireOp",EDGE,"E305"),sQuery(id+"F0.wireOp",EDGE,"E306"),sQuery(id+"F0.wireOp",EDGE,"E307"),sQuery(id+"F0.wireOp",EDGE,"E308"),sQuery(id+"F0.wireOp",EDGE,"E309"),sQuery(id+"F0.wireOp",EDGE,"E310"),sQuery(id+"F0.wireOp",EDGE,"E311"),sQuery(id+"F0.wireOp",EDGE,"E312"),sQuery(id+"F0.wireOp",EDGE,"E313"),sQuery(id+"F0.wireOp",EDGE,"E314"),sQuery(id+"F0.wireOp",EDGE,"E315"),sQuery(id+"F0.wireOp",EDGE,"E316"),sQuery(id+"F0.wireOp",EDGE,"E317"),sQuery(id+"F0.wireOp",EDGE,"E318"),sQuery(id+"F0.wireOp",EDGE,"E319"),sQuery(id+"F0.wireOp",EDGE,"E320"),sQuery(id+"F0.wireOp",EDGE,"E321"),sQuery(id+"F0.wireOp",EDGE,"E322"),sQuery(id+"F0.wireOp",EDGE,"E323"),sQuery(id+"F0.wireOp",EDGE,"E324"),sQuery(id+"F0.wireOp",EDGE,"E325"),sQuery(id+"F0.wireOp",EDGE,"E326"),sQuery(id+"F0.wireOp",EDGE,"E327"),sQuery(id+"F0.wireOp",EDGE,"E328"),sQuery(id+"F0.wireOp",EDGE,"E329"),sQuery(id+"F0.wireOp",EDGE,"E330"),sQuery(id+"F0.wireOp",EDGE,"E331"),sQuery(id+"F0.wireOp",EDGE,"E332"),sQuery(id+"F0.wireOp",EDGE,"E333"),sQuery(id+"F0.wireOp",EDGE,"E334"),sQuery(id+"F0.wireOp",EDGE,"E335"),sQuery(id+"F0.wireOp",EDGE,"E336"),sQuery(id+"F0.wireOp",EDGE,"E337"),sQuery(id+"F0.wireOp",EDGE,"E338"),sQuery(id+"F0.wireOp",EDGE,"E339"),sQuery(id+"F0.wireOp",EDGE,"E340"),sQuery(id+"F0.wireOp",EDGE,"E341"),sQuery(id+"F0.wireOp",EDGE,"E342"),sQuery(id+"F0.wireOp",EDGE,"E343"),sQuery(id+"F0.wireOp",EDGE,"E344"),sQuery(id+"F0.wireOp",EDGE,"E345"),sQuery(id+"F0.wireOp",EDGE,"E346"),sQuery(id+"F0.wireOp",EDGE,"E347"),sQuery(id+"F0.wireOp",EDGE,"E348"),sQuery(id+"F0.wireOp",EDGE,"E349"),sQuery(id+"F0.wireOp",EDGE,"E350"),sQuery(id+"F0.wireOp",EDGE,"E351"),sQuery(id+"F0.wireOp",EDGE,"E352"),sQuery(id+"F0.wireOp",EDGE,"E353"),sQuery(id+"F0.wireOp",EDGE,"E354"),sQuery(id+"F0.wireOp",EDGE,"E355"),sQuery(id+"F0.wireOp",EDGE,"E356"),sQuery(id+"F0.wireOp",EDGE,"E357"),sQuery(id+"F0.wireOp",EDGE,"E358"),sQuery(id+"F0.wireOp",EDGE,"E359"),sQuery(id+"F0.wireOp",EDGE,"E360"),sQuery(id+"F0.wireOp",EDGE,"E361"),sQuery(id+"F0.wireOp",EDGE,"E362"),sQuery(id+"F0.wireOp",EDGE,"E363"),sQuery(id+"F0.wireOp",EDGE,"E364"),sQuery(id+"F0.wireOp",EDGE,"E365"),sQuery(id+"F0.wireOp",EDGE,"E366"),sQuery(id+"F0.wireOp",EDGE,"E367"),sQuery(id+"F0.wireOp",EDGE,"E368"),sQuery(id+"F0.wireOp",EDGE,"E369"),sQuery(id+"F0.wireOp",EDGE,"E370"),sQuery(id+"F0.wireOp",EDGE,"E371"),sQuery(id+"F0.wireOp",EDGE,"E372"),sQuery(id+"F0.wireOp",EDGE,"E373"),sQuery(id+"F0.wireOp",EDGE,"E374"),sQuery(id+"F0.wireOp",EDGE,"E375"),sQuery(id+"F0.wireOp",EDGE,"E376"),sQuery(id+"F0.wireOp",EDGE,"E377"),sQuery(id+"F0.wireOp",EDGE,"E378"),sQuery(id+"F0.wireOp",EDGE,"E379"),sQuery(id+"F0.wireOp",EDGE,"E380"),sQuery(id+"F0.wireOp",EDGE,"E381"),sQuery(id+"F0.wireOp",EDGE,"E382"),sQuery(id+"F0.wireOp",EDGE,"E383"),sQuery(id+"F0.wireOp",EDGE,"E384"),sQuery(id+"F0.wireOp",EDGE,"E385"),sQuery(id+"F0.wireOp",EDGE,"E386"),sQuery(id+"F0.wireOp",EDGE,"E387"),sQuery(id+"F0.wireOp",EDGE,"E388"),sQuery(id+"F0.wireOp",EDGE,"E389"),sQuery(id+"F0.wireOp",EDGE,"E390"),sQuery(id+"F0.wireOp",EDGE,"E391"),sQuery(id+"F0.wireOp",EDGE,"E392"),sQuery(id+"F0.wireOp",EDGE,"E393"),sQuery(id+"F0.wireOp",EDGE,"E394"),sQuery(id+"F0.wireOp",EDGE,"E395"),sQuery(id+"F0.wireOp",EDGE,"E396"),sQuery(id+"F0.wireOp",EDGE,"E397"),sQuery(id+"F0.wireOp",EDGE,"E398"),sQuery(id+"F0.wireOp",EDGE,"E399"),sQuery(id+"F0.wireOp",EDGE,"E400"),sQuery(id+"F0.wireOp",EDGE,"E401"),sQuery(id+"F0.wireOp",EDGE,"E402"),sQuery(id+"F0.wireOp",EDGE,"E403"),sQuery(id+"F0.wireOp",EDGE,"E404"),sQuery(id+"F0.wireOp",EDGE,"E405"),sQuery(id+"F0.wireOp",EDGE,"E406"),sQuery(id+"F0.wireOp",EDGE,"E407"),sQuery(id+"F0.wireOp",EDGE,"E408"),sQuery(id+"F0.wireOp",EDGE,"E409"),sQuery(id+"F0.wireOp",EDGE,"E410"),sQuery(id+"F0.wireOp",EDGE,"E411"),sQuery(id+"F0.wireOp",EDGE,"E412"),sQuery(id+"F0.wireOp",EDGE,"E413"),sQuery(id+"F0.wireOp",EDGE,"E414"),sQuery(id+"F0.wireOp",EDGE,"E415"),sQuery(id+"F0.wireOp",EDGE,"E416"),sQuery(id+"F0.wireOp",EDGE,"E417"),sQuery(id+"F0.wireOp",EDGE,"E418"),sQuery(id+"F0.wireOp",EDGE,"E419"),sQuery(id+"F0.wireOp",EDGE,"E420"),sQuery(id+"F0.wireOp",EDGE,"E421"),sQuery(id+"F0.wireOp",EDGE,"E422"),sQuery(id+"F0.wireOp",EDGE,"E423"),sQuery(id+"F0.wireOp",EDGE,"E424"),sQuery(id+"F0.wireOp",EDGE,"E425"),sQuery(id+"F0.wireOp",EDGE,"E426"),sQuery(id+"F0.wireOp",EDGE,"E427"),sQuery(id+"F0.wireOp",EDGE,"E428"),sQuery(id+"F0.wireOp",EDGE,"E429"),sQuery(id+"F0.wireOp",EDGE,"E430"),sQuery(id+"F0.wireOp",EDGE,"E431"),sQuery(id+"F0.wireOp",EDGE,"E432"),sQuery(id+"F0.wireOp",EDGE,"E433"),sQuery(id+"F0.wireOp",EDGE,"E434"),sQuery(id+"F0.wireOp",EDGE,"E435"),sQuery(id+"F0.wireOp",EDGE,"E436"),sQuery(id+"F0.wireOp",EDGE,"E437"),sQuery(id+"F0.wireOp",EDGE,"E438"),sQuery(id+"F0.wireOp",EDGE,"E439"),sQuery(id+"F0.wireOp",EDGE,"E440"),sQuery(id+"F0.wireOp",EDGE,"E441"),sQuery(id+"F0.wireOp",EDGE,"E442"),sQuery(id+"F0.wireOp",EDGE,"E443"),sQuery(id+"F0.wireOp",EDGE,"E444"),sQuery(id+"F0.wireOp",EDGE,"E445"),sQuery(id+"F0.wireOp",EDGE,"E446"),sQuery(id+"F0.wireOp",EDGE,"E447"),sQuery(id+"F0.wireOp",EDGE,"E448"),sQuery(id+"F0.wireOp",EDGE,"E449"),sQuery(id+"F0.wireOp",EDGE,"E450"),sQuery(id+"F0.wireOp",EDGE,"E451"),sQuery(id+"F0.wireOp",EDGE,"E452"),sQuery(id+"F0.wireOp",EDGE,"E453"),sQuery(id+"F0.wireOp",EDGE,"E454"),sQuery(id+"F0.wireOp",EDGE,"E455"),sQuery(id+"F0.wireOp",EDGE,"E456"),sQuery(id+"F0.wireOp",EDGE,"E457"),sQuery(id+"F0.wireOp",EDGE,"E458"),sQuery(id+"F0.wireOp",EDGE,"E459"),sQuery(id+"F0.wireOp",EDGE,"E460"),sQuery(id+"F0.wireOp",EDGE,"E461"),sQuery(id+"F0.wireOp",EDGE,"E462"),sQuery(id+"F0.wireOp",EDGE,"E463"),sQuery(id+"F0.wireOp",EDGE,"E464"),sQuery(id+"F0.wireOp",EDGE,"E465"),sQuery(id+"F0.wireOp",EDGE,"E466"),sQuery(id+"F0.wireOp",EDGE,"E467"),sQuery(id+"F0.wireOp",EDGE,"E468"),sQuery(id+"F0.wireOp",EDGE,"E469"),sQuery(id+"F0.wireOp",EDGE,"E470"),sQuery(id+"F0.wireOp",EDGE,"E471"),sQuery(id+"F0.wireOp",EDGE,"E472"),sQuery(id+"F0.wireOp",EDGE,"E473"),sQuery(id+"F0.wireOp",EDGE,"E474"),sQuery(id+"F0.wireOp",EDGE,"E475"),sQuery(id+"F0.wireOp",EDGE,"E476"),sQuery(id+"F0.wireOp",EDGE,"E477"),sQuery(id+"F0.wireOp",EDGE,"E478"),sQuery(id+"F0.wireOp",EDGE,"E479"),sQuery(id+"F0.wireOp",EDGE,"E480"),sQuery(id+"F0.wireOp",EDGE,"E481"),sQuery(id+"F0.wireOp",EDGE,"E482"),sQuery(id+"F0.wireOp",EDGE,"E483"),sQuery(id+"F0.wireOp",EDGE,"E484"),sQuery(id+"F0.wireOp",EDGE,"E485"),sQuery(id+"F0.wireOp",EDGE,"E486"),sQuery(id+"F0.wireOp",EDGE,"E487"),sQuery(id+"F0.wireOp",EDGE,"E488"),sQuery(id+"F0.wireOp",EDGE,"E489"),sQuery(id+"F0.wireOp",EDGE,"E490"),sQuery(id+"F0.wireOp",EDGE,"E491"),sQuery(id+"F0.wireOp",EDGE,"E492"),sQuery(id+"F0.wireOp",EDGE,"E493"),sQuery(id+"F0.wireOp",EDGE,"E494"),sQuery(id+"F0.wireOp",EDGE,"E495"),sQuery(id+"F0.wireOp",EDGE,"E496"),sQuery(id+"F0.wireOp",EDGE,"E497"),sQuery(id+"F0.wireOp",EDGE,"E498"),sQuery(id+"F0.wireOp",EDGE,"E499"),sQuery(id+"F0.wireOp",EDGE,"E500"),sQuery(id+"F0.wireOp",EDGE,"E501"),sQuery(id+"F0.wireOp",EDGE,"E502"),sQuery(id+"F0.wireOp",EDGE,"E503"),sQuery(id+"F0.wireOp",EDGE,"E504"),sQuery(id+"F0.wireOp",EDGE,"E505"),sQuery(id+"F0.wireOp",EDGE,"E506"),sQuery(id+"F0.wireOp",EDGE,"E507"),sQuery(id+"F0.wireOp",EDGE,"E508"),sQuery(id+"F0.wireOp",EDGE,"E509"),sQuery(id+"F0.wireOp",EDGE,"E510"),sQuery(id+"F0.wireOp",EDGE,"E511"),sQuery(id+"F0.wireOp",EDGE,"E512"),sQuery(id+"F0.wireOp",EDGE,"E513"),sQuery(id+"F0.wireOp",EDGE,"E514"),sQuery(id+"F0.wireOp",EDGE,"E515"),sQuery(id+"F0.wireOp",EDGE,"E516"),sQuery(id+"F0.wireOp",EDGE,"E517"),sQuery(id+"F0.wireOp",EDGE,"E518"),sQuery(id+"F0.wireOp",EDGE,"E519"),sQuery(id+"F0.wireOp",EDGE,"E520"),sQuery(id+"F0.wireOp",EDGE,"E521"),sQuery(id+"F0.wireOp",EDGE,"E522"),sQuery(id+"F0.wireOp",EDGE,"E523"),sQuery(id+"F0.wireOp",EDGE,"E524"),sQuery(id+"F0.wireOp",EDGE,"E525"),sQuery(id+"F0.wireOp",EDGE,"E526"),sQuery(id+"F0.wireOp",EDGE,"E527"),sQuery(id+"F0.wireOp",EDGE,"E528"),sQuery(id+"F0.wireOp",EDGE,"E529"),sQuery(id+"F0.wireOp",EDGE,"E530"),sQuery(id+"F0.wireOp",EDGE,"E531"),sQuery(id+"F0.wireOp",EDGE,"E532"),sQuery(id+"F0.wireOp",EDGE,"E533"),sQuery(id+"F0.wireOp",EDGE,"E534"),sQuery(id+"F0.wireOp",EDGE,"E535"),sQuery(id+"F0.wireOp",EDGE,"E536"),sQuery(id+"F0.wireOp",EDGE,"E537"),sQuery(id+"F0.wireOp",EDGE,"E538"),sQuery(id+"F0.wireOp",EDGE,"E539"),sQuery(id+"F0.wireOp",EDGE,"E540"),sQuery(id+"F0.wireOp",EDGE,"E541"),sQuery(id+"F0.wireOp",EDGE,"E542"),sQuery(id+"F0.wireOp",EDGE,"E543"),sQuery(id+"F0.wireOp",EDGE,"E544"),sQuery(id+"F0.wireOp",EDGE,"E545"),sQuery(id+"F0.wireOp",EDGE,"E546"),sQuery(id+"F0.wireOp",EDGE,"E547"),sQuery(id+"F0.wireOp",EDGE,"E548"),sQuery(id+"F0.wireOp",EDGE,"E549"),sQuery(id+"F0.wireOp",EDGE,"E550"),sQuery(id+"F0.wireOp",EDGE,"E551"),sQuery(id+"F0.wireOp",EDGE,"E552"),sQuery(id+"F0.wireOp",EDGE,"E553"),sQuery(id+"F0.wireOp",EDGE,"E554"),sQuery(id+"F0.wireOp",EDGE,"E555"),sQuery(id+"F0.wireOp",EDGE,"E556"),sQuery(id+"F0.wireOp",EDGE,"E557"),sQuery(id+"F0.wireOp",EDGE,"E558"),sQuery(id+"F0.wireOp",EDGE,"E559"),sQuery(id+"F0.wireOp",EDGE,"E560"),sQuery(id+"F0.wireOp",EDGE,"E561"),sQuery(id+"F0.wireOp",EDGE,"E562"),sQuery(id+"F0.wireOp",EDGE,"E563"),sQuery(id+"F0.wireOp",EDGE,"E564"),sQuery(id+"F0.wireOp",EDGE,"E565"),sQuery(id+"F0.wireOp",EDGE,"E566"),sQuery(id+"F0.wireOp",EDGE,"E567"),sQuery(id+"F0.wireOp",EDGE,"E568"),sQuery(id+"F0.wireOp",EDGE,"E569"),sQuery(id+"F0.wireOp",EDGE,"E570"),sQuery(id+"F0.wireOp",EDGE,"E571"),sQuery(id+"F0.wireOp",EDGE,"E572"),sQuery(id+"F0.wireOp",EDGE,"E573"),sQuery(id+"F0.wireOp",EDGE,"E574"),sQuery(id+"F0.wireOp",EDGE,"E575"),sQuery(id+"F0.wireOp",EDGE,"E576"),sQuery(id+"F0.wireOp",EDGE,"E577"),sQuery(id+"F0.wireOp",EDGE,"E578"),sQuery(id+"F0.wireOp",EDGE,"E579"),sQuery(id+"F0.wireOp",EDGE,"E580"),sQuery(id+"F0.wireOp",EDGE,"E581"),sQuery(id+"F0.wireOp",EDGE,"E582"),sQuery(id+"F0.wireOp",EDGE,"E583"),sQuery(id+"F0.wireOp",EDGE,"E584"),sQuery(id+"F0.wireOp",EDGE,"E585"),sQuery(id+"F0.wireOp",EDGE,"E586"),sQuery(id+"F0.wireOp",EDGE,"E587"),sQuery(id+"F0.wireOp",EDGE,"E588"),sQuery(id+"F0.wireOp",EDGE,"E589"),sQuery(id+"F0.wireOp",EDGE,"E590"),sQuery(id+"F0.wireOp",EDGE,"E591")])]});
            transform(context, id + "F3", {"entities" : qUnion([Q0, Q1]), "transformType" : TransformType.TRANSLATION_3D, "dx" : 0 * mm, "dy" : 0 * mm, "dz" : 0 * mm, "makeCopy" : false});
        }
        {
            var Q0;
            Q0=makeQuery(id+"F1.opExtrude","SWEPT_BODY",BODY,{"disambiguationData":[OSD([sQuery(id+"F0.wireOp",EDGE,"E0"),sQuery(id+"F0.wireOp",EDGE,"E1"),sQuery(id+"F0.wireOp",EDGE,"E2"),sQuery(id+"F0.wireOp",EDGE,"E3"),sQuery(id+"F0.wireOp",EDGE,"E4"),sQuery(id+"F0.wireOp",EDGE,"E5"),sQuery(id+"F0.wireOp",EDGE,"E6"),sQuery(id+"F0.wireOp",EDGE,"E7"),sQuery(id+"F0.wireOp",EDGE,"E8"),sQuery(id+"F0.wireOp",EDGE,"E9"),sQuery(id+"F0.wireOp",EDGE,"E10"),sQuery(id+"F0.wireOp",EDGE,"E11"),sQuery(id+"F0.wireOp",EDGE,"E12"),sQuery(id+"F0.wireOp",EDGE,"E13"),sQuery(id+"F0.wireOp",EDGE,"E14"),sQuery(id+"F0.wireOp",EDGE,"E15"),sQuery(id+"F0.wireOp",EDGE,"E16"),sQuery(id+"F0.wireOp",EDGE,"E17"),sQuery(id+"F0.wireOp",EDGE,"E18"),sQuery(id+"F0.wireOp",EDGE,"E19"),sQuery(id+"F0.wireOp",EDGE,"E20"),sQuery(id+"F0.wireOp",EDGE,"E21"),sQuery(id+"F0.wireOp",EDGE,"E22"),sQuery(id+"F0.wireOp",EDGE,"E23"),sQuery(id+"F0.wireOp",EDGE,"E24"),sQuery(id+"F0.wireOp",EDGE,"E25"),sQuery(id+"F0.wireOp",EDGE,"E26"),sQuery(id+"F0.wireOp",EDGE,"E27"),sQuery(id+"F0.wireOp",EDGE,"E28"),sQuery(id+"F0.wireOp",EDGE,"E29"),sQuery(id+"F0.wireOp",EDGE,"E30"),sQuery(id+"F0.wireOp",EDGE,"E31"),sQuery(id+"F0.wireOp",EDGE,"E32"),sQuery(id+"F0.wireOp",EDGE,"E33"),sQuery(id+"F0.wireOp",EDGE,"E34"),sQuery(id+"F0.wireOp",EDGE,"E35"),sQuery(id+"F0.wireOp",EDGE,"E36"),sQuery(id+"F0.wireOp",EDGE,"E37"),sQuery(id+"F0.wireOp",EDGE,"E38"),sQuery(id+"F0.wireOp",EDGE,"E39"),sQuery(id+"F0.wireOp",EDGE,"E40"),sQuery(id+"F0.wireOp",EDGE,"E41"),sQuery(id+"F0.wireOp",EDGE,"E42"),sQuery(id+"F0.wireOp",EDGE,"E43"),sQuery(id+"F0.wireOp",EDGE,"E44"),sQuery(id+"F0.wireOp",EDGE,"E45"),sQuery(id+"F0.wireOp",EDGE,"E46"),sQuery(id+"F0.wireOp",EDGE,"E47"),sQuery(id+"F0.wireOp",EDGE,"E48"),sQuery(id+"F0.wireOp",EDGE,"E49"),sQuery(id+"F0.wireOp",EDGE,"E50"),sQuery(id+"F0.wireOp",EDGE,"E51"),sQuery(id+"F0.wireOp",EDGE,"E52"),sQuery(id+"F0.wireOp",EDGE,"E53"),sQuery(id+"F0.wireOp",EDGE,"E54"),sQuery(id+"F0.wireOp",EDGE,"E55"),sQuery(id+"F0.wireOp",EDGE,"E56"),sQuery(id+"F0.wireOp",EDGE,"E57"),sQuery(id+"F0.wireOp",EDGE,"E58"),sQuery(id+"F0.wireOp",EDGE,"E59"),sQuery(id+"F0.wireOp",EDGE,"E60"),sQuery(id+"F0.wireOp",EDGE,"E61"),sQuery(id+"F0.wireOp",EDGE,"E62"),sQuery(id+"F0.wireOp",EDGE,"E63"),sQuery(id+"F0.wireOp",EDGE,"E64"),sQuery(id+"F0.wireOp",EDGE,"E65"),sQuery(id+"F0.wireOp",EDGE,"E66"),sQuery(id+"F0.wireOp",EDGE,"E67"),sQuery(id+"F0.wireOp",EDGE,"E68"),sQuery(id+"F0.wireOp",EDGE,"E69"),sQuery(id+"F0.wireOp",EDGE,"E70"),sQuery(id+"F0.wireOp",EDGE,"E71"),sQuery(id+"F0.wireOp",EDGE,"E72"),sQuery(id+"F0.wireOp",EDGE,"E73"),sQuery(id+"F0.wireOp",EDGE,"E74"),sQuery(id+"F0.wireOp",EDGE,"E75"),sQuery(id+"F0.wireOp",EDGE,"E76"),sQuery(id+"F0.wireOp",EDGE,"E77"),sQuery(id+"F0.wireOp",EDGE,"E78"),sQuery(id+"F0.wireOp",EDGE,"E79"),sQuery(id+"F0.wireOp",EDGE,"E80"),sQuery(id+"F0.wireOp",EDGE,"E81"),sQuery(id+"F0.wireOp",EDGE,"E82"),sQuery(id+"F0.wireOp",EDGE,"E83"),sQuery(id+"F0.wireOp",EDGE,"E84"),sQuery(id+"F0.wireOp",EDGE,"E85"),sQuery(id+"F0.wireOp",EDGE,"E86"),sQuery(id+"F0.wireOp",EDGE,"E87"),sQuery(id+"F0.wireOp",EDGE,"E88"),sQuery(id+"F0.wireOp",EDGE,"E89"),sQuery(id+"F0.wireOp",EDGE,"E90"),sQuery(id+"F0.wireOp",EDGE,"E91"),sQuery(id+"F0.wireOp",EDGE,"E92"),sQuery(id+"F0.wireOp",EDGE,"E93"),sQuery(id+"F0.wireOp",EDGE,"E94"),sQuery(id+"F0.wireOp",EDGE,"E95"),sQuery(id+"F0.wireOp",EDGE,"E96"),sQuery(id+"F0.wireOp",EDGE,"E97"),sQuery(id+"F0.wireOp",EDGE,"E98"),sQuery(id+"F0.wireOp",EDGE,"E99"),sQuery(id+"F0.wireOp",EDGE,"E100"),sQuery(id+"F0.wireOp",EDGE,"E101"),sQuery(id+"F0.wireOp",EDGE,"E102"),sQuery(id+"F0.wireOp",EDGE,"E103"),sQuery(id+"F0.wireOp",EDGE,"E104"),sQuery(id+"F0.wireOp",EDGE,"E105"),sQuery(id+"F0.wireOp",EDGE,"E106"),sQuery(id+"F0.wireOp",EDGE,"E107"),sQuery(id+"F0.wireOp",EDGE,"E108"),sQuery(id+"F0.wireOp",EDGE,"E109"),sQuery(id+"F0.wireOp",EDGE,"E110"),sQuery(id+"F0.wireOp",EDGE,"E111"),sQuery(id+"F0.wireOp",EDGE,"E112"),sQuery(id+"F0.wireOp",EDGE,"E113"),sQuery(id+"F0.wireOp",EDGE,"E114"),sQuery(id+"F0.wireOp",EDGE,"E115"),sQuery(id+"F0.wireOp",EDGE,"E116"),sQuery(id+"F0.wireOp",EDGE,"E117"),sQuery(id+"F0.wireOp",EDGE,"E118"),sQuery(id+"F0.wireOp",EDGE,"E119"),sQuery(id+"F0.wireOp",EDGE,"E120"),sQuery(id+"F0.wireOp",EDGE,"E121"),sQuery(id+"F0.wireOp",EDGE,"E122"),sQuery(id+"F0.wireOp",EDGE,"E123"),sQuery(id+"F0.wireOp",EDGE,"E124"),sQuery(id+"F0.wireOp",EDGE,"E125"),sQuery(id+"F0.wireOp",EDGE,"E126"),sQuery(id+"F0.wireOp",EDGE,"E127"),sQuery(id+"F0.wireOp",EDGE,"E128"),sQuery(id+"F0.wireOp",EDGE,"E129"),sQuery(id+"F0.wireOp",EDGE,"E130"),sQuery(id+"F0.wireOp",EDGE,"E131"),sQuery(id+"F0.wireOp",EDGE,"E132"),sQuery(id+"F0.wireOp",EDGE,"E133"),sQuery(id+"F0.wireOp",EDGE,"E134"),sQuery(id+"F0.wireOp",EDGE,"E135"),sQuery(id+"F0.wireOp",EDGE,"E136"),sQuery(id+"F0.wireOp",EDGE,"E137"),sQuery(id+"F0.wireOp",EDGE,"E138"),sQuery(id+"F0.wireOp",EDGE,"E139"),sQuery(id+"F0.wireOp",EDGE,"E140"),sQuery(id+"F0.wireOp",EDGE,"E141"),sQuery(id+"F0.wireOp",EDGE,"E142"),sQuery(id+"F0.wireOp",EDGE,"E143"),sQuery(id+"F0.wireOp",EDGE,"E144"),sQuery(id+"F0.wireOp",EDGE,"E145"),sQuery(id+"F0.wireOp",EDGE,"E146"),sQuery(id+"F0.wireOp",EDGE,"E147"),sQuery(id+"F0.wireOp",EDGE,"E148"),sQuery(id+"F0.wireOp",EDGE,"E149"),sQuery(id+"F0.wireOp",EDGE,"E150"),sQuery(id+"F0.wireOp",EDGE,"E151"),sQuery(id+"F0.wireOp",EDGE,"E152"),sQuery(id+"F0.wireOp",EDGE,"E153"),sQuery(id+"F0.wireOp",EDGE,"E154"),sQuery(id+"F0.wireOp",EDGE,"E155"),sQuery(id+"F0.wireOp",EDGE,"E156"),sQuery(id+"F0.wireOp",EDGE,"E157"),sQuery(id+"F0.wireOp",EDGE,"E158"),sQuery(id+"F0.wireOp",EDGE,"E159"),sQuery(id+"F0.wireOp",EDGE,"E160"),sQuery(id+"F0.wireOp",EDGE,"E161"),sQuery(id+"F0.wireOp",EDGE,"E162"),sQuery(id+"F0.wireOp",EDGE,"E163"),sQuery(id+"F0.wireOp",EDGE,"E164"),sQuery(id+"F0.wireOp",EDGE,"E165"),sQuery(id+"F0.wireOp",EDGE,"E166"),sQuery(id+"F0.wireOp",EDGE,"E167"),sQuery(id+"F0.wireOp",EDGE,"E168"),sQuery(id+"F0.wireOp",EDGE,"E169"),sQuery(id+"F0.wireOp",EDGE,"E170"),sQuery(id+"F0.wireOp",EDGE,"E171"),sQuery(id+"F0.wireOp",EDGE,"E172"),sQuery(id+"F0.wireOp",EDGE,"E173"),sQuery(id+"F0.wireOp",EDGE,"E174"),sQuery(id+"F0.wireOp",EDGE,"E175"),sQuery(id+"F0.wireOp",EDGE,"E176"),sQuery(id+"F0.wireOp",EDGE,"E177"),sQuery(id+"F0.wireOp",EDGE,"E178"),sQuery(id+"F0.wireOp",EDGE,"E179"),sQuery(id+"F0.wireOp",EDGE,"E180"),sQuery(id+"F0.wireOp",EDGE,"E181"),sQuery(id+"F0.wireOp",EDGE,"E182"),sQuery(id+"F0.wireOp",EDGE,"E183"),sQuery(id+"F0.wireOp",EDGE,"E184"),sQuery(id+"F0.wireOp",EDGE,"E185"),sQuery(id+"F0.wireOp",EDGE,"E186"),sQuery(id+"F0.wireOp",EDGE,"E187"),sQuery(id+"F0.wireOp",EDGE,"E188"),sQuery(id+"F0.wireOp",EDGE,"E189"),sQuery(id+"F0.wireOp",EDGE,"E190"),sQuery(id+"F0.wireOp",EDGE,"E191"),sQuery(id+"F0.wireOp",EDGE,"E192"),sQuery(id+"F0.wireOp",EDGE,"E193"),sQuery(id+"F0.wireOp",EDGE,"E194"),sQuery(id+"F0.wireOp",EDGE,"E195"),sQuery(id+"F0.wireOp",EDGE,"E196"),sQuery(id+"F0.wireOp",EDGE,"E197"),sQuery(id+"F0.wireOp",EDGE,"E198"),sQuery(id+"F0.wireOp",EDGE,"E199"),sQuery(id+"F0.wireOp",EDGE,"E200"),sQuery(id+"F0.wireOp",EDGE,"E201"),sQuery(id+"F0.wireOp",EDGE,"E202"),sQuery(id+"F0.wireOp",EDGE,"E203"),sQuery(id+"F0.wireOp",EDGE,"E204"),sQuery(id+"F0.wireOp",EDGE,"E205"),sQuery(id+"F0.wireOp",EDGE,"E206"),sQuery(id+"F0.wireOp",EDGE,"E207"),sQuery(id+"F0.wireOp",EDGE,"E208"),sQuery(id+"F0.wireOp",EDGE,"E209"),sQuery(id+"F0.wireOp",EDGE,"E210"),sQuery(id+"F0.wireOp",EDGE,"E211"),sQuery(id+"F0.wireOp",EDGE,"E212"),sQuery(id+"F0.wireOp",EDGE,"E213"),sQuery(id+"F0.wireOp",EDGE,"E214"),sQuery(id+"F0.wireOp",EDGE,"E215"),sQuery(id+"F0.wireOp",EDGE,"E216"),sQuery(id+"F0.wireOp",EDGE,"E217"),sQuery(id+"F0.wireOp",EDGE,"E218"),sQuery(id+"F0.wireOp",EDGE,"E219"),sQuery(id+"F0.wireOp",EDGE,"E220"),sQuery(id+"F0.wireOp",EDGE,"E221"),sQuery(id+"F0.wireOp",EDGE,"E222"),sQuery(id+"F0.wireOp",EDGE,"E223"),sQuery(id+"F0.wireOp",EDGE,"E224"),sQuery(id+"F0.wireOp",EDGE,"E225"),sQuery(id+"F0.wireOp",EDGE,"E226"),sQuery(id+"F0.wireOp",EDGE,"E227"),sQuery(id+"F0.wireOp",EDGE,"E228"),sQuery(id+"F0.wireOp",EDGE,"E229"),sQuery(id+"F0.wireOp",EDGE,"E230"),sQuery(id+"F0.wireOp",EDGE,"E231"),sQuery(id+"F0.wireOp",EDGE,"E232"),sQuery(id+"F0.wireOp",EDGE,"E233"),sQuery(id+"F0.wireOp",EDGE,"E234"),sQuery(id+"F0.wireOp",EDGE,"E235"),sQuery(id+"F0.wireOp",EDGE,"E236"),sQuery(id+"F0.wireOp",EDGE,"E237"),sQuery(id+"F0.wireOp",EDGE,"E238"),sQuery(id+"F0.wireOp",EDGE,"E239"),sQuery(id+"F0.wireOp",EDGE,"E240"),sQuery(id+"F0.wireOp",EDGE,"E241"),sQuery(id+"F0.wireOp",EDGE,"E242"),sQuery(id+"F0.wireOp",EDGE,"E243"),sQuery(id+"F0.wireOp",EDGE,"E244"),sQuery(id+"F0.wireOp",EDGE,"E245"),sQuery(id+"F0.wireOp",EDGE,"E246"),sQuery(id+"F0.wireOp",EDGE,"E247"),sQuery(id+"F0.wireOp",EDGE,"E248"),sQuery(id+"F0.wireOp",EDGE,"E249"),sQuery(id+"F0.wireOp",EDGE,"E250"),sQuery(id+"F0.wireOp",EDGE,"E251"),sQuery(id+"F0.wireOp",EDGE,"E252"),sQuery(id+"F0.wireOp",EDGE,"E253"),sQuery(id+"F0.wireOp",EDGE,"E254"),sQuery(id+"F0.wireOp",EDGE,"E255"),sQuery(id+"F0.wireOp",EDGE,"E256"),sQuery(id+"F0.wireOp",EDGE,"E257"),sQuery(id+"F0.wireOp",EDGE,"E258"),sQuery(id+"F0.wireOp",EDGE,"E259"),sQuery(id+"F0.wireOp",EDGE,"E260"),sQuery(id+"F0.wireOp",EDGE,"E261"),sQuery(id+"F0.wireOp",EDGE,"E262"),sQuery(id+"F0.wireOp",EDGE,"E263"),sQuery(id+"F0.wireOp",EDGE,"E264"),sQuery(id+"F0.wireOp",EDGE,"E265"),sQuery(id+"F0.wireOp",EDGE,"E266"),sQuery(id+"F0.wireOp",EDGE,"E267"),sQuery(id+"F0.wireOp",EDGE,"E268"),sQuery(id+"F0.wireOp",EDGE,"E269"),sQuery(id+"F0.wireOp",EDGE,"E270"),sQuery(id+"F0.wireOp",EDGE,"E271"),sQuery(id+"F0.wireOp",EDGE,"E272"),sQuery(id+"F0.wireOp",EDGE,"E273"),sQuery(id+"F0.wireOp",EDGE,"E274"),sQuery(id+"F0.wireOp",EDGE,"E275"),sQuery(id+"F0.wireOp",EDGE,"E276"),sQuery(id+"F0.wireOp",EDGE,"E277"),sQuery(id+"F0.wireOp",EDGE,"E278"),sQuery(id+"F0.wireOp",EDGE,"E279"),sQuery(id+"F0.wireOp",EDGE,"E280"),sQuery(id+"F0.wireOp",EDGE,"E281"),sQuery(id+"F0.wireOp",EDGE,"E282"),sQuery(id+"F0.wireOp",EDGE,"E283"),sQuery(id+"F0.wireOp",EDGE,"E284"),sQuery(id+"F0.wireOp",EDGE,"E285"),sQuery(id+"F0.wireOp",EDGE,"E286"),sQuery(id+"F0.wireOp",EDGE,"E287"),sQuery(id+"F0.wireOp",EDGE,"E288"),sQuery(id+"F0.wireOp",EDGE,"E289"),sQuery(id+"F0.wireOp",EDGE,"E290"),sQuery(id+"F0.wireOp",EDGE,"E291"),sQuery(id+"F0.wireOp",EDGE,"E292"),sQuery(id+"F0.wireOp",EDGE,"E293"),sQuery(id+"F0.wireOp",EDGE,"E294"),sQuery(id+"F0.wireOp",EDGE,"E295"),sQuery(id+"F0.wireOp",EDGE,"E296"),sQuery(id+"F0.wireOp",EDGE,"E297"),sQuery(id+"F0.wireOp",EDGE,"E298"),sQuery(id+"F0.wireOp",EDGE,"E299"),sQuery(id+"F0.wireOp",EDGE,"E300"),sQuery(id+"F0.wireOp",EDGE,"E301"),sQuery(id+"F0.wireOp",EDGE,"E302"),sQuery(id+"F0.wireOp",EDGE,"E303"),sQuery(id+"F0.wireOp",EDGE,"E304"),sQuery(id+"F0.wireOp",EDGE,"E305"),sQuery(id+"F0.wireOp",EDGE,"E306"),sQuery(id+"F0.wireOp",EDGE,"E307"),sQuery(id+"F0.wireOp",EDGE,"E308"),sQuery(id+"F0.wireOp",EDGE,"E309"),sQuery(id+"F0.wireOp",EDGE,"E310"),sQuery(id+"F0.wireOp",EDGE,"E311"),sQuery(id+"F0.wireOp",EDGE,"E312"),sQuery(id+"F0.wireOp",EDGE,"E313"),sQuery(id+"F0.wireOp",EDGE,"E314"),sQuery(id+"F0.wireOp",EDGE,"E315"),sQuery(id+"F0.wireOp",EDGE,"E316"),sQuery(id+"F0.wireOp",EDGE,"E317"),sQuery(id+"F0.wireOp",EDGE,"E318"),sQuery(id+"F0.wireOp",EDGE,"E319"),sQuery(id+"F0.wireOp",EDGE,"E320"),sQuery(id+"F0.wireOp",EDGE,"E321"),sQuery(id+"F0.wireOp",EDGE,"E322"),sQuery(id+"F0.wireOp",EDGE,"E323"),sQuery(id+"F0.wireOp",EDGE,"E324"),sQuery(id+"F0.wireOp",EDGE,"E325"),sQuery(id+"F0.wireOp",EDGE,"E326"),sQuery(id+"F0.wireOp",EDGE,"E327"),sQuery(id+"F0.wireOp",EDGE,"E328"),sQuery(id+"F0.wireOp",EDGE,"E329"),sQuery(id+"F0.wireOp",EDGE,"E330"),sQuery(id+"F0.wireOp",EDGE,"E331"),sQuery(id+"F0.wireOp",EDGE,"E332"),sQuery(id+"F0.wireOp",EDGE,"E333"),sQuery(id+"F0.wireOp",EDGE,"E334"),sQuery(id+"F0.wireOp",EDGE,"E335"),sQuery(id+"F0.wireOp",EDGE,"E336"),sQuery(id+"F0.wireOp",EDGE,"E337"),sQuery(id+"F0.wireOp",EDGE,"E338"),sQuery(id+"F0.wireOp",EDGE,"E339"),sQuery(id+"F0.wireOp",EDGE,"E340"),sQuery(id+"F0.wireOp",EDGE,"E341"),sQuery(id+"F0.wireOp",EDGE,"E342"),sQuery(id+"F0.wireOp",EDGE,"E343"),sQuery(id+"F0.wireOp",EDGE,"E344"),sQuery(id+"F0.wireOp",EDGE,"E345"),sQuery(id+"F0.wireOp",EDGE,"E346"),sQuery(id+"F0.wireOp",EDGE,"E347"),sQuery(id+"F0.wireOp",EDGE,"E348"),sQuery(id+"F0.wireOp",EDGE,"E349"),sQuery(id+"F0.wireOp",EDGE,"E350"),sQuery(id+"F0.wireOp",EDGE,"E351"),sQuery(id+"F0.wireOp",EDGE,"E352"),sQuery(id+"F0.wireOp",EDGE,"E353"),sQuery(id+"F0.wireOp",EDGE,"E354"),sQuery(id+"F0.wireOp",EDGE,"E355"),sQuery(id+"F0.wireOp",EDGE,"E356"),sQuery(id+"F0.wireOp",EDGE,"E357"),sQuery(id+"F0.wireOp",EDGE,"E358"),sQuery(id+"F0.wireOp",EDGE,"E359"),sQuery(id+"F0.wireOp",EDGE,"E360"),sQuery(id+"F0.wireOp",EDGE,"E361"),sQuery(id+"F0.wireOp",EDGE,"E362"),sQuery(id+"F0.wireOp",EDGE,"E363"),sQuery(id+"F0.wireOp",EDGE,"E364"),sQuery(id+"F0.wireOp",EDGE,"E365"),sQuery(id+"F0.wireOp",EDGE,"E366"),sQuery(id+"F0.wireOp",EDGE,"E367"),sQuery(id+"F0.wireOp",EDGE,"E368"),sQuery(id+"F0.wireOp",EDGE,"E369"),sQuery(id+"F0.wireOp",EDGE,"E370"),sQuery(id+"F0.wireOp",EDGE,"E371"),sQuery(id+"F0.wireOp",EDGE,"E372"),sQuery(id+"F0.wireOp",EDGE,"E373"),sQuery(id+"F0.wireOp",EDGE,"E374"),sQuery(id+"F0.wireOp",EDGE,"E375"),sQuery(id+"F0.wireOp",EDGE,"E376"),sQuery(id+"F0.wireOp",EDGE,"E377"),sQuery(id+"F0.wireOp",EDGE,"E378"),sQuery(id+"F0.wireOp",EDGE,"E379"),sQuery(id+"F0.wireOp",EDGE,"E380"),sQuery(id+"F0.wireOp",EDGE,"E381"),sQuery(id+"F0.wireOp",EDGE,"E382"),sQuery(id+"F0.wireOp",EDGE,"E383"),sQuery(id+"F0.wireOp",EDGE,"E384"),sQuery(id+"F0.wireOp",EDGE,"E385"),sQuery(id+"F0.wireOp",EDGE,"E386"),sQuery(id+"F0.wireOp",EDGE,"E387"),sQuery(id+"F0.wireOp",EDGE,"E388"),sQuery(id+"F0.wireOp",EDGE,"E389"),sQuery(id+"F0.wireOp",EDGE,"E390"),sQuery(id+"F0.wireOp",EDGE,"E391"),sQuery(id+"F0.wireOp",EDGE,"E392"),sQuery(id+"F0.wireOp",EDGE,"E393"),sQuery(id+"F0.wireOp",EDGE,"E394"),sQuery(id+"F0.wireOp",EDGE,"E395"),sQuery(id+"F0.wireOp",EDGE,"E396"),sQuery(id+"F0.wireOp",EDGE,"E397"),sQuery(id+"F0.wireOp",EDGE,"E398"),sQuery(id+"F0.wireOp",EDGE,"E399"),sQuery(id+"F0.wireOp",EDGE,"E400"),sQuery(id+"F0.wireOp",EDGE,"E401"),sQuery(id+"F0.wireOp",EDGE,"E402"),sQuery(id+"F0.wireOp",EDGE,"E403"),sQuery(id+"F0.wireOp",EDGE,"E404"),sQuery(id+"F0.wireOp",EDGE,"E405"),sQuery(id+"F0.wireOp",EDGE,"E406"),sQuery(id+"F0.wireOp",EDGE,"E407"),sQuery(id+"F0.wireOp",EDGE,"E408"),sQuery(id+"F0.wireOp",EDGE,"E409"),sQuery(id+"F0.wireOp",EDGE,"E410"),sQuery(id+"F0.wireOp",EDGE,"E411"),sQuery(id+"F0.wireOp",EDGE,"E412"),sQuery(id+"F0.wireOp",EDGE,"E413"),sQuery(id+"F0.wireOp",EDGE,"E414"),sQuery(id+"F0.wireOp",EDGE,"E415"),sQuery(id+"F0.wireOp",EDGE,"E416"),sQuery(id+"F0.wireOp",EDGE,"E417"),sQuery(id+"F0.wireOp",EDGE,"E418"),sQuery(id+"F0.wireOp",EDGE,"E419"),sQuery(id+"F0.wireOp",EDGE,"E420"),sQuery(id+"F0.wireOp",EDGE,"E421"),sQuery(id+"F0.wireOp",EDGE,"E422"),sQuery(id+"F0.wireOp",EDGE,"E423"),sQuery(id+"F0.wireOp",EDGE,"E424"),sQuery(id+"F0.wireOp",EDGE,"E425"),sQuery(id+"F0.wireOp",EDGE,"E426"),sQuery(id+"F0.wireOp",EDGE,"E427"),sQuery(id+"F0.wireOp",EDGE,"E428"),sQuery(id+"F0.wireOp",EDGE,"E429"),sQuery(id+"F0.wireOp",EDGE,"E430"),sQuery(id+"F0.wireOp",EDGE,"E431"),sQuery(id+"F0.wireOp",EDGE,"E432"),sQuery(id+"F0.wireOp",EDGE,"E433"),sQuery(id+"F0.wireOp",EDGE,"E434"),sQuery(id+"F0.wireOp",EDGE,"E435"),sQuery(id+"F0.wireOp",EDGE,"E436"),sQuery(id+"F0.wireOp",EDGE,"E437"),sQuery(id+"F0.wireOp",EDGE,"E438"),sQuery(id+"F0.wireOp",EDGE,"E439"),sQuery(id+"F0.wireOp",EDGE,"E440"),sQuery(id+"F0.wireOp",EDGE,"E441"),sQuery(id+"F0.wireOp",EDGE,"E442"),sQuery(id+"F0.wireOp",EDGE,"E443"),sQuery(id+"F0.wireOp",EDGE,"E444"),sQuery(id+"F0.wireOp",EDGE,"E445"),sQuery(id+"F0.wireOp",EDGE,"E446"),sQuery(id+"F0.wireOp",EDGE,"E447"),sQuery(id+"F0.wireOp",EDGE,"E448"),sQuery(id+"F0.wireOp",EDGE,"E449"),sQuery(id+"F0.wireOp",EDGE,"E450"),sQuery(id+"F0.wireOp",EDGE,"E451"),sQuery(id+"F0.wireOp",EDGE,"E452"),sQuery(id+"F0.wireOp",EDGE,"E453"),sQuery(id+"F0.wireOp",EDGE,"E454"),sQuery(id+"F0.wireOp",EDGE,"E455"),sQuery(id+"F0.wireOp",EDGE,"E456"),sQuery(id+"F0.wireOp",EDGE,"E457"),sQuery(id+"F0.wireOp",EDGE,"E458"),sQuery(id+"F0.wireOp",EDGE,"E459"),sQuery(id+"F0.wireOp",EDGE,"E460"),sQuery(id+"F0.wireOp",EDGE,"E461"),sQuery(id+"F0.wireOp",EDGE,"E462"),sQuery(id+"F0.wireOp",EDGE,"E463"),sQuery(id+"F0.wireOp",EDGE,"E464"),sQuery(id+"F0.wireOp",EDGE,"E465"),sQuery(id+"F0.wireOp",EDGE,"E466"),sQuery(id+"F0.wireOp",EDGE,"E467"),sQuery(id+"F0.wireOp",EDGE,"E468"),sQuery(id+"F0.wireOp",EDGE,"E469"),sQuery(id+"F0.wireOp",EDGE,"E470"),sQuery(id+"F0.wireOp",EDGE,"E471"),sQuery(id+"F0.wireOp",EDGE,"E472"),sQuery(id+"F0.wireOp",EDGE,"E473"),sQuery(id+"F0.wireOp",EDGE,"E474"),sQuery(id+"F0.wireOp",EDGE,"E475"),sQuery(id+"F0.wireOp",EDGE,"E476"),sQuery(id+"F0.wireOp",EDGE,"E477"),sQuery(id+"F0.wireOp",EDGE,"E478"),sQuery(id+"F0.wireOp",EDGE,"E479"),sQuery(id+"F0.wireOp",EDGE,"E480"),sQuery(id+"F0.wireOp",EDGE,"E481"),sQuery(id+"F0.wireOp",EDGE,"E482"),sQuery(id+"F0.wireOp",EDGE,"E483"),sQuery(id+"F0.wireOp",EDGE,"E484"),sQuery(id+"F0.wireOp",EDGE,"E485"),sQuery(id+"F0.wireOp",EDGE,"E486"),sQuery(id+"F0.wireOp",EDGE,"E487"),sQuery(id+"F0.wireOp",EDGE,"E488"),sQuery(id+"F0.wireOp",EDGE,"E489"),sQuery(id+"F0.wireOp",EDGE,"E490"),sQuery(id+"F0.wireOp",EDGE,"E491"),sQuery(id+"F0.wireOp",EDGE,"E492"),sQuery(id+"F0.wireOp",EDGE,"E493"),sQuery(id+"F0.wireOp",EDGE,"E494"),sQuery(id+"F0.wireOp",EDGE,"E495"),sQuery(id+"F0.wireOp",EDGE,"E496"),sQuery(id+"F0.wireOp",EDGE,"E497"),sQuery(id+"F0.wireOp",EDGE,"E498"),sQuery(id+"F0.wireOp",EDGE,"E499"),sQuery(id+"F0.wireOp",EDGE,"E500"),sQuery(id+"F0.wireOp",EDGE,"E501"),sQuery(id+"F0.wireOp",EDGE,"E502"),sQuery(id+"F0.wireOp",EDGE,"E503"),sQuery(id+"F0.wireOp",EDGE,"E504"),sQuery(id+"F0.wireOp",EDGE,"E505"),sQuery(id+"F0.wireOp",EDGE,"E506"),sQuery(id+"F0.wireOp",EDGE,"E507"),sQuery(id+"F0.wireOp",EDGE,"E508"),sQuery(id+"F0.wireOp",EDGE,"E509"),sQuery(id+"F0.wireOp",EDGE,"E510"),sQuery(id+"F0.wireOp",EDGE,"E511"),sQuery(id+"F0.wireOp",EDGE,"E512"),sQuery(id+"F0.wireOp",EDGE,"E513"),sQuery(id+"F0.wireOp",EDGE,"E514"),sQuery(id+"F0.wireOp",EDGE,"E515"),sQuery(id+"F0.wireOp",EDGE,"E516"),sQuery(id+"F0.wireOp",EDGE,"E517"),sQuery(id+"F0.wireOp",EDGE,"E518"),sQuery(id+"F0.wireOp",EDGE,"E519"),sQuery(id+"F0.wireOp",EDGE,"E520"),sQuery(id+"F0.wireOp",EDGE,"E521"),sQuery(id+"F0.wireOp",EDGE,"E522"),sQuery(id+"F0.wireOp",EDGE,"E523"),sQuery(id+"F0.wireOp",EDGE,"E524"),sQuery(id+"F0.wireOp",EDGE,"E525"),sQuery(id+"F0.wireOp",EDGE,"E526"),sQuery(id+"F0.wireOp",EDGE,"E527"),sQuery(id+"F0.wireOp",EDGE,"E528"),sQuery(id+"F0.wireOp",EDGE,"E529"),sQuery(id+"F0.wireOp",EDGE,"E530"),sQuery(id+"F0.wireOp",EDGE,"E531"),sQuery(id+"F0.wireOp",EDGE,"E532"),sQuery(id+"F0.wireOp",EDGE,"E533"),sQuery(id+"F0.wireOp",EDGE,"E534"),sQuery(id+"F0.wireOp",EDGE,"E535"),sQuery(id+"F0.wireOp",EDGE,"E536"),sQuery(id+"F0.wireOp",EDGE,"E537"),sQuery(id+"F0.wireOp",EDGE,"E538"),sQuery(id+"F0.wireOp",EDGE,"E539"),sQuery(id+"F0.wireOp",EDGE,"E540"),sQuery(id+"F0.wireOp",EDGE,"E541"),sQuery(id+"F0.wireOp",EDGE,"E542"),sQuery(id+"F0.wireOp",EDGE,"E543"),sQuery(id+"F0.wireOp",EDGE,"E544"),sQuery(id+"F0.wireOp",EDGE,"E545"),sQuery(id+"F0.wireOp",EDGE,"E546"),sQuery(id+"F0.wireOp",EDGE,"E547"),sQuery(id+"F0.wireOp",EDGE,"E548"),sQuery(id+"F0.wireOp",EDGE,"E549"),sQuery(id+"F0.wireOp",EDGE,"E550"),sQuery(id+"F0.wireOp",EDGE,"E551"),sQuery(id+"F0.wireOp",EDGE,"E552"),sQuery(id+"F0.wireOp",EDGE,"E553"),sQuery(id+"F0.wireOp",EDGE,"E554"),sQuery(id+"F0.wireOp",EDGE,"E555"),sQuery(id+"F0.wireOp",EDGE,"E556"),sQuery(id+"F0.wireOp",EDGE,"E557"),sQuery(id+"F0.wireOp",EDGE,"E558"),sQuery(id+"F0.wireOp",EDGE,"E559"),sQuery(id+"F0.wireOp",EDGE,"E560"),sQuery(id+"F0.wireOp",EDGE,"E561"),sQuery(id+"F0.wireOp",EDGE,"E562"),sQuery(id+"F0.wireOp",EDGE,"E563"),sQuery(id+"F0.wireOp",EDGE,"E564"),sQuery(id+"F0.wireOp",EDGE,"E565"),sQuery(id+"F0.wireOp",EDGE,"E566"),sQuery(id+"F0.wireOp",EDGE,"E567"),sQuery(id+"F0.wireOp",EDGE,"E568"),sQuery(id+"F0.wireOp",EDGE,"E569"),sQuery(id+"F0.wireOp",EDGE,"E570"),sQuery(id+"F0.wireOp",EDGE,"E571"),sQuery(id+"F0.wireOp",EDGE,"E572"),sQuery(id+"F0.wireOp",EDGE,"E573"),sQuery(id+"F0.wireOp",EDGE,"E574"),sQuery(id+"F0.wireOp",EDGE,"E575"),sQuery(id+"F0.wireOp",EDGE,"E576"),sQuery(id+"F0.wireOp",EDGE,"E577"),sQuery(id+"F0.wireOp",EDGE,"E578"),sQuery(id+"F0.wireOp",EDGE,"E579"),sQuery(id+"F0.wireOp",EDGE,"E580"),sQuery(id+"F0.wireOp",EDGE,"E581"),sQuery(id+"F0.wireOp",EDGE,"E582"),sQuery(id+"F0.wireOp",EDGE,"E583"),sQuery(id+"F0.wireOp",EDGE,"E584"),sQuery(id+"F0.wireOp",EDGE,"E585"),sQuery(id+"F0.wireOp",EDGE,"E586"),sQuery(id+"F0.wireOp",EDGE,"E587"),sQuery(id+"F0.wireOp",EDGE,"E588"),sQuery(id+"F0.wireOp",EDGE,"E589"),sQuery(id+"F0.wireOp",EDGE,"E590"),sQuery(id+"F0.wireOp",EDGE,"E591")])]});
            transform(context, id + "F4", {"entities" : qUnion([Q0]), "transformType" : TransformType.TRANSLATION_3D, "dx" : -304.8 * mm, "dy" : 3124.2 * mm, "dz" : 2286 * mm, "makeCopy" : false});
        }
        {
            var Q0;
            Q0=makeQuery(id+"F1.opExtrude","CAP_FACE",FACE,{"disambiguationData":[OSD([sQuery(id+"F0.wireOp",EDGE,"E0"),sQuery(id+"F0.wireOp",EDGE,"E1"),sQuery(id+"F0.wireOp",EDGE,"E2"),sQuery(id+"F0.wireOp",EDGE,"E3"),sQuery(id+"F0.wireOp",EDGE,"E4"),sQuery(id+"F0.wireOp",EDGE,"E5"),sQuery(id+"F0.wireOp",EDGE,"E6"),sQuery(id+"F0.wireOp",EDGE,"E7"),sQuery(id+"F0.wireOp",EDGE,"E8"),sQuery(id+"F0.wireOp",EDGE,"E9"),sQuery(id+"F0.wireOp",EDGE,"E10"),sQuery(id+"F0.wireOp",EDGE,"E11"),sQuery(id+"F0.wireOp",EDGE,"E12"),sQuery(id+"F0.wireOp",EDGE,"E13"),sQuery(id+"F0.wireOp",EDGE,"E14"),sQuery(id+"F0.wireOp",EDGE,"E15"),sQuery(id+"F0.wireOp",EDGE,"E16"),sQuery(id+"F0.wireOp",EDGE,"E17"),sQuery(id+"F0.wireOp",EDGE,"E18"),sQuery(id+"F0.wireOp",EDGE,"E19"),sQuery(id+"F0.wireOp",EDGE,"E20"),sQuery(id+"F0.wireOp",EDGE,"E21"),sQuery(id+"F0.wireOp",EDGE,"E22"),sQuery(id+"F0.wireOp",EDGE,"E23"),sQuery(id+"F0.wireOp",EDGE,"E24"),sQuery(id+"F0.wireOp",EDGE,"E25"),sQuery(id+"F0.wireOp",EDGE,"E26"),sQuery(id+"F0.wireOp",EDGE,"E27"),sQuery(id+"F0.wireOp",EDGE,"E28"),sQuery(id+"F0.wireOp",EDGE,"E29"),sQuery(id+"F0.wireOp",EDGE,"E30"),sQuery(id+"F0.wireOp",EDGE,"E31"),sQuery(id+"F0.wireOp",EDGE,"E32"),sQuery(id+"F0.wireOp",EDGE,"E33"),sQuery(id+"F0.wireOp",EDGE,"E34"),sQuery(id+"F0.wireOp",EDGE,"E35"),sQuery(id+"F0.wireOp",EDGE,"E36"),sQuery(id+"F0.wireOp",EDGE,"E37"),sQuery(id+"F0.wireOp",EDGE,"E38"),sQuery(id+"F0.wireOp",EDGE,"E39"),sQuery(id+"F0.wireOp",EDGE,"E40"),sQuery(id+"F0.wireOp",EDGE,"E41"),sQuery(id+"F0.wireOp",EDGE,"E42"),sQuery(id+"F0.wireOp",EDGE,"E43"),sQuery(id+"F0.wireOp",EDGE,"E44"),sQuery(id+"F0.wireOp",EDGE,"E45"),sQuery(id+"F0.wireOp",EDGE,"E46"),sQuery(id+"F0.wireOp",EDGE,"E47"),sQuery(id+"F0.wireOp",EDGE,"E48"),sQuery(id+"F0.wireOp",EDGE,"E49"),sQuery(id+"F0.wireOp",EDGE,"E50"),sQuery(id+"F0.wireOp",EDGE,"E51"),sQuery(id+"F0.wireOp",EDGE,"E52"),sQuery(id+"F0.wireOp",EDGE,"E53"),sQuery(id+"F0.wireOp",EDGE,"E54"),sQuery(id+"F0.wireOp",EDGE,"E55"),sQuery(id+"F0.wireOp",EDGE,"E56"),sQuery(id+"F0.wireOp",EDGE,"E57"),sQuery(id+"F0.wireOp",EDGE,"E58"),sQuery(id+"F0.wireOp",EDGE,"E59"),sQuery(id+"F0.wireOp",EDGE,"E60"),sQuery(id+"F0.wireOp",EDGE,"E61"),sQuery(id+"F0.wireOp",EDGE,"E62"),sQuery(id+"F0.wireOp",EDGE,"E63"),sQuery(id+"F0.wireOp",EDGE,"E64"),sQuery(id+"F0.wireOp",EDGE,"E65"),sQuery(id+"F0.wireOp",EDGE,"E66"),sQuery(id+"F0.wireOp",EDGE,"E67"),sQuery(id+"F0.wireOp",EDGE,"E68"),sQuery(id+"F0.wireOp",EDGE,"E69"),sQuery(id+"F0.wireOp",EDGE,"E70"),sQuery(id+"F0.wireOp",EDGE,"E71"),sQuery(id+"F0.wireOp",EDGE,"E72"),sQuery(id+"F0.wireOp",EDGE,"E73"),sQuery(id+"F0.wireOp",EDGE,"E74"),sQuery(id+"F0.wireOp",EDGE,"E75"),sQuery(id+"F0.wireOp",EDGE,"E76"),sQuery(id+"F0.wireOp",EDGE,"E77"),sQuery(id+"F0.wireOp",EDGE,"E78"),sQuery(id+"F0.wireOp",EDGE,"E79"),sQuery(id+"F0.wireOp",EDGE,"E80"),sQuery(id+"F0.wireOp",EDGE,"E81"),sQuery(id+"F0.wireOp",EDGE,"E82"),sQuery(id+"F0.wireOp",EDGE,"E83"),sQuery(id+"F0.wireOp",EDGE,"E84"),sQuery(id+"F0.wireOp",EDGE,"E85"),sQuery(id+"F0.wireOp",EDGE,"E86"),sQuery(id+"F0.wireOp",EDGE,"E87"),sQuery(id+"F0.wireOp",EDGE,"E88"),sQuery(id+"F0.wireOp",EDGE,"E89"),sQuery(id+"F0.wireOp",EDGE,"E90"),sQuery(id+"F0.wireOp",EDGE,"E91"),sQuery(id+"F0.wireOp",EDGE,"E92"),sQuery(id+"F0.wireOp",EDGE,"E93"),sQuery(id+"F0.wireOp",EDGE,"E94"),sQuery(id+"F0.wireOp",EDGE,"E95"),sQuery(id+"F0.wireOp",EDGE,"E96"),sQuery(id+"F0.wireOp",EDGE,"E97"),sQuery(id+"F0.wireOp",EDGE,"E98"),sQuery(id+"F0.wireOp",EDGE,"E99"),sQuery(id+"F0.wireOp",EDGE,"E100"),sQuery(id+"F0.wireOp",EDGE,"E101"),sQuery(id+"F0.wireOp",EDGE,"E102"),sQuery(id+"F0.wireOp",EDGE,"E103"),sQuery(id+"F0.wireOp",EDGE,"E104"),sQuery(id+"F0.wireOp",EDGE,"E105"),sQuery(id+"F0.wireOp",EDGE,"E106"),sQuery(id+"F0.wireOp",EDGE,"E107"),sQuery(id+"F0.wireOp",EDGE,"E108"),sQuery(id+"F0.wireOp",EDGE,"E109"),sQuery(id+"F0.wireOp",EDGE,"E110"),sQuery(id+"F0.wireOp",EDGE,"E111"),sQuery(id+"F0.wireOp",EDGE,"E112"),sQuery(id+"F0.wireOp",EDGE,"E113"),sQuery(id+"F0.wireOp",EDGE,"E114"),sQuery(id+"F0.wireOp",EDGE,"E115"),sQuery(id+"F0.wireOp",EDGE,"E116"),sQuery(id+"F0.wireOp",EDGE,"E117"),sQuery(id+"F0.wireOp",EDGE,"E118"),sQuery(id+"F0.wireOp",EDGE,"E119"),sQuery(id+"F0.wireOp",EDGE,"E120"),sQuery(id+"F0.wireOp",EDGE,"E121"),sQuery(id+"F0.wireOp",EDGE,"E122"),sQuery(id+"F0.wireOp",EDGE,"E123"),sQuery(id+"F0.wireOp",EDGE,"E124"),sQuery(id+"F0.wireOp",EDGE,"E125"),sQuery(id+"F0.wireOp",EDGE,"E126"),sQuery(id+"F0.wireOp",EDGE,"E127"),sQuery(id+"F0.wireOp",EDGE,"E128"),sQuery(id+"F0.wireOp",EDGE,"E129"),sQuery(id+"F0.wireOp",EDGE,"E130"),sQuery(id+"F0.wireOp",EDGE,"E131"),sQuery(id+"F0.wireOp",EDGE,"E132"),sQuery(id+"F0.wireOp",EDGE,"E133"),sQuery(id+"F0.wireOp",EDGE,"E134"),sQuery(id+"F0.wireOp",EDGE,"E135"),sQuery(id+"F0.wireOp",EDGE,"E136"),sQuery(id+"F0.wireOp",EDGE,"E137"),sQuery(id+"F0.wireOp",EDGE,"E138"),sQuery(id+"F0.wireOp",EDGE,"E139"),sQuery(id+"F0.wireOp",EDGE,"E140"),sQuery(id+"F0.wireOp",EDGE,"E141"),sQuery(id+"F0.wireOp",EDGE,"E142"),sQuery(id+"F0.wireOp",EDGE,"E143"),sQuery(id+"F0.wireOp",EDGE,"E144"),sQuery(id+"F0.wireOp",EDGE,"E145"),sQuery(id+"F0.wireOp",EDGE,"E146"),sQuery(id+"F0.wireOp",EDGE,"E147"),sQuery(id+"F0.wireOp",EDGE,"E148"),sQuery(id+"F0.wireOp",EDGE,"E149"),sQuery(id+"F0.wireOp",EDGE,"E150"),sQuery(id+"F0.wireOp",EDGE,"E151"),sQuery(id+"F0.wireOp",EDGE,"E152"),sQuery(id+"F0.wireOp",EDGE,"E153"),sQuery(id+"F0.wireOp",EDGE,"E154"),sQuery(id+"F0.wireOp",EDGE,"E155"),sQuery(id+"F0.wireOp",EDGE,"E156"),sQuery(id+"F0.wireOp",EDGE,"E157"),sQuery(id+"F0.wireOp",EDGE,"E158"),sQuery(id+"F0.wireOp",EDGE,"E159"),sQuery(id+"F0.wireOp",EDGE,"E160"),sQuery(id+"F0.wireOp",EDGE,"E161"),sQuery(id+"F0.wireOp",EDGE,"E162"),sQuery(id+"F0.wireOp",EDGE,"E163"),sQuery(id+"F0.wireOp",EDGE,"E164"),sQuery(id+"F0.wireOp",EDGE,"E165"),sQuery(id+"F0.wireOp",EDGE,"E166"),sQuery(id+"F0.wireOp",EDGE,"E167"),sQuery(id+"F0.wireOp",EDGE,"E168"),sQuery(id+"F0.wireOp",EDGE,"E169"),sQuery(id+"F0.wireOp",EDGE,"E170"),sQuery(id+"F0.wireOp",EDGE,"E171"),sQuery(id+"F0.wireOp",EDGE,"E172"),sQuery(id+"F0.wireOp",EDGE,"E173"),sQuery(id+"F0.wireOp",EDGE,"E174"),sQuery(id+"F0.wireOp",EDGE,"E175"),sQuery(id+"F0.wireOp",EDGE,"E176"),sQuery(id+"F0.wireOp",EDGE,"E177"),sQuery(id+"F0.wireOp",EDGE,"E178"),sQuery(id+"F0.wireOp",EDGE,"E179"),sQuery(id+"F0.wireOp",EDGE,"E180"),sQuery(id+"F0.wireOp",EDGE,"E181"),sQuery(id+"F0.wireOp",EDGE,"E182"),sQuery(id+"F0.wireOp",EDGE,"E183"),sQuery(id+"F0.wireOp",EDGE,"E184"),sQuery(id+"F0.wireOp",EDGE,"E185"),sQuery(id+"F0.wireOp",EDGE,"E186"),sQuery(id+"F0.wireOp",EDGE,"E187"),sQuery(id+"F0.wireOp",EDGE,"E188"),sQuery(id+"F0.wireOp",EDGE,"E189"),sQuery(id+"F0.wireOp",EDGE,"E190"),sQuery(id+"F0.wireOp",EDGE,"E191"),sQuery(id+"F0.wireOp",EDGE,"E192"),sQuery(id+"F0.wireOp",EDGE,"E193"),sQuery(id+"F0.wireOp",EDGE,"E194"),sQuery(id+"F0.wireOp",EDGE,"E195"),sQuery(id+"F0.wireOp",EDGE,"E196"),sQuery(id+"F0.wireOp",EDGE,"E197"),sQuery(id+"F0.wireOp",EDGE,"E198"),sQuery(id+"F0.wireOp",EDGE,"E199"),sQuery(id+"F0.wireOp",EDGE,"E200"),sQuery(id+"F0.wireOp",EDGE,"E201"),sQuery(id+"F0.wireOp",EDGE,"E202"),sQuery(id+"F0.wireOp",EDGE,"E203"),sQuery(id+"F0.wireOp",EDGE,"E204"),sQuery(id+"F0.wireOp",EDGE,"E205"),sQuery(id+"F0.wireOp",EDGE,"E206"),sQuery(id+"F0.wireOp",EDGE,"E207"),sQuery(id+"F0.wireOp",EDGE,"E208"),sQuery(id+"F0.wireOp",EDGE,"E209"),sQuery(id+"F0.wireOp",EDGE,"E210"),sQuery(id+"F0.wireOp",EDGE,"E211"),sQuery(id+"F0.wireOp",EDGE,"E212"),sQuery(id+"F0.wireOp",EDGE,"E213"),sQuery(id+"F0.wireOp",EDGE,"E214"),sQuery(id+"F0.wireOp",EDGE,"E215"),sQuery(id+"F0.wireOp",EDGE,"E216"),sQuery(id+"F0.wireOp",EDGE,"E217"),sQuery(id+"F0.wireOp",EDGE,"E218"),sQuery(id+"F0.wireOp",EDGE,"E219"),sQuery(id+"F0.wireOp",EDGE,"E220"),sQuery(id+"F0.wireOp",EDGE,"E221"),sQuery(id+"F0.wireOp",EDGE,"E222"),sQuery(id+"F0.wireOp",EDGE,"E223"),sQuery(id+"F0.wireOp",EDGE,"E224"),sQuery(id+"F0.wireOp",EDGE,"E225"),sQuery(id+"F0.wireOp",EDGE,"E226"),sQuery(id+"F0.wireOp",EDGE,"E227"),sQuery(id+"F0.wireOp",EDGE,"E228"),sQuery(id+"F0.wireOp",EDGE,"E229"),sQuery(id+"F0.wireOp",EDGE,"E230"),sQuery(id+"F0.wireOp",EDGE,"E231"),sQuery(id+"F0.wireOp",EDGE,"E232"),sQuery(id+"F0.wireOp",EDGE,"E233"),sQuery(id+"F0.wireOp",EDGE,"E234"),sQuery(id+"F0.wireOp",EDGE,"E235"),sQuery(id+"F0.wireOp",EDGE,"E236"),sQuery(id+"F0.wireOp",EDGE,"E237"),sQuery(id+"F0.wireOp",EDGE,"E238"),sQuery(id+"F0.wireOp",EDGE,"E239"),sQuery(id+"F0.wireOp",EDGE,"E240"),sQuery(id+"F0.wireOp",EDGE,"E241"),sQuery(id+"F0.wireOp",EDGE,"E242"),sQuery(id+"F0.wireOp",EDGE,"E243"),sQuery(id+"F0.wireOp",EDGE,"E244"),sQuery(id+"F0.wireOp",EDGE,"E245"),sQuery(id+"F0.wireOp",EDGE,"E246"),sQuery(id+"F0.wireOp",EDGE,"E247"),sQuery(id+"F0.wireOp",EDGE,"E248"),sQuery(id+"F0.wireOp",EDGE,"E249"),sQuery(id+"F0.wireOp",EDGE,"E250"),sQuery(id+"F0.wireOp",EDGE,"E251"),sQuery(id+"F0.wireOp",EDGE,"E252"),sQuery(id+"F0.wireOp",EDGE,"E253"),sQuery(id+"F0.wireOp",EDGE,"E254"),sQuery(id+"F0.wireOp",EDGE,"E255"),sQuery(id+"F0.wireOp",EDGE,"E256"),sQuery(id+"F0.wireOp",EDGE,"E257"),sQuery(id+"F0.wireOp",EDGE,"E258"),sQuery(id+"F0.wireOp",EDGE,"E259"),sQuery(id+"F0.wireOp",EDGE,"E260"),sQuery(id+"F0.wireOp",EDGE,"E261"),sQuery(id+"F0.wireOp",EDGE,"E262"),sQuery(id+"F0.wireOp",EDGE,"E263"),sQuery(id+"F0.wireOp",EDGE,"E264"),sQuery(id+"F0.wireOp",EDGE,"E265"),sQuery(id+"F0.wireOp",EDGE,"E266"),sQuery(id+"F0.wireOp",EDGE,"E267"),sQuery(id+"F0.wireOp",EDGE,"E268"),sQuery(id+"F0.wireOp",EDGE,"E269"),sQuery(id+"F0.wireOp",EDGE,"E270"),sQuery(id+"F0.wireOp",EDGE,"E271"),sQuery(id+"F0.wireOp",EDGE,"E272"),sQuery(id+"F0.wireOp",EDGE,"E273"),sQuery(id+"F0.wireOp",EDGE,"E274"),sQuery(id+"F0.wireOp",EDGE,"E275"),sQuery(id+"F0.wireOp",EDGE,"E276"),sQuery(id+"F0.wireOp",EDGE,"E277"),sQuery(id+"F0.wireOp",EDGE,"E278"),sQuery(id+"F0.wireOp",EDGE,"E279"),sQuery(id+"F0.wireOp",EDGE,"E280"),sQuery(id+"F0.wireOp",EDGE,"E281"),sQuery(id+"F0.wireOp",EDGE,"E282"),sQuery(id+"F0.wireOp",EDGE,"E283"),sQuery(id+"F0.wireOp",EDGE,"E284"),sQuery(id+"F0.wireOp",EDGE,"E285"),sQuery(id+"F0.wireOp",EDGE,"E286"),sQuery(id+"F0.wireOp",EDGE,"E287"),sQuery(id+"F0.wireOp",EDGE,"E288"),sQuery(id+"F0.wireOp",EDGE,"E289"),sQuery(id+"F0.wireOp",EDGE,"E290"),sQuery(id+"F0.wireOp",EDGE,"E291"),sQuery(id+"F0.wireOp",EDGE,"E292"),sQuery(id+"F0.wireOp",EDGE,"E293"),sQuery(id+"F0.wireOp",EDGE,"E294"),sQuery(id+"F0.wireOp",EDGE,"E295"),sQuery(id+"F0.wireOp",EDGE,"E296"),sQuery(id+"F0.wireOp",EDGE,"E297"),sQuery(id+"F0.wireOp",EDGE,"E298"),sQuery(id+"F0.wireOp",EDGE,"E299"),sQuery(id+"F0.wireOp",EDGE,"E300"),sQuery(id+"F0.wireOp",EDGE,"E301"),sQuery(id+"F0.wireOp",EDGE,"E302"),sQuery(id+"F0.wireOp",EDGE,"E303"),sQuery(id+"F0.wireOp",EDGE,"E304"),sQuery(id+"F0.wireOp",EDGE,"E305"),sQuery(id+"F0.wireOp",EDGE,"E306"),sQuery(id+"F0.wireOp",EDGE,"E307"),sQuery(id+"F0.wireOp",EDGE,"E308"),sQuery(id+"F0.wireOp",EDGE,"E309"),sQuery(id+"F0.wireOp",EDGE,"E310"),sQuery(id+"F0.wireOp",EDGE,"E311"),sQuery(id+"F0.wireOp",EDGE,"E312"),sQuery(id+"F0.wireOp",EDGE,"E313"),sQuery(id+"F0.wireOp",EDGE,"E314"),sQuery(id+"F0.wireOp",EDGE,"E315"),sQuery(id+"F0.wireOp",EDGE,"E316"),sQuery(id+"F0.wireOp",EDGE,"E317"),sQuery(id+"F0.wireOp",EDGE,"E318"),sQuery(id+"F0.wireOp",EDGE,"E319"),sQuery(id+"F0.wireOp",EDGE,"E320"),sQuery(id+"F0.wireOp",EDGE,"E321"),sQuery(id+"F0.wireOp",EDGE,"E322"),sQuery(id+"F0.wireOp",EDGE,"E323"),sQuery(id+"F0.wireOp",EDGE,"E324"),sQuery(id+"F0.wireOp",EDGE,"E325"),sQuery(id+"F0.wireOp",EDGE,"E326"),sQuery(id+"F0.wireOp",EDGE,"E327"),sQuery(id+"F0.wireOp",EDGE,"E328"),sQuery(id+"F0.wireOp",EDGE,"E329"),sQuery(id+"F0.wireOp",EDGE,"E330"),sQuery(id+"F0.wireOp",EDGE,"E331"),sQuery(id+"F0.wireOp",EDGE,"E332"),sQuery(id+"F0.wireOp",EDGE,"E333"),sQuery(id+"F0.wireOp",EDGE,"E334"),sQuery(id+"F0.wireOp",EDGE,"E335"),sQuery(id+"F0.wireOp",EDGE,"E336"),sQuery(id+"F0.wireOp",EDGE,"E337"),sQuery(id+"F0.wireOp",EDGE,"E338"),sQuery(id+"F0.wireOp",EDGE,"E339"),sQuery(id+"F0.wireOp",EDGE,"E340"),sQuery(id+"F0.wireOp",EDGE,"E341"),sQuery(id+"F0.wireOp",EDGE,"E342"),sQuery(id+"F0.wireOp",EDGE,"E343"),sQuery(id+"F0.wireOp",EDGE,"E344"),sQuery(id+"F0.wireOp",EDGE,"E345"),sQuery(id+"F0.wireOp",EDGE,"E346"),sQuery(id+"F0.wireOp",EDGE,"E347"),sQuery(id+"F0.wireOp",EDGE,"E348"),sQuery(id+"F0.wireOp",EDGE,"E349"),sQuery(id+"F0.wireOp",EDGE,"E350"),sQuery(id+"F0.wireOp",EDGE,"E351"),sQuery(id+"F0.wireOp",EDGE,"E352"),sQuery(id+"F0.wireOp",EDGE,"E353"),sQuery(id+"F0.wireOp",EDGE,"E354"),sQuery(id+"F0.wireOp",EDGE,"E355"),sQuery(id+"F0.wireOp",EDGE,"E356"),sQuery(id+"F0.wireOp",EDGE,"E357"),sQuery(id+"F0.wireOp",EDGE,"E358"),sQuery(id+"F0.wireOp",EDGE,"E359"),sQuery(id+"F0.wireOp",EDGE,"E360"),sQuery(id+"F0.wireOp",EDGE,"E361"),sQuery(id+"F0.wireOp",EDGE,"E362"),sQuery(id+"F0.wireOp",EDGE,"E363"),sQuery(id+"F0.wireOp",EDGE,"E364"),sQuery(id+"F0.wireOp",EDGE,"E365"),sQuery(id+"F0.wireOp",EDGE,"E366"),sQuery(id+"F0.wireOp",EDGE,"E367"),sQuery(id+"F0.wireOp",EDGE,"E368"),sQuery(id+"F0.wireOp",EDGE,"E369"),sQuery(id+"F0.wireOp",EDGE,"E370"),sQuery(id+"F0.wireOp",EDGE,"E371"),sQuery(id+"F0.wireOp",EDGE,"E372"),sQuery(id+"F0.wireOp",EDGE,"E373"),sQuery(id+"F0.wireOp",EDGE,"E374"),sQuery(id+"F0.wireOp",EDGE,"E375"),sQuery(id+"F0.wireOp",EDGE,"E376"),sQuery(id+"F0.wireOp",EDGE,"E377"),sQuery(id+"F0.wireOp",EDGE,"E378"),sQuery(id+"F0.wireOp",EDGE,"E379"),sQuery(id+"F0.wireOp",EDGE,"E380"),sQuery(id+"F0.wireOp",EDGE,"E381"),sQuery(id+"F0.wireOp",EDGE,"E382"),sQuery(id+"F0.wireOp",EDGE,"E383"),sQuery(id+"F0.wireOp",EDGE,"E384"),sQuery(id+"F0.wireOp",EDGE,"E385"),sQuery(id+"F0.wireOp",EDGE,"E386"),sQuery(id+"F0.wireOp",EDGE,"E387"),sQuery(id+"F0.wireOp",EDGE,"E388"),sQuery(id+"F0.wireOp",EDGE,"E389"),sQuery(id+"F0.wireOp",EDGE,"E390"),sQuery(id+"F0.wireOp",EDGE,"E391"),sQuery(id+"F0.wireOp",EDGE,"E392"),sQuery(id+"F0.wireOp",EDGE,"E393"),sQuery(id+"F0.wireOp",EDGE,"E394"),sQuery(id+"F0.wireOp",EDGE,"E395"),sQuery(id+"F0.wireOp",EDGE,"E396"),sQuery(id+"F0.wireOp",EDGE,"E397"),sQuery(id+"F0.wireOp",EDGE,"E398"),sQuery(id+"F0.wireOp",EDGE,"E399"),sQuery(id+"F0.wireOp",EDGE,"E400"),sQuery(id+"F0.wireOp",EDGE,"E401"),sQuery(id+"F0.wireOp",EDGE,"E402"),sQuery(id+"F0.wireOp",EDGE,"E403"),sQuery(id+"F0.wireOp",EDGE,"E404"),sQuery(id+"F0.wireOp",EDGE,"E405"),sQuery(id+"F0.wireOp",EDGE,"E406"),sQuery(id+"F0.wireOp",EDGE,"E407"),sQuery(id+"F0.wireOp",EDGE,"E408"),sQuery(id+"F0.wireOp",EDGE,"E409"),sQuery(id+"F0.wireOp",EDGE,"E410"),sQuery(id+"F0.wireOp",EDGE,"E411"),sQuery(id+"F0.wireOp",EDGE,"E412"),sQuery(id+"F0.wireOp",EDGE,"E413"),sQuery(id+"F0.wireOp",EDGE,"E414"),sQuery(id+"F0.wireOp",EDGE,"E415"),sQuery(id+"F0.wireOp",EDGE,"E416"),sQuery(id+"F0.wireOp",EDGE,"E417"),sQuery(id+"F0.wireOp",EDGE,"E418"),sQuery(id+"F0.wireOp",EDGE,"E419"),sQuery(id+"F0.wireOp",EDGE,"E420"),sQuery(id+"F0.wireOp",EDGE,"E421"),sQuery(id+"F0.wireOp",EDGE,"E422"),sQuery(id+"F0.wireOp",EDGE,"E423"),sQuery(id+"F0.wireOp",EDGE,"E424"),sQuery(id+"F0.wireOp",EDGE,"E425"),sQuery(id+"F0.wireOp",EDGE,"E426"),sQuery(id+"F0.wireOp",EDGE,"E427"),sQuery(id+"F0.wireOp",EDGE,"E428"),sQuery(id+"F0.wireOp",EDGE,"E429"),sQuery(id+"F0.wireOp",EDGE,"E430"),sQuery(id+"F0.wireOp",EDGE,"E431"),sQuery(id+"F0.wireOp",EDGE,"E432"),sQuery(id+"F0.wireOp",EDGE,"E433"),sQuery(id+"F0.wireOp",EDGE,"E434"),sQuery(id+"F0.wireOp",EDGE,"E435"),sQuery(id+"F0.wireOp",EDGE,"E436"),sQuery(id+"F0.wireOp",EDGE,"E437"),sQuery(id+"F0.wireOp",EDGE,"E438"),sQuery(id+"F0.wireOp",EDGE,"E439"),sQuery(id+"F0.wireOp",EDGE,"E440"),sQuery(id+"F0.wireOp",EDGE,"E441"),sQuery(id+"F0.wireOp",EDGE,"E442"),sQuery(id+"F0.wireOp",EDGE,"E443"),sQuery(id+"F0.wireOp",EDGE,"E444"),sQuery(id+"F0.wireOp",EDGE,"E445"),sQuery(id+"F0.wireOp",EDGE,"E446"),sQuery(id+"F0.wireOp",EDGE,"E447"),sQuery(id+"F0.wireOp",EDGE,"E448"),sQuery(id+"F0.wireOp",EDGE,"E449"),sQuery(id+"F0.wireOp",EDGE,"E450"),sQuery(id+"F0.wireOp",EDGE,"E451"),sQuery(id+"F0.wireOp",EDGE,"E452"),sQuery(id+"F0.wireOp",EDGE,"E453"),sQuery(id+"F0.wireOp",EDGE,"E454"),sQuery(id+"F0.wireOp",EDGE,"E455"),sQuery(id+"F0.wireOp",EDGE,"E456"),sQuery(id+"F0.wireOp",EDGE,"E457"),sQuery(id+"F0.wireOp",EDGE,"E458"),sQuery(id+"F0.wireOp",EDGE,"E459"),sQuery(id+"F0.wireOp",EDGE,"E460"),sQuery(id+"F0.wireOp",EDGE,"E461"),sQuery(id+"F0.wireOp",EDGE,"E462"),sQuery(id+"F0.wireOp",EDGE,"E463"),sQuery(id+"F0.wireOp",EDGE,"E464"),sQuery(id+"F0.wireOp",EDGE,"E465"),sQuery(id+"F0.wireOp",EDGE,"E466"),sQuery(id+"F0.wireOp",EDGE,"E467"),sQuery(id+"F0.wireOp",EDGE,"E468"),sQuery(id+"F0.wireOp",EDGE,"E469"),sQuery(id+"F0.wireOp",EDGE,"E470"),sQuery(id+"F0.wireOp",EDGE,"E471"),sQuery(id+"F0.wireOp",EDGE,"E472"),sQuery(id+"F0.wireOp",EDGE,"E473"),sQuery(id+"F0.wireOp",EDGE,"E474"),sQuery(id+"F0.wireOp",EDGE,"E475"),sQuery(id+"F0.wireOp",EDGE,"E476"),sQuery(id+"F0.wireOp",EDGE,"E477"),sQuery(id+"F0.wireOp",EDGE,"E478"),sQuery(id+"F0.wireOp",EDGE,"E479"),sQuery(id+"F0.wireOp",EDGE,"E480"),sQuery(id+"F0.wireOp",EDGE,"E481"),sQuery(id+"F0.wireOp",EDGE,"E482"),sQuery(id+"F0.wireOp",EDGE,"E483"),sQuery(id+"F0.wireOp",EDGE,"E484"),sQuery(id+"F0.wireOp",EDGE,"E485"),sQuery(id+"F0.wireOp",EDGE,"E486"),sQuery(id+"F0.wireOp",EDGE,"E487"),sQuery(id+"F0.wireOp",EDGE,"E488"),sQuery(id+"F0.wireOp",EDGE,"E489"),sQuery(id+"F0.wireOp",EDGE,"E490"),sQuery(id+"F0.wireOp",EDGE,"E491"),sQuery(id+"F0.wireOp",EDGE,"E492"),sQuery(id+"F0.wireOp",EDGE,"E493"),sQuery(id+"F0.wireOp",EDGE,"E494"),sQuery(id+"F0.wireOp",EDGE,"E495"),sQuery(id+"F0.wireOp",EDGE,"E496"),sQuery(id+"F0.wireOp",EDGE,"E497"),sQuery(id+"F0.wireOp",EDGE,"E498"),sQuery(id+"F0.wireOp",EDGE,"E499"),sQuery(id+"F0.wireOp",EDGE,"E500"),sQuery(id+"F0.wireOp",EDGE,"E501"),sQuery(id+"F0.wireOp",EDGE,"E502"),sQuery(id+"F0.wireOp",EDGE,"E503"),sQuery(id+"F0.wireOp",EDGE,"E504"),sQuery(id+"F0.wireOp",EDGE,"E505"),sQuery(id+"F0.wireOp",EDGE,"E506"),sQuery(id+"F0.wireOp",EDGE,"E507"),sQuery(id+"F0.wireOp",EDGE,"E508"),sQuery(id+"F0.wireOp",EDGE,"E509"),sQuery(id+"F0.wireOp",EDGE,"E510"),sQuery(id+"F0.wireOp",EDGE,"E511"),sQuery(id+"F0.wireOp",EDGE,"E512"),sQuery(id+"F0.wireOp",EDGE,"E513"),sQuery(id+"F0.wireOp",EDGE,"E514"),sQuery(id+"F0.wireOp",EDGE,"E515"),sQuery(id+"F0.wireOp",EDGE,"E516"),sQuery(id+"F0.wireOp",EDGE,"E517"),sQuery(id+"F0.wireOp",EDGE,"E518"),sQuery(id+"F0.wireOp",EDGE,"E519"),sQuery(id+"F0.wireOp",EDGE,"E520"),sQuery(id+"F0.wireOp",EDGE,"E521"),sQuery(id+"F0.wireOp",EDGE,"E522"),sQuery(id+"F0.wireOp",EDGE,"E523"),sQuery(id+"F0.wireOp",EDGE,"E524"),sQuery(id+"F0.wireOp",EDGE,"E525"),sQuery(id+"F0.wireOp",EDGE,"E526"),sQuery(id+"F0.wireOp",EDGE,"E527"),sQuery(id+"F0.wireOp",EDGE,"E528"),sQuery(id+"F0.wireOp",EDGE,"E529"),sQuery(id+"F0.wireOp",EDGE,"E530"),sQuery(id+"F0.wireOp",EDGE,"E531"),sQuery(id+"F0.wireOp",EDGE,"E532"),sQuery(id+"F0.wireOp",EDGE,"E533"),sQuery(id+"F0.wireOp",EDGE,"E534"),sQuery(id+"F0.wireOp",EDGE,"E535"),sQuery(id+"F0.wireOp",EDGE,"E536"),sQuery(id+"F0.wireOp",EDGE,"E537"),sQuery(id+"F0.wireOp",EDGE,"E538"),sQuery(id+"F0.wireOp",EDGE,"E539"),sQuery(id+"F0.wireOp",EDGE,"E540"),sQuery(id+"F0.wireOp",EDGE,"E541"),sQuery(id+"F0.wireOp",EDGE,"E542"),sQuery(id+"F0.wireOp",EDGE,"E543"),sQuery(id+"F0.wireOp",EDGE,"E544"),sQuery(id+"F0.wireOp",EDGE,"E545"),sQuery(id+"F0.wireOp",EDGE,"E546"),sQuery(id+"F0.wireOp",EDGE,"E547"),sQuery(id+"F0.wireOp",EDGE,"E548"),sQuery(id+"F0.wireOp",EDGE,"E549"),sQuery(id+"F0.wireOp",EDGE,"E550"),sQuery(id+"F0.wireOp",EDGE,"E551"),sQuery(id+"F0.wireOp",EDGE,"E552"),sQuery(id+"F0.wireOp",EDGE,"E553"),sQuery(id+"F0.wireOp",EDGE,"E554"),sQuery(id+"F0.wireOp",EDGE,"E555"),sQuery(id+"F0.wireOp",EDGE,"E556"),sQuery(id+"F0.wireOp",EDGE,"E557"),sQuery(id+"F0.wireOp",EDGE,"E558"),sQuery(id+"F0.wireOp",EDGE,"E559"),sQuery(id+"F0.wireOp",EDGE,"E560"),sQuery(id+"F0.wireOp",EDGE,"E561"),sQuery(id+"F0.wireOp",EDGE,"E562"),sQuery(id+"F0.wireOp",EDGE,"E563"),sQuery(id+"F0.wireOp",EDGE,"E564"),sQuery(id+"F0.wireOp",EDGE,"E565"),sQuery(id+"F0.wireOp",EDGE,"E566"),sQuery(id+"F0.wireOp",EDGE,"E567"),sQuery(id+"F0.wireOp",EDGE,"E568"),sQuery(id+"F0.wireOp",EDGE,"E569"),sQuery(id+"F0.wireOp",EDGE,"E570"),sQuery(id+"F0.wireOp",EDGE,"E571"),sQuery(id+"F0.wireOp",EDGE,"E572"),sQuery(id+"F0.wireOp",EDGE,"E573"),sQuery(id+"F0.wireOp",EDGE,"E574"),sQuery(id+"F0.wireOp",EDGE,"E575"),sQuery(id+"F0.wireOp",EDGE,"E576"),sQuery(id+"F0.wireOp",EDGE,"E577"),sQuery(id+"F0.wireOp",EDGE,"E578"),sQuery(id+"F0.wireOp",EDGE,"E579"),sQuery(id+"F0.wireOp",EDGE,"E580"),sQuery(id+"F0.wireOp",EDGE,"E581"),sQuery(id+"F0.wireOp",EDGE,"E582"),sQuery(id+"F0.wireOp",EDGE,"E583"),sQuery(id+"F0.wireOp",EDGE,"E584"),sQuery(id+"F0.wireOp",EDGE,"E585"),sQuery(id+"F0.wireOp",EDGE,"E586"),sQuery(id+"F0.wireOp",EDGE,"E587"),sQuery(id+"F0.wireOp",EDGE,"E588"),sQuery(id+"F0.wireOp",EDGE,"E589"),sQuery(id+"F0.wireOp",EDGE,"E590"),sQuery(id+"F0.wireOp",EDGE,"E591")])],"isStart":false});
            extrude(context, id + "F5", {"entities" : qUnion([Q0]), "operationType" : NewBodyOperationType.ADD, "depth" : 6.35 * mm, "offsetDistance" : 25.4 * mm});
        }
    });
